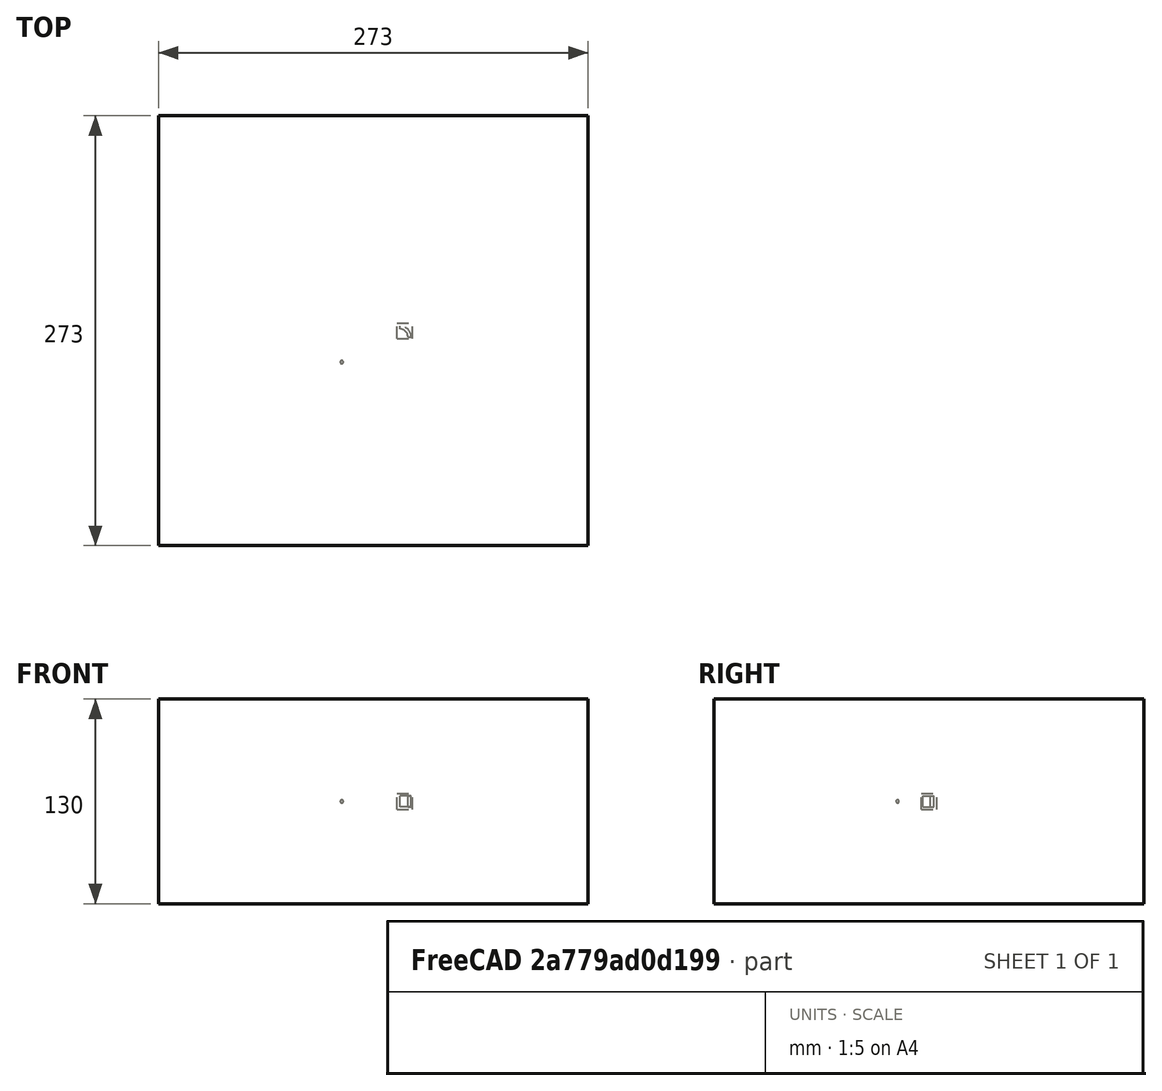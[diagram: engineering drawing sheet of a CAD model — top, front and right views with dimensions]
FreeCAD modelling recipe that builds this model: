
FCSTD DOCUMENT  (FreeCAD 1.0R39109 (Git))
Label: polarArray-of-Part-base-xformed-offcenter
License: All rights reserved
LicenseURL: http://en.wikipedia.org/wiki/All_rights_reserved
objects: App::DocumentObjectGroupPython×1251, App::Part×5, Part::FeaturePython×4, Part::Sphere×1
note: 4 computed .brp shape members not serialized (recipe doc carries the construction recipe); baked Part::Feature solids carry a one-line shape summary decoded from their .brp

FEATURE [App::DocumentObjectGroupPython] HALFPI  # scripted group (container) (typed FeaturePython)
  name = HALFPI
  value = pi/2.
FEATURE [App::DocumentObjectGroupPython] PI  # scripted group (container) (typed FeaturePython)
  name = PI
  value = 1.*pi
FEATURE [App::DocumentObjectGroupPython] TWOPI  # scripted group (container) (typed FeaturePython)
  name = TWOPI
  value = 2.*pi
FEATURE [App::DocumentObjectGroupPython] Constants  # scripted group (container) (typed FeaturePython)
  Group = -> [HALFPI,PI,TWOPI]
FEATURE [App::DocumentObjectGroupPython] Variables  # scripted group (container) (typed FeaturePython)
FEATURE [App::DocumentObjectGroupPython] Quantities  # scripted group (container) (typed FeaturePython)
FEATURE [App::DocumentObjectGroupPython] Isotopes  # scripted group (container) (typed FeaturePython)
FEATURE [App::DocumentObjectGroupPython] Elements  # scripted group (container) (typed FeaturePython)
FEATURE [App::DocumentObjectGroupPython] Matrix  # scripted group (container) (typed FeaturePython)
FEATURE [App::DocumentObjectGroupPython] Surfaces  # scripted group (container) (typed FeaturePython)
FEATURE [App::DocumentObjectGroupPython] Opticals  # scripted group (container) (typed FeaturePython)
  Group = -> [Matrix,Surfaces]
FEATURE [App::DocumentObjectGroupPython] G4Isotopes  # scripted group (container) (typed FeaturePython)
FEATURE [App::DocumentObjectGroupPython] H_element  # scripted group (container) (typed FeaturePython)
  Z = 1
  atom_value = 1.008
  formula = H
  name = H_element
FEATURE [App::DocumentObjectGroupPython] He_element  # scripted group (container) (typed FeaturePython)
  Z = 2
  atom_value = 4.0026
  formula = He
  name = He_element
FEATURE [App::DocumentObjectGroupPython] Li_element  # scripted group (container) (typed FeaturePython)
  Z = 3
  atom_value = 6.94
  formula = Li
  name = Li_element
FEATURE [App::DocumentObjectGroupPython] Be_element  # scripted group (container) (typed FeaturePython)
  Z = 4
  atom_value = 9.01218
  formula = Be
  name = Be_element
FEATURE [App::DocumentObjectGroupPython] B_element  # scripted group (container) (typed FeaturePython)
  Z = 5
  atom_value = 10.81
  formula = B
  name = B_element
FEATURE [App::DocumentObjectGroupPython] C_element  # scripted group (container) (typed FeaturePython)
  Z = 6
  atom_value = 12.011
  formula = C
  name = C_element
FEATURE [App::DocumentObjectGroupPython] N_element  # scripted group (container) (typed FeaturePython)
  Z = 7
  atom_value = 14.007
  formula = N
  name = N_element
FEATURE [App::DocumentObjectGroupPython] O_element  # scripted group (container) (typed FeaturePython)
  Z = 8
  atom_value = 15.999
  formula = O
  name = O_element
FEATURE [App::DocumentObjectGroupPython] F_element  # scripted group (container) (typed FeaturePython)
  Z = 9
  atom_value = 18.9984
  formula = F
  name = F_element
FEATURE [App::DocumentObjectGroupPython] Ne_element  # scripted group (container) (typed FeaturePython)
  Z = 10
  atom_value = 20.1797
  formula = Ne
  name = Ne_element
FEATURE [App::DocumentObjectGroupPython] Na_element  # scripted group (container) (typed FeaturePython)
  Z = 11
  atom_value = 22.9898
  formula = Na
  name = Na_element
FEATURE [App::DocumentObjectGroupPython] Mg_element  # scripted group (container) (typed FeaturePython)
  Z = 12
  atom_value = 24.305
  formula = Mg
  name = Mg_element
FEATURE [App::DocumentObjectGroupPython] Al_element  # scripted group (container) (typed FeaturePython)
  Z = 13
  atom_value = 26.9815
  formula = Al
  name = Al_element
FEATURE [App::DocumentObjectGroupPython] Si_element  # scripted group (container) (typed FeaturePython)
  Z = 14
  atom_value = 28.085
  formula = Si
  name = Si_element
FEATURE [App::DocumentObjectGroupPython] P_element  # scripted group (container) (typed FeaturePython)
  Z = 15
  atom_value = 30.9738
  formula = P
  name = P_element
FEATURE [App::DocumentObjectGroupPython] S_element  # scripted group (container) (typed FeaturePython)
  Z = 16
  atom_value = 32.06
  formula = S
  name = S_element
FEATURE [App::DocumentObjectGroupPython] Cl_element  # scripted group (container) (typed FeaturePython)
  Z = 17
  atom_value = 35.45
  formula = Cl
  name = Cl_element
FEATURE [App::DocumentObjectGroupPython] Ar_element  # scripted group (container) (typed FeaturePython)
  Z = 18
  atom_value = 39.95
  formula = Ar
  name = Ar_element
FEATURE [App::DocumentObjectGroupPython] K_element  # scripted group (container) (typed FeaturePython)
  Z = 19
  atom_value = 39.0983
  formula = K
  name = K_element
FEATURE [App::DocumentObjectGroupPython] Ca_element  # scripted group (container) (typed FeaturePython)
  Z = 20
  atom_value = 40.078
  formula = Ca
  name = Ca_element
FEATURE [App::DocumentObjectGroupPython] Sc_element  # scripted group (container) (typed FeaturePython)
  Z = 21
  atom_value = 44.9559
  formula = Sc
  name = Sc_element
FEATURE [App::DocumentObjectGroupPython] Ti_element  # scripted group (container) (typed FeaturePython)
  Z = 22
  atom_value = 47.867
  formula = Ti
  name = Ti_element
FEATURE [App::DocumentObjectGroupPython] V_element  # scripted group (container) (typed FeaturePython)
  Z = 23
  atom_value = 50.9415
  formula = V
  name = V_element
FEATURE [App::DocumentObjectGroupPython] Cr_element  # scripted group (container) (typed FeaturePython)
  Z = 24
  atom_value = 51.9961
  formula = Cr
  name = Cr_element
FEATURE [App::DocumentObjectGroupPython] Mn_element  # scripted group (container) (typed FeaturePython)
  Z = 25
  atom_value = 54.938
  formula = Mn
  name = Mn_element
FEATURE [App::DocumentObjectGroupPython] Fe_element  # scripted group (container) (typed FeaturePython)
  Z = 26
  atom_value = 55.845
  formula = Fe
  name = Fe_element
FEATURE [App::DocumentObjectGroupPython] Co_element  # scripted group (container) (typed FeaturePython)
  Z = 27
  atom_value = 58.9332
  formula = Co
  name = Co_element
FEATURE [App::DocumentObjectGroupPython] Ni_element  # scripted group (container) (typed FeaturePython)
  Z = 28
  atom_value = 58.6934
  formula = Ni
  name = Ni_element
FEATURE [App::DocumentObjectGroupPython] Cu_element  # scripted group (container) (typed FeaturePython)
  Z = 29
  atom_value = 63.546
  formula = Cu
  name = Cu_element
FEATURE [App::DocumentObjectGroupPython] Zn_element  # scripted group (container) (typed FeaturePython)
  Z = 30
  atom_value = 65.38
  formula = Zn
  name = Zn_element
FEATURE [App::DocumentObjectGroupPython] Ga_element  # scripted group (container) (typed FeaturePython)
  Z = 31
  atom_value = 69.723
  formula = Ga
  name = Ga_element
FEATURE [App::DocumentObjectGroupPython] Ge_element  # scripted group (container) (typed FeaturePython)
  Z = 32
  atom_value = 72.63
  formula = Ge
  name = Ge_element
FEATURE [App::DocumentObjectGroupPython] As_element  # scripted group (container) (typed FeaturePython)
  Z = 33
  atom_value = 74.9216
  formula = As
  name = As_element
FEATURE [App::DocumentObjectGroupPython] Se_element  # scripted group (container) (typed FeaturePython)
  Z = 34
  atom_value = 78.971
  formula = Se
  name = Se_element
FEATURE [App::DocumentObjectGroupPython] Br_element  # scripted group (container) (typed FeaturePython)
  Z = 35
  atom_value = 79.904
  formula = Br
  name = Br_element
FEATURE [App::DocumentObjectGroupPython] Kr_element  # scripted group (container) (typed FeaturePython)
  Z = 36
  atom_value = 83.798
  formula = Kr
  name = Kr_element
FEATURE [App::DocumentObjectGroupPython] Rb_element  # scripted group (container) (typed FeaturePython)
  Z = 37
  atom_value = 85.4678
  formula = Rb
  name = Rb_element
FEATURE [App::DocumentObjectGroupPython] Sr_element  # scripted group (container) (typed FeaturePython)
  Z = 38
  atom_value = 87.62
  formula = Sr
  name = Sr_element
FEATURE [App::DocumentObjectGroupPython] Y_element  # scripted group (container) (typed FeaturePython)
  Z = 39
  atom_value = 88.9058
  formula = Y
  name = Y_element
FEATURE [App::DocumentObjectGroupPython] Zr_element  # scripted group (container) (typed FeaturePython)
  Z = 40
  atom_value = 91.224
  formula = Zr
  name = Zr_element
FEATURE [App::DocumentObjectGroupPython] Nb_element  # scripted group (container) (typed FeaturePython)
  Z = 41
  atom_value = 92.9064
  formula = Nb
  name = Nb_element
FEATURE [App::DocumentObjectGroupPython] Mo_element  # scripted group (container) (typed FeaturePython)
  Z = 42
  atom_value = 95.95
  formula = Mo
  name = Mo_element
FEATURE [App::DocumentObjectGroupPython] Tc_element  # scripted group (container) (typed FeaturePython)
  Z = 43
  atom_value = 97
  formula = Tc
  name = Tc_element
FEATURE [App::DocumentObjectGroupPython] Ru_element  # scripted group (container) (typed FeaturePython)
  Z = 44
  atom_value = 101.07
  formula = Ru
  name = Ru_element
FEATURE [App::DocumentObjectGroupPython] Rh_element  # scripted group (container) (typed FeaturePython)
  Z = 45
  atom_value = 102.905
  formula = Rh
  name = Rh_element
FEATURE [App::DocumentObjectGroupPython] Pd_element  # scripted group (container) (typed FeaturePython)
  Z = 46
  atom_value = 106.42
  formula = Pd
  name = Pd_element
FEATURE [App::DocumentObjectGroupPython] Ag_element  # scripted group (container) (typed FeaturePython)
  Z = 47
  atom_value = 107.868
  formula = Ag
  name = Ag_element
FEATURE [App::DocumentObjectGroupPython] Cd_element  # scripted group (container) (typed FeaturePython)
  Z = 48
  atom_value = 112.414
  formula = Cd
  name = Cd_element
FEATURE [App::DocumentObjectGroupPython] In_element  # scripted group (container) (typed FeaturePython)
  Z = 49
  atom_value = 114.818
  formula = In
  name = In_element
FEATURE [App::DocumentObjectGroupPython] Sn_element  # scripted group (container) (typed FeaturePython)
  Z = 50
  atom_value = 118.71
  formula = Sn
  name = Sn_element
FEATURE [App::DocumentObjectGroupPython] Sb_element  # scripted group (container) (typed FeaturePython)
  Z = 51
  atom_value = 121.76
  formula = Sb
  name = Sb_element
FEATURE [App::DocumentObjectGroupPython] Te_element  # scripted group (container) (typed FeaturePython)
  Z = 52
  atom_value = 127.6
  formula = Te
  name = Te_element
FEATURE [App::DocumentObjectGroupPython] I_element  # scripted group (container) (typed FeaturePython)
  Z = 53
  atom_value = 126.904
  formula = I
  name = I_element
FEATURE [App::DocumentObjectGroupPython] Xe_element  # scripted group (container) (typed FeaturePython)
  Z = 54
  atom_value = 131.293
  formula = Xe
  name = Xe_element
FEATURE [App::DocumentObjectGroupPython] Cs_element  # scripted group (container) (typed FeaturePython)
  Z = 55
  atom_value = 132.905
  formula = Cs
  name = Cs_element
FEATURE [App::DocumentObjectGroupPython] Ba_element  # scripted group (container) (typed FeaturePython)
  Z = 56
  atom_value = 137.327
  formula = Ba
  name = Ba_element
FEATURE [App::DocumentObjectGroupPython] La_element  # scripted group (container) (typed FeaturePython)
  Z = 57
  atom_value = 138.905
  formula = La
  name = La_element
FEATURE [App::DocumentObjectGroupPython] Ce_element  # scripted group (container) (typed FeaturePython)
  Z = 58
  atom_value = 140.116
  formula = Ce
  name = Ce_element
FEATURE [App::DocumentObjectGroupPython] Pr_element  # scripted group (container) (typed FeaturePython)
  Z = 59
  atom_value = 140.908
  formula = Pr
  name = Pr_element
FEATURE [App::DocumentObjectGroupPython] Nd_element  # scripted group (container) (typed FeaturePython)
  Z = 60
  atom_value = 144.242
  formula = Nd
  name = Nd_element
FEATURE [App::DocumentObjectGroupPython] Pm_element  # scripted group (container) (typed FeaturePython)
  Z = 61
  atom_value = 145
  formula = Pm
  name = Pm_element
FEATURE [App::DocumentObjectGroupPython] Sm_element  # scripted group (container) (typed FeaturePython)
  Z = 62
  atom_value = 150.36
  formula = Sm
  name = Sm_element
FEATURE [App::DocumentObjectGroupPython] Eu_element  # scripted group (container) (typed FeaturePython)
  Z = 63
  atom_value = 151.964
  formula = Eu
  name = Eu_element
FEATURE [App::DocumentObjectGroupPython] Gd_element  # scripted group (container) (typed FeaturePython)
  Z = 64
  atom_value = 157.25
  formula = Gd
  name = Gd_element
FEATURE [App::DocumentObjectGroupPython] Tb_element  # scripted group (container) (typed FeaturePython)
  Z = 65
  atom_value = 158.925
  formula = Tb
  name = Tb_element
FEATURE [App::DocumentObjectGroupPython] Dy_element  # scripted group (container) (typed FeaturePython)
  Z = 66
  atom_value = 162.5
  formula = Dy
  name = Dy_element
FEATURE [App::DocumentObjectGroupPython] Ho_element  # scripted group (container) (typed FeaturePython)
  Z = 67
  atom_value = 164.93
  formula = Ho
  name = Ho_element
FEATURE [App::DocumentObjectGroupPython] Er_element  # scripted group (container) (typed FeaturePython)
  Z = 68
  atom_value = 167.259
  formula = Er
  name = Er_element
FEATURE [App::DocumentObjectGroupPython] Tm_element  # scripted group (container) (typed FeaturePython)
  Z = 69
  atom_value = 168.934
  formula = Tm
  name = Tm_element
FEATURE [App::DocumentObjectGroupPython] Yb_element  # scripted group (container) (typed FeaturePython)
  Z = 70
  atom_value = 173.045
  formula = Yb
  name = Yb_element
FEATURE [App::DocumentObjectGroupPython] Lu_element  # scripted group (container) (typed FeaturePython)
  Z = 71
  atom_value = 174.967
  formula = Lu
  name = Lu_element
FEATURE [App::DocumentObjectGroupPython] Hf_element  # scripted group (container) (typed FeaturePython)
  Z = 72
  atom_value = 178.49
  formula = Hf
  name = Hf_element
FEATURE [App::DocumentObjectGroupPython] Ta_element  # scripted group (container) (typed FeaturePython)
  Z = 73
  atom_value = 180.948
  formula = Ta
  name = Ta_element
FEATURE [App::DocumentObjectGroupPython] W_element  # scripted group (container) (typed FeaturePython)
  Z = 74
  atom_value = 183.84
  formula = W
  name = W_element
FEATURE [App::DocumentObjectGroupPython] Re_element  # scripted group (container) (typed FeaturePython)
  Z = 75
  atom_value = 186.207
  formula = Re
  name = Re_element
FEATURE [App::DocumentObjectGroupPython] Os_element  # scripted group (container) (typed FeaturePython)
  Z = 76
  atom_value = 190.23
  formula = Os
  name = Os_element
FEATURE [App::DocumentObjectGroupPython] Ir_element  # scripted group (container) (typed FeaturePython)
  Z = 77
  atom_value = 192.217
  formula = Ir
  name = Ir_element
FEATURE [App::DocumentObjectGroupPython] Pt_element  # scripted group (container) (typed FeaturePython)
  Z = 78
  atom_value = 195.084
  formula = Pt
  name = Pt_element
FEATURE [App::DocumentObjectGroupPython] Au_element  # scripted group (container) (typed FeaturePython)
  Z = 79
  atom_value = 196.967
  formula = Au
  name = Au_element
FEATURE [App::DocumentObjectGroupPython] Hg_element  # scripted group (container) (typed FeaturePython)
  Z = 80
  atom_value = 200.592
  formula = Hg
  name = Hg_element
FEATURE [App::DocumentObjectGroupPython] Tl_element  # scripted group (container) (typed FeaturePython)
  Z = 81
  atom_value = 204.38
  formula = Tl
  name = Tl_element
FEATURE [App::DocumentObjectGroupPython] Pb_element  # scripted group (container) (typed FeaturePython)
  Z = 82
  atom_value = 207.2
  formula = Pb
  name = Pb_element
FEATURE [App::DocumentObjectGroupPython] Bi_element  # scripted group (container) (typed FeaturePython)
  Z = 83
  atom_value = 208.98
  formula = Bi
  name = Bi_element
FEATURE [App::DocumentObjectGroupPython] Po_element  # scripted group (container) (typed FeaturePython)
  Z = 84
  atom_value = 209
  formula = Po
  name = Po_element
FEATURE [App::DocumentObjectGroupPython] At_element  # scripted group (container) (typed FeaturePython)
  Z = 85
  atom_value = 210
  formula = At
  name = At_element
FEATURE [App::DocumentObjectGroupPython] Rn_element  # scripted group (container) (typed FeaturePython)
  Z = 86
  atom_value = 222
  formula = Rn
  name = Rn_element
FEATURE [App::DocumentObjectGroupPython] Fr_element  # scripted group (container) (typed FeaturePython)
  Z = 87
  atom_value = 223
  formula = Fr
  name = Fr_element
FEATURE [App::DocumentObjectGroupPython] Ra_element  # scripted group (container) (typed FeaturePython)
  Z = 88
  atom_value = 226
  formula = Ra
  name = Ra_element
FEATURE [App::DocumentObjectGroupPython] Ac_element  # scripted group (container) (typed FeaturePython)
  Z = 89
  atom_value = 227
  formula = Ac
  name = Ac_element
FEATURE [App::DocumentObjectGroupPython] Th_element  # scripted group (container) (typed FeaturePython)
  Z = 90
  atom_value = 232.038
  formula = Th
  name = Th_element
FEATURE [App::DocumentObjectGroupPython] Pa_element  # scripted group (container) (typed FeaturePython)
  Z = 91
  atom_value = 231.036
  formula = Pa
  name = Pa_element
FEATURE [App::DocumentObjectGroupPython] U_element  # scripted group (container) (typed FeaturePython)
  Z = 92
  atom_value = 238.029
  formula = U
  name = U_element
FEATURE [App::DocumentObjectGroupPython] Np_element  # scripted group (container) (typed FeaturePython)
  Z = 93
  atom_value = 237
  formula = Np
  name = Np_element
FEATURE [App::DocumentObjectGroupPython] Pu_element  # scripted group (container) (typed FeaturePython)
  Z = 94
  atom_value = 244
  formula = Pu
  name = Pu_element
FEATURE [App::DocumentObjectGroupPython] Am_element  # scripted group (container) (typed FeaturePython)
  Z = 95
  atom_value = 243
  formula = Am
  name = Am_element
FEATURE [App::DocumentObjectGroupPython] Cm_element  # scripted group (container) (typed FeaturePython)
  Z = 96
  atom_value = 247
  formula = Cm
  name = Cm_element
FEATURE [App::DocumentObjectGroupPython] Bk_element  # scripted group (container) (typed FeaturePython)
  Z = 97
  atom_value = 247
  formula = Bk
  name = Bk_element
FEATURE [App::DocumentObjectGroupPython] Cf_element  # scripted group (container) (typed FeaturePython)
  Z = 98
  atom_value = 251
  formula = Cf
  name = Cf_element
FEATURE [App::DocumentObjectGroupPython] G4Elements  # scripted group (container) (typed FeaturePython)
  Group = -> [H_element,He_element,Li_element,Be_element,B_element,C_element,N_element,O_element,F_element,Ne_element,Na_element,Mg_element,Al_element,Si_element,P_element,S_element,Cl_element,Ar_element,K_element,Ca_element,Sc_element,Ti_element,V_element,Cr_element,Mn_element,Fe_element,Co_element,Ni_element,Cu_element,Zn_element,Ga_element,Ge_element,As_element,Se_element,Br_element,Kr_element,Rb_element,+61 more]
FEATURE [App::DocumentObjectGroupPython] H_element001  label="H_element : 0.101"  # scripted group (container) (typed FeaturePython)
  n = 0.101327
FEATURE [App::DocumentObjectGroupPython] C_element001  label="C_element : 0.775"  # scripted group (container) (typed FeaturePython)
  n = 0.7755
FEATURE [App::DocumentObjectGroupPython] N_element001  label="N_element : 0.035"  # scripted group (container) (typed FeaturePython)
  n = 0.035057
FEATURE [App::DocumentObjectGroupPython] O_element001  label="O_element : 0.052"  # scripted group (container) (typed FeaturePython)
  n = 0.0523159
FEATURE [App::DocumentObjectGroupPython] F_element001  label="F_element : 0.017"  # scripted group (container) (typed FeaturePython)
  n = 0.017422
FEATURE [App::DocumentObjectGroupPython] Ca_element001  label="Ca_element : 0.018"  # scripted group (container) (typed FeaturePython)
  n = 0.018378
FEATURE [App::DocumentObjectGroupPython] G4_A_150_TISSUE  label="G4_A-150_TISSUE"  # scripted group (container) (typed FeaturePython)
  Dunit = g/cm3
  Dvalue = 1.127
  Group = -> [H_element001,C_element001,N_element001,O_element001,F_element001,Ca_element001]
  conduct = 2
  density = 1
  expand = 3
  formula = G4_A-150_TISSUE
  name = G4_A-150_TISSUE
  specific = 4
FEATURE [App::DocumentObjectGroupPython] C_element002  label="C_element : 3"  # scripted group (container) (typed FeaturePython)
  n = 3
  ref = C_element
FEATURE [App::DocumentObjectGroupPython] H_element002  label="H_element : 6"  # scripted group (container) (typed FeaturePython)
  n = 6
  ref = H_element
FEATURE [App::DocumentObjectGroupPython] O_element002  label="O_element : 1"  # scripted group (container) (typed FeaturePython)
  n = 1
  ref = O_element
FEATURE [App::DocumentObjectGroupPython] G4_ACETONE  # scripted group (container) (typed FeaturePython)
  Dunit = g/cm3
  Dvalue = 0.7899
  Group = -> [C_element002,H_element002,O_element002]
  conduct = 2
  density = 1
  expand = 3
  formula = G4_ACETONE
  name = G4_ACETONE
  specific = 4
FEATURE [App::DocumentObjectGroupPython] C_element003  label="C_element : 2"  # scripted group (container) (typed FeaturePython)
  n = 2
  ref = C_element
FEATURE [App::DocumentObjectGroupPython] H_element003  label="H_element : 2"  # scripted group (container) (typed FeaturePython)
  n = 2
  ref = H_element
FEATURE [App::DocumentObjectGroupPython] G4_ACETYLENE  # scripted group (container) (typed FeaturePython)
  Dunit = g/cm3
  Dvalue = 0.0010967
  Group = -> [C_element003,H_element003]
  conduct = 2
  density = 1
  expand = 3
  formula = G4_ACETYLENE
  name = G4_ACETYLENE
  specific = 4
FEATURE [App::DocumentObjectGroupPython] C_element004  label="C_element : 5"  # scripted group (container) (typed FeaturePython)
  n = 5
  ref = C_element
FEATURE [App::DocumentObjectGroupPython] H_element004  label="H_element : 5"  # scripted group (container) (typed FeaturePython)
  n = 5
  ref = H_element
FEATURE [App::DocumentObjectGroupPython] N_element002  label="N_element : 5"  # scripted group (container) (typed FeaturePython)
  n = 5
  ref = N_element
FEATURE [App::DocumentObjectGroupPython] G4_ADENINE  # scripted group (container) (typed FeaturePython)
  Dunit = g/cm3
  Dvalue = 1.6
  Group = -> [C_element004,H_element004,N_element002]
  conduct = 2
  density = 1
  expand = 3
  formula = G4_ADENINE
  name = G4_ADENINE
  specific = 4
FEATURE [App::DocumentObjectGroupPython] H_element005  label="H_element : 0.114"  # scripted group (container) (typed FeaturePython)
  n = 0.114
FEATURE [App::DocumentObjectGroupPython] C_element005  label="C_element : 0.598"  # scripted group (container) (typed FeaturePython)
  n = 0.598
FEATURE [App::DocumentObjectGroupPython] N_element003  label="N_element : 0.007"  # scripted group (container) (typed FeaturePython)
  n = 0.007
FEATURE [App::DocumentObjectGroupPython] O_element003  label="O_element : 0.278"  # scripted group (container) (typed FeaturePython)
  n = 0.278
FEATURE [App::DocumentObjectGroupPython] Na_element001  label="Na_element : 0.001"  # scripted group (container) (typed FeaturePython)
  n = 0.001
FEATURE [App::DocumentObjectGroupPython] S_element001  label="S_element : 0.001"  # scripted group (container) (typed FeaturePython)
  n = 0.001
FEATURE [App::DocumentObjectGroupPython] Cl_element001  label="Cl_element : 0.001"  # scripted group (container) (typed FeaturePython)
  n = 0.001
FEATURE [App::DocumentObjectGroupPython] G4_ADIPOSE_TISSUE_ICRP  # scripted group (container) (typed FeaturePython)
  Dunit = g/cm3
  Dvalue = 0.95
  Group = -> [H_element005,C_element005,N_element003,O_element003,Na_element001,S_element001,Cl_element001]
  conduct = 2
  density = 1
  expand = 3
  formula = G4_ADIPOSE_TISSUE_ICRP
  name = G4_ADIPOSE_TISSUE_ICRP
  specific = 4
FEATURE [App::DocumentObjectGroupPython] C_element006  label="C_element : 0.000"  # scripted group (container) (typed FeaturePython)
  n = 0.000124
FEATURE [App::DocumentObjectGroupPython] N_element004  label="N_element : 0.755"  # scripted group (container) (typed FeaturePython)
  n = 0.755268
FEATURE [App::DocumentObjectGroupPython] O_element004  label="O_element : 0.232"  # scripted group (container) (typed FeaturePython)
  n = 0.231781
FEATURE [App::DocumentObjectGroupPython] Ar_element001  label="Ar_element : 0.013"  # scripted group (container) (typed FeaturePython)
  n = 0.012827
FEATURE [App::DocumentObjectGroupPython] G4_AIR  # scripted group (container) (typed FeaturePython)
  Dunit = g/cm3
  Dvalue = 0.00120479
  Group = -> [C_element006,N_element004,O_element004,Ar_element001]
  conduct = 2
  density = 1
  expand = 3
  formula = G4_AIR
  name = G4_AIR
  specific = 4
FEATURE [App::DocumentObjectGroupPython] C_element007  label="C_element : 006"  # scripted group (container) (typed FeaturePython)
  n = 3
  ref = C_element
FEATURE [App::DocumentObjectGroupPython] H_element006  label="H_element : 7"  # scripted group (container) (typed FeaturePython)
  n = 7
  ref = H_element
FEATURE [App::DocumentObjectGroupPython] N_element005  label="N_element : 1"  # scripted group (container) (typed FeaturePython)
  n = 1
  ref = N_element
FEATURE [App::DocumentObjectGroupPython] O_element005  label="O_element : 2"  # scripted group (container) (typed FeaturePython)
  n = 2
  ref = O_element
FEATURE [App::DocumentObjectGroupPython] G4_ALANINE  # scripted group (container) (typed FeaturePython)
  Dunit = g/cm3
  Dvalue = 1.42
  Group = -> [C_element007,H_element006,N_element005,O_element005]
  conduct = 2
  density = 1
  expand = 3
  formula = G4_ALANINE
  name = G4_ALANINE
  specific = 4
FEATURE [App::DocumentObjectGroupPython] Al_element001  label="Al_element : 2"  # scripted group (container) (typed FeaturePython)
  n = 2
  ref = Al_element
FEATURE [App::DocumentObjectGroupPython] O_element006  label="O_element : 3"  # scripted group (container) (typed FeaturePython)
  n = 3
  ref = O_element
FEATURE [App::DocumentObjectGroupPython] G4_ALUMINUM_OXIDE  # scripted group (container) (typed FeaturePython)
  Dunit = g/cm3
  Dvalue = 3.97
  Group = -> [Al_element001,O_element006]
  conduct = 2
  density = 1
  expand = 3
  formula = G4_ALUMINUM_OXIDE
  name = G4_ALUMINUM_OXIDE
  specific = 4
FEATURE [App::DocumentObjectGroupPython] H_element007  label="H_element : 0.106"  # scripted group (container) (typed FeaturePython)
  n = 0.10593
FEATURE [App::DocumentObjectGroupPython] C_element008  label="C_element : 0.789"  # scripted group (container) (typed FeaturePython)
  n = 0.788974
FEATURE [App::DocumentObjectGroupPython] O_element007  label="O_element : 0.105"  # scripted group (container) (typed FeaturePython)
  n = 0.105096
FEATURE [App::DocumentObjectGroupPython] G4_AMBER  # scripted group (container) (typed FeaturePython)
  Dunit = g/cm3
  Dvalue = 1.1
  Group = -> [H_element007,C_element008,O_element007]
  conduct = 2
  density = 1
  expand = 3
  formula = G4_AMBER
  name = G4_AMBER
  specific = 4
FEATURE [App::DocumentObjectGroupPython] N_element006  label="N_element : 006"  # scripted group (container) (typed FeaturePython)
  n = 1
  ref = N_element
FEATURE [App::DocumentObjectGroupPython] H_element008  label="H_element : 3"  # scripted group (container) (typed FeaturePython)
  n = 3
  ref = H_element
FEATURE [App::DocumentObjectGroupPython] G4_AMMONIA  # scripted group (container) (typed FeaturePython)
  Dunit = g/cm3
  Dvalue = 0.000826019
  Group = -> [N_element006,H_element008]
  conduct = 2
  density = 1
  expand = 3
  formula = G4_AMMONIA
  name = G4_AMMONIA
  specific = 4
FEATURE [App::DocumentObjectGroupPython] C_element009  label="C_element : 6"  # scripted group (container) (typed FeaturePython)
  n = 6
  ref = C_element
FEATURE [App::DocumentObjectGroupPython] H_element009  label="H_element : 008"  # scripted group (container) (typed FeaturePython)
  n = 7
  ref = H_element
FEATURE [App::DocumentObjectGroupPython] N_element007  label="N_element : 007"  # scripted group (container) (typed FeaturePython)
  n = 1
  ref = N_element
FEATURE [App::DocumentObjectGroupPython] G4_ANILINE  # scripted group (container) (typed FeaturePython)
  Dunit = g/cm3
  Dvalue = 1.0235
  Group = -> [C_element009,H_element009,N_element007]
  conduct = 2
  density = 1
  expand = 3
  formula = G4_ANILINE
  name = G4_ANILINE
  specific = 4
FEATURE [App::DocumentObjectGroupPython] C_element010  label="C_element : 14"  # scripted group (container) (typed FeaturePython)
  n = 14
  ref = C_element
FEATURE [App::DocumentObjectGroupPython] H_element010  label="H_element : 10"  # scripted group (container) (typed FeaturePython)
  n = 10
  ref = H_element
FEATURE [App::DocumentObjectGroupPython] G4_ANTHRACENE  # scripted group (container) (typed FeaturePython)
  Dunit = g/cm3
  Dvalue = 1.283
  Group = -> [C_element010,H_element010]
  conduct = 2
  density = 1
  expand = 3
  formula = G4_ANTHRACENE
  name = G4_ANTHRACENE
  specific = 4
FEATURE [App::DocumentObjectGroupPython] H_element011  label="H_element : 0.065"  # scripted group (container) (typed FeaturePython)
  n = 0.0654709
FEATURE [App::DocumentObjectGroupPython] C_element011  label="C_element : 0.537"  # scripted group (container) (typed FeaturePython)
  n = 0.536944
FEATURE [App::DocumentObjectGroupPython] N_element008  label="N_element : 0.021"  # scripted group (container) (typed FeaturePython)
  n = 0.0215
FEATURE [App::DocumentObjectGroupPython] O_element008  label="O_element : 0.032"  # scripted group (container) (typed FeaturePython)
  n = 0.032085
FEATURE [App::DocumentObjectGroupPython] F_element002  label="F_element : 0.167"  # scripted group (container) (typed FeaturePython)
  n = 0.167411
FEATURE [App::DocumentObjectGroupPython] Ca_element002  label="Ca_element : 0.177"  # scripted group (container) (typed FeaturePython)
  n = 0.176589
FEATURE [App::DocumentObjectGroupPython] G4_B_100_BONE  label="G4_B-100_BONE"  # scripted group (container) (typed FeaturePython)
  Dunit = g/cm3
  Dvalue = 1.45
  Group = -> [H_element011,C_element011,N_element008,O_element008,F_element002,Ca_element002]
  conduct = 2
  density = 1
  expand = 3
  formula = G4_B-100_BONE
  name = G4_B-100_BONE
  specific = 4
FEATURE [App::DocumentObjectGroupPython] H_element012  label="H_element : 0.057"  # scripted group (container) (typed FeaturePython)
  n = 0.057441
FEATURE [App::DocumentObjectGroupPython] C_element012  label="C_element : 0.790"  # scripted group (container) (typed FeaturePython)
  n = 0.774591
FEATURE [App::DocumentObjectGroupPython] O_element009  label="O_element : 0.168"  # scripted group (container) (typed FeaturePython)
  n = 0.167968
FEATURE [App::DocumentObjectGroupPython] G4_BAKELITE  # scripted group (container) (typed FeaturePython)
  Dunit = g/cm3
  Dvalue = 1.25
  Group = -> [H_element012,C_element012,O_element009]
  conduct = 2
  density = 1
  expand = 3
  formula = G4_BAKELITE
  name = G4_BAKELITE
  specific = 4
FEATURE [App::DocumentObjectGroupPython] Ba_element001  label="Ba_element : 1"  # scripted group (container) (typed FeaturePython)
  n = 1
  ref = Ba_element
FEATURE [App::DocumentObjectGroupPython] F_element003  label="F_element : 2"  # scripted group (container) (typed FeaturePython)
  n = 2
  ref = F_element
FEATURE [App::DocumentObjectGroupPython] G4_BARIUM_FLUORIDE  # scripted group (container) (typed FeaturePython)
  Dunit = g/cm3
  Dvalue = 4.89
  Group = -> [Ba_element001,F_element003]
  conduct = 2
  density = 1
  expand = 3
  formula = G4_BARIUM_FLUORIDE
  name = G4_BARIUM_FLUORIDE
  specific = 4
FEATURE [App::DocumentObjectGroupPython] Ba_element002  label="Ba_element : 002"  # scripted group (container) (typed FeaturePython)
  n = 1
  ref = Ba_element
FEATURE [App::DocumentObjectGroupPython] S_element002  label="S_element : 1"  # scripted group (container) (typed FeaturePython)
  n = 1
  ref = S_element
FEATURE [App::DocumentObjectGroupPython] O_element010  label="O_element : 4"  # scripted group (container) (typed FeaturePython)
  n = 4
  ref = O_element
FEATURE [App::DocumentObjectGroupPython] G4_BARIUM_SULFATE  # scripted group (container) (typed FeaturePython)
  Dunit = g/cm3
  Dvalue = 4.5
  Group = -> [Ba_element002,S_element002,O_element010]
  conduct = 2
  density = 1
  expand = 3
  formula = G4_BARIUM_SULFATE
  name = G4_BARIUM_SULFATE
  specific = 4
FEATURE [App::DocumentObjectGroupPython] C_element013  label="C_element : 007"  # scripted group (container) (typed FeaturePython)
  n = 6
  ref = C_element
FEATURE [App::DocumentObjectGroupPython] H_element013  label="H_element : 009"  # scripted group (container) (typed FeaturePython)
  n = 6
  ref = H_element
FEATURE [App::DocumentObjectGroupPython] G4_BENZENE  # scripted group (container) (typed FeaturePython)
  Dunit = g/cm3
  Dvalue = 0.87865
  Group = -> [C_element013,H_element013]
  conduct = 2
  density = 1
  expand = 3
  formula = G4_BENZENE
  name = G4_BENZENE
  specific = 4
FEATURE [App::DocumentObjectGroupPython] Be_element001  label="Be_element : 1"  # scripted group (container) (typed FeaturePython)
  n = 1
  ref = Be_element
FEATURE [App::DocumentObjectGroupPython] O_element011  label="O_element : 005"  # scripted group (container) (typed FeaturePython)
  n = 1
  ref = O_element
FEATURE [App::DocumentObjectGroupPython] G4_BERYLLIUM_OXIDE  # scripted group (container) (typed FeaturePython)
  Dunit = g/cm3
  Dvalue = 3.01
  Group = -> [Be_element001,O_element011]
  conduct = 2
  density = 1
  expand = 3
  formula = G4_BERYLLIUM_OXIDE
  name = G4_BERYLLIUM_OXIDE
  specific = 4
FEATURE [App::DocumentObjectGroupPython] Bi_element001  label="Bi_element : 4"  # scripted group (container) (typed FeaturePython)
  n = 4
  ref = Bi_element
FEATURE [App::DocumentObjectGroupPython] Ge_element001  label="Ge_element : 3"  # scripted group (container) (typed FeaturePython)
  n = 3
  ref = Ge_element
FEATURE [App::DocumentObjectGroupPython] O_element012  label="O_element : 12"  # scripted group (container) (typed FeaturePython)
  n = 12
  ref = O_element
FEATURE [App::DocumentObjectGroupPython] G4_BGO  # scripted group (container) (typed FeaturePython)
  Dunit = g/cm3
  Dvalue = 7.13
  Group = -> [Bi_element001,Ge_element001,O_element012]
  conduct = 2
  density = 1
  expand = 3
  formula = G4_BGO
  name = G4_BGO
  specific = 4
FEATURE [App::DocumentObjectGroupPython] H_element014  label="H_element : 0.102"  # scripted group (container) (typed FeaturePython)
  n = 0.102
FEATURE [App::DocumentObjectGroupPython] C_element014  label="C_element : 0.110"  # scripted group (container) (typed FeaturePython)
  n = 0.11
FEATURE [App::DocumentObjectGroupPython] N_element009  label="N_element : 0.033"  # scripted group (container) (typed FeaturePython)
  n = 0.033
FEATURE [App::DocumentObjectGroupPython] O_element013  label="O_element : 0.745"  # scripted group (container) (typed FeaturePython)
  n = 0.745
FEATURE [App::DocumentObjectGroupPython] Na_element002  label="Na_element : 0.002"  # scripted group (container) (typed FeaturePython)
  n = 0.001
FEATURE [App::DocumentObjectGroupPython] P_element001  label="P_element : 0.001"  # scripted group (container) (typed FeaturePython)
  n = 0.001
FEATURE [App::DocumentObjectGroupPython] S_element003  label="S_element : 0.002"  # scripted group (container) (typed FeaturePython)
  n = 0.002
FEATURE [App::DocumentObjectGroupPython] Cl_element002  label="Cl_element : 0.003"  # scripted group (container) (typed FeaturePython)
  n = 0.003
FEATURE [App::DocumentObjectGroupPython] K_element001  label="K_element : 0.002"  # scripted group (container) (typed FeaturePython)
  n = 0.002
FEATURE [App::DocumentObjectGroupPython] Fe_element001  label="Fe_element : 0.001"  # scripted group (container) (typed FeaturePython)
  n = 0.001
FEATURE [App::DocumentObjectGroupPython] G4_BLOOD_ICRP  # scripted group (container) (typed FeaturePython)
  Dunit = g/cm3
  Dvalue = 1.06
  Group = -> [H_element014,C_element014,N_element009,O_element013,Na_element002,P_element001,S_element003,Cl_element002,K_element001,Fe_element001]
  conduct = 2
  density = 1
  expand = 3
  formula = G4_BLOOD_ICRP
  name = G4_BLOOD_ICRP
  specific = 4
FEATURE [App::DocumentObjectGroupPython] H_element015  label="H_element : 0.064"  # scripted group (container) (typed FeaturePython)
  n = 0.064
FEATURE [App::DocumentObjectGroupPython] C_element015  label="C_element : 0.278"  # scripted group (container) (typed FeaturePython)
  n = 0.278
FEATURE [App::DocumentObjectGroupPython] N_element010  label="N_element : 0.027"  # scripted group (container) (typed FeaturePython)
  n = 0.027
FEATURE [App::DocumentObjectGroupPython] O_element014  label="O_element : 0.410"  # scripted group (container) (typed FeaturePython)
  n = 0.41
FEATURE [App::DocumentObjectGroupPython] Mg_element001  label="Mg_element : 0.002"  # scripted group (container) (typed FeaturePython)
  n = 0.002
FEATURE [App::DocumentObjectGroupPython] P_element002  label="P_element : 0.070"  # scripted group (container) (typed FeaturePython)
  n = 0.07
FEATURE [App::DocumentObjectGroupPython] S_element004  label="S_element : 0.003"  # scripted group (container) (typed FeaturePython)
  n = 0.002
FEATURE [App::DocumentObjectGroupPython] Ca_element003  label="Ca_element : 0.147"  # scripted group (container) (typed FeaturePython)
  n = 0.147
FEATURE [App::DocumentObjectGroupPython] G4_BONE_COMPACT_ICRU  # scripted group (container) (typed FeaturePython)
  Dunit = g/cm3
  Dvalue = 1.85
  Group = -> [H_element015,C_element015,N_element010,O_element014,Mg_element001,P_element002,S_element004,Ca_element003]
  conduct = 2
  density = 1
  expand = 3
  formula = G4_BONE_COMPACT_ICRU
  name = G4_BONE_COMPACT_ICRU
  specific = 4
FEATURE [App::DocumentObjectGroupPython] H_element016  label="H_element : 0.034"  # scripted group (container) (typed FeaturePython)
  n = 0.034
FEATURE [App::DocumentObjectGroupPython] C_element016  label="C_element : 0.155"  # scripted group (container) (typed FeaturePython)
  n = 0.155
FEATURE [App::DocumentObjectGroupPython] N_element011  label="N_element : 0.042"  # scripted group (container) (typed FeaturePython)
  n = 0.042
FEATURE [App::DocumentObjectGroupPython] O_element015  label="O_element : 0.435"  # scripted group (container) (typed FeaturePython)
  n = 0.435
FEATURE [App::DocumentObjectGroupPython] Na_element003  label="Na_element : 0.003"  # scripted group (container) (typed FeaturePython)
  n = 0.001
FEATURE [App::DocumentObjectGroupPython] Mg_element002  label="Mg_element : 0.003"  # scripted group (container) (typed FeaturePython)
  n = 0.002
FEATURE [App::DocumentObjectGroupPython] P_element003  label="P_element : 0.103"  # scripted group (container) (typed FeaturePython)
  n = 0.103
FEATURE [App::DocumentObjectGroupPython] S_element005  label="S_element : 0.004"  # scripted group (container) (typed FeaturePython)
  n = 0.003
FEATURE [App::DocumentObjectGroupPython] Ca_element004  label="Ca_element : 0.225"  # scripted group (container) (typed FeaturePython)
  n = 0.225
FEATURE [App::DocumentObjectGroupPython] G4_BONE_CORTICAL_ICRP  # scripted group (container) (typed FeaturePython)
  Dunit = g/cm3
  Dvalue = 1.92
  Group = -> [H_element016,C_element016,N_element011,O_element015,Na_element003,Mg_element002,P_element003,S_element005,Ca_element004]
  conduct = 2
  density = 1
  expand = 3
  formula = G4_BONE_CORTICAL_ICRP
  name = G4_BONE_CORTICAL_ICRP
  specific = 4
FEATURE [App::DocumentObjectGroupPython] B_element001  label="B_element : 4"  # scripted group (container) (typed FeaturePython)
  n = 4
  ref = B_element
FEATURE [App::DocumentObjectGroupPython] C_element017  label="C_element : 1"  # scripted group (container) (typed FeaturePython)
  n = 1
  ref = C_element
FEATURE [App::DocumentObjectGroupPython] G4_BORON_CARBIDE  # scripted group (container) (typed FeaturePython)
  Dunit = g/cm3
  Dvalue = 2.52
  Group = -> [B_element001,C_element017]
  conduct = 2
  density = 1
  expand = 3
  formula = G4_BORON_CARBIDE
  name = G4_BORON_CARBIDE
  specific = 4
FEATURE [App::DocumentObjectGroupPython] B_element002  label="B_element : 2"  # scripted group (container) (typed FeaturePython)
  n = 2
  ref = B_element
FEATURE [App::DocumentObjectGroupPython] O_element016  label="O_element : 006"  # scripted group (container) (typed FeaturePython)
  n = 3
  ref = O_element
FEATURE [App::DocumentObjectGroupPython] G4_BORON_OXIDE  # scripted group (container) (typed FeaturePython)
  Dunit = g/cm3
  Dvalue = 1.812
  Group = -> [B_element002,O_element016]
  conduct = 2
  density = 1
  expand = 3
  formula = G4_BORON_OXIDE
  name = G4_BORON_OXIDE
  specific = 4
FEATURE [App::DocumentObjectGroupPython] H_element017  label="H_element : 0.107"  # scripted group (container) (typed FeaturePython)
  n = 0.107
FEATURE [App::DocumentObjectGroupPython] C_element018  label="C_element : 0.145"  # scripted group (container) (typed FeaturePython)
  n = 0.145
FEATURE [App::DocumentObjectGroupPython] N_element012  label="N_element : 0.022"  # scripted group (container) (typed FeaturePython)
  n = 0.022
FEATURE [App::DocumentObjectGroupPython] O_element017  label="O_element : 0.712"  # scripted group (container) (typed FeaturePython)
  n = 0.712
FEATURE [App::DocumentObjectGroupPython] Na_element004  label="Na_element : 0.004"  # scripted group (container) (typed FeaturePython)
  n = 0.002
FEATURE [App::DocumentObjectGroupPython] P_element004  label="P_element : 0.004"  # scripted group (container) (typed FeaturePython)
  n = 0.004
FEATURE [App::DocumentObjectGroupPython] S_element006  label="S_element : 0.005"  # scripted group (container) (typed FeaturePython)
  n = 0.002
FEATURE [App::DocumentObjectGroupPython] Cl_element003  label="Cl_element : 0.004"  # scripted group (container) (typed FeaturePython)
  n = 0.003
FEATURE [App::DocumentObjectGroupPython] K_element002  label="K_element : 0.003"  # scripted group (container) (typed FeaturePython)
  n = 0.003
FEATURE [App::DocumentObjectGroupPython] G4_BRAIN_ICRP  # scripted group (container) (typed FeaturePython)
  Dunit = g/cm3
  Dvalue = 1.04
  Group = -> [H_element017,C_element018,N_element012,O_element017,Na_element004,P_element004,S_element006,Cl_element003,K_element002]
  conduct = 2
  density = 1
  expand = 3
  formula = G4_BRAIN_ICRP
  name = G4_BRAIN_ICRP
  specific = 4
FEATURE [App::DocumentObjectGroupPython] C_element019  label="C_element : 4"  # scripted group (container) (typed FeaturePython)
  n = 4
  ref = C_element
FEATURE [App::DocumentObjectGroupPython] H_element018  label="H_element : 010"  # scripted group (container) (typed FeaturePython)
  n = 10
  ref = H_element
FEATURE [App::DocumentObjectGroupPython] G4_BUTANE  # scripted group (container) (typed FeaturePython)
  Dunit = g/cm3
  Dvalue = 0.00249343
  Group = -> [C_element019,H_element018]
  conduct = 2
  density = 1
  expand = 3
  formula = G4_BUTANE
  name = G4_BUTANE
  specific = 4
FEATURE [App::DocumentObjectGroupPython] C_element020  label="C_element : 008"  # scripted group (container) (typed FeaturePython)
  n = 4
  ref = C_element
FEATURE [App::DocumentObjectGroupPython] H_element019  label="H_element : 011"  # scripted group (container) (typed FeaturePython)
  n = 10
  ref = H_element
FEATURE [App::DocumentObjectGroupPython] O_element018  label="O_element : 007"  # scripted group (container) (typed FeaturePython)
  n = 1
  ref = O_element
FEATURE [App::DocumentObjectGroupPython] G4_N_BUTYL_ALCOHOL  label="G4_N-BUTYL_ALCOHOL"  # scripted group (container) (typed FeaturePython)
  Dunit = g/cm3
  Dvalue = 0.8098
  Group = -> [C_element020,H_element019,O_element018]
  conduct = 2
  density = 1
  expand = 3
  formula = G4_N-BUTYL_ALCOHOL
  name = G4_N-BUTYL_ALCOHOL
  specific = 4
FEATURE [App::DocumentObjectGroupPython] H_element020  label="H_element : 0.025"  # scripted group (container) (typed FeaturePython)
  n = 0.02468
FEATURE [App::DocumentObjectGroupPython] C_element021  label="C_element : 0.502"  # scripted group (container) (typed FeaturePython)
  n = 0.501611
FEATURE [App::DocumentObjectGroupPython] O_element019  label="O_element : 0.005"  # scripted group (container) (typed FeaturePython)
  n = 0.004527
FEATURE [App::DocumentObjectGroupPython] F_element004  label="F_element : 0.465"  # scripted group (container) (typed FeaturePython)
  n = 0.465209
FEATURE [App::DocumentObjectGroupPython] Si_element001  label="Si_element : 0.004"  # scripted group (container) (typed FeaturePython)
  n = 0.003973
FEATURE [App::DocumentObjectGroupPython] G4_C_552  label="G4_C-552"  # scripted group (container) (typed FeaturePython)
  Dunit = g/cm3
  Dvalue = 1.76
  Group = -> [H_element020,C_element021,O_element019,F_element004,Si_element001]
  conduct = 2
  density = 1
  expand = 3
  formula = G4_C-552
  name = G4_C-552
  specific = 4
FEATURE [App::DocumentObjectGroupPython] Cd_element001  label="Cd_element : 1"  # scripted group (container) (typed FeaturePython)
  n = 1
  ref = Cd_element
FEATURE [App::DocumentObjectGroupPython] Te_element001  label="Te_element : 1"  # scripted group (container) (typed FeaturePython)
  n = 1
  ref = Te_element
FEATURE [App::DocumentObjectGroupPython] G4_CADMIUM_TELLURIDE  # scripted group (container) (typed FeaturePython)
  Dunit = g/cm3
  Dvalue = 6.2
  Group = -> [Cd_element001,Te_element001]
  conduct = 2
  density = 1
  expand = 3
  formula = G4_CADMIUM_TELLURIDE
  name = G4_CADMIUM_TELLURIDE
  specific = 4
FEATURE [App::DocumentObjectGroupPython] Cd_element002  label="Cd_element : 002"  # scripted group (container) (typed FeaturePython)
  n = 1
  ref = Cd_element
FEATURE [App::DocumentObjectGroupPython] W_element001  label="W_element : 1"  # scripted group (container) (typed FeaturePython)
  n = 1
  ref = W_element
FEATURE [App::DocumentObjectGroupPython] O_element020  label="O_element : 008"  # scripted group (container) (typed FeaturePython)
  n = 4
  ref = O_element
FEATURE [App::DocumentObjectGroupPython] G4_CADMIUM_TUNGSTATE  # scripted group (container) (typed FeaturePython)
  Dunit = g/cm3
  Dvalue = 7.9
  Group = -> [Cd_element002,W_element001,O_element020]
  conduct = 2
  density = 1
  expand = 3
  formula = G4_CADMIUM_TUNGSTATE
  name = G4_CADMIUM_TUNGSTATE
  specific = 4
FEATURE [App::DocumentObjectGroupPython] Ca_element005  label="Ca_element : 1"  # scripted group (container) (typed FeaturePython)
  n = 1
  ref = Ca_element
FEATURE [App::DocumentObjectGroupPython] C_element022  label="C_element : 009"  # scripted group (container) (typed FeaturePython)
  n = 1
  ref = C_element
FEATURE [App::DocumentObjectGroupPython] O_element021  label="O_element : 009"  # scripted group (container) (typed FeaturePython)
  n = 3
  ref = O_element
FEATURE [App::DocumentObjectGroupPython] G4_CALCIUM_CARBONATE  # scripted group (container) (typed FeaturePython)
  Dunit = g/cm3
  Dvalue = 2.8
  Group = -> [Ca_element005,C_element022,O_element021]
  conduct = 2
  density = 1
  expand = 3
  formula = G4_CALCIUM_CARBONATE
  name = G4_CALCIUM_CARBONATE
  specific = 4
FEATURE [App::DocumentObjectGroupPython] Ca_element006  label="Ca_element : 002"  # scripted group (container) (typed FeaturePython)
  n = 1
  ref = Ca_element
FEATURE [App::DocumentObjectGroupPython] F_element005  label="F_element : 003"  # scripted group (container) (typed FeaturePython)
  n = 2
  ref = F_element
FEATURE [App::DocumentObjectGroupPython] G4_CALCIUM_FLUORIDE  # scripted group (container) (typed FeaturePython)
  Dunit = g/cm3
  Dvalue = 3.18
  Group = -> [Ca_element006,F_element005]
  conduct = 2
  density = 1
  expand = 3
  formula = G4_CALCIUM_FLUORIDE
  name = G4_CALCIUM_FLUORIDE
  specific = 4
FEATURE [App::DocumentObjectGroupPython] Ca_element007  label="Ca_element : 003"  # scripted group (container) (typed FeaturePython)
  n = 1
  ref = Ca_element
FEATURE [App::DocumentObjectGroupPython] O_element022  label="O_element : 010"  # scripted group (container) (typed FeaturePython)
  n = 1
  ref = O_element
FEATURE [App::DocumentObjectGroupPython] G4_CALCIUM_OXIDE  # scripted group (container) (typed FeaturePython)
  Dunit = g/cm3
  Dvalue = 3.3
  Group = -> [Ca_element007,O_element022]
  conduct = 2
  density = 1
  expand = 3
  formula = G4_CALCIUM_OXIDE
  name = G4_CALCIUM_OXIDE
  specific = 4
FEATURE [App::DocumentObjectGroupPython] Ca_element008  label="Ca_element : 004"  # scripted group (container) (typed FeaturePython)
  n = 1
  ref = Ca_element
FEATURE [App::DocumentObjectGroupPython] S_element007  label="S_element : 002"  # scripted group (container) (typed FeaturePython)
  n = 1
  ref = S_element
FEATURE [App::DocumentObjectGroupPython] O_element023  label="O_element : 011"  # scripted group (container) (typed FeaturePython)
  n = 4
  ref = O_element
FEATURE [App::DocumentObjectGroupPython] G4_CALCIUM_SULFATE  # scripted group (container) (typed FeaturePython)
  Dunit = g/cm3
  Dvalue = 2.96
  Group = -> [Ca_element008,S_element007,O_element023]
  conduct = 2
  density = 1
  expand = 3
  formula = G4_CALCIUM_SULFATE
  name = G4_CALCIUM_SULFATE
  specific = 4
FEATURE [App::DocumentObjectGroupPython] Ca_element009  label="Ca_element : 005"  # scripted group (container) (typed FeaturePython)
  n = 1
  ref = Ca_element
FEATURE [App::DocumentObjectGroupPython] W_element002  label="W_element : 002"  # scripted group (container) (typed FeaturePython)
  n = 1
  ref = W_element
FEATURE [App::DocumentObjectGroupPython] O_element024  label="O_element : 012"  # scripted group (container) (typed FeaturePython)
  n = 4
  ref = O_element
FEATURE [App::DocumentObjectGroupPython] G4_CALCIUM_TUNGSTATE  # scripted group (container) (typed FeaturePython)
  Dunit = g/cm3
  Dvalue = 6.062
  Group = -> [Ca_element009,W_element002,O_element024]
  conduct = 2
  density = 1
  expand = 3
  formula = G4_CALCIUM_TUNGSTATE
  name = G4_CALCIUM_TUNGSTATE
  specific = 4
FEATURE [App::DocumentObjectGroupPython] C_element023  label="C_element : 010"  # scripted group (container) (typed FeaturePython)
  n = 1
  ref = C_element
FEATURE [App::DocumentObjectGroupPython] O_element025  label="O_element : 013"  # scripted group (container) (typed FeaturePython)
  n = 2
  ref = O_element
FEATURE [App::DocumentObjectGroupPython] G4_CARBON_DIOXIDE  # scripted group (container) (typed FeaturePython)
  Dunit = g/cm3
  Dvalue = 0.00184212
  Group = -> [C_element023,O_element025]
  conduct = 2
  density = 1
  expand = 3
  formula = G4_CARBON_DIOXIDE
  name = G4_CARBON_DIOXIDE
  specific = 4
FEATURE [App::DocumentObjectGroupPython] C_element024  label="C_element : 011"  # scripted group (container) (typed FeaturePython)
  n = 1
  ref = C_element
FEATURE [App::DocumentObjectGroupPython] Cl_element004  label="Cl_element : 4"  # scripted group (container) (typed FeaturePython)
  n = 4
  ref = Cl_element
FEATURE [App::DocumentObjectGroupPython] G4_CARBON_TETRACHLORIDE  # scripted group (container) (typed FeaturePython)
  Dunit = g/cm3
  Dvalue = 1.594
  Group = -> [C_element024,Cl_element004]
  conduct = 2
  density = 1
  expand = 3
  formula = G4_CARBON_TETRACHLORIDE
  name = G4_CARBON_TETRACHLORIDE
  specific = 4
FEATURE [App::DocumentObjectGroupPython] C_element025  label="C_element : 012"  # scripted group (container) (typed FeaturePython)
  n = 6
  ref = C_element
FEATURE [App::DocumentObjectGroupPython] H_element021  label="H_element : 012"  # scripted group (container) (typed FeaturePython)
  n = 10
  ref = H_element
FEATURE [App::DocumentObjectGroupPython] O_element026  label="O_element : 5"  # scripted group (container) (typed FeaturePython)
  n = 5
  ref = O_element
FEATURE [App::DocumentObjectGroupPython] G4_CELLULOSE_CELLOPHANE  # scripted group (container) (typed FeaturePython)
  Dunit = g/cm3
  Dvalue = 1.42
  Group = -> [C_element025,H_element021,O_element026]
  conduct = 2
  density = 1
  expand = 3
  formula = G4_CELLULOSE_CELLOPHANE
  name = G4_CELLULOSE_CELLOPHANE
  specific = 4
FEATURE [App::DocumentObjectGroupPython] H_element022  label="H_element : 0.067"  # scripted group (container) (typed FeaturePython)
  n = 0.067125
FEATURE [App::DocumentObjectGroupPython] C_element026  label="C_element : 0.545"  # scripted group (container) (typed FeaturePython)
  n = 0.545403
FEATURE [App::DocumentObjectGroupPython] O_element027  label="O_element : 0.387"  # scripted group (container) (typed FeaturePython)
  n = 0.387472
FEATURE [App::DocumentObjectGroupPython] G4_CELLULOSE_BUTYRATE  # scripted group (container) (typed FeaturePython)
  Dunit = g/cm3
  Dvalue = 1.2
  Group = -> [H_element022,C_element026,O_element027]
  conduct = 2
  density = 1
  expand = 3
  formula = G4_CELLULOSE_BUTYRATE
  name = G4_CELLULOSE_BUTYRATE
  specific = 4
FEATURE [App::DocumentObjectGroupPython] H_element023  label="H_element : 0.029"  # scripted group (container) (typed FeaturePython)
  n = 0.029216
FEATURE [App::DocumentObjectGroupPython] C_element027  label="C_element : 0.271"  # scripted group (container) (typed FeaturePython)
  n = 0.271296
FEATURE [App::DocumentObjectGroupPython] N_element013  label="N_element : 0.121"  # scripted group (container) (typed FeaturePython)
  n = 0.121276
FEATURE [App::DocumentObjectGroupPython] O_element028  label="O_element : 0.578"  # scripted group (container) (typed FeaturePython)
  n = 0.578212
FEATURE [App::DocumentObjectGroupPython] G4_CELLULOSE_NITRATE  # scripted group (container) (typed FeaturePython)
  Dunit = g/cm3
  Dvalue = 1.49
  Group = -> [H_element023,C_element027,N_element013,O_element028]
  conduct = 2
  density = 1
  expand = 3
  formula = G4_CELLULOSE_NITRATE
  name = G4_CELLULOSE_NITRATE
  specific = 4
FEATURE [App::DocumentObjectGroupPython] H_element024  label="H_element : 0.108"  # scripted group (container) (typed FeaturePython)
  n = 0.107596
FEATURE [App::DocumentObjectGroupPython] N_element014  label="N_element : 0.001"  # scripted group (container) (typed FeaturePython)
  n = 0.0008
FEATURE [App::DocumentObjectGroupPython] O_element029  label="O_element : 0.875"  # scripted group (container) (typed FeaturePython)
  n = 0.874976
FEATURE [App::DocumentObjectGroupPython] S_element008  label="S_element : 0.015"  # scripted group (container) (typed FeaturePython)
  n = 0.014627
FEATURE [App::DocumentObjectGroupPython] Ce_element001  label="Ce_element : 0.002"  # scripted group (container) (typed FeaturePython)
  n = 0.002001
FEATURE [App::DocumentObjectGroupPython] G4_CERIC_SULFATE  # scripted group (container) (typed FeaturePython)
  Dunit = g/cm3
  Dvalue = 1.03
  Group = -> [H_element024,N_element014,O_element029,S_element008,Ce_element001]
  conduct = 2
  density = 1
  expand = 3
  formula = G4_CERIC_SULFATE
  name = G4_CERIC_SULFATE
  specific = 4
FEATURE [App::DocumentObjectGroupPython] Cs_element001  label="Cs_element : 1"  # scripted group (container) (typed FeaturePython)
  n = 1
  ref = Cs_element
FEATURE [App::DocumentObjectGroupPython] F_element006  label="F_element : 1"  # scripted group (container) (typed FeaturePython)
  n = 1
  ref = F_element
FEATURE [App::DocumentObjectGroupPython] G4_CESIUM_FLUORIDE  # scripted group (container) (typed FeaturePython)
  Dunit = g/cm3
  Dvalue = 4.115
  Group = -> [Cs_element001,F_element006]
  conduct = 2
  density = 1
  expand = 3
  formula = G4_CESIUM_FLUORIDE
  name = G4_CESIUM_FLUORIDE
  specific = 4
FEATURE [App::DocumentObjectGroupPython] Cs_element002  label="Cs_element : 002"  # scripted group (container) (typed FeaturePython)
  n = 1
  ref = Cs_element
FEATURE [App::DocumentObjectGroupPython] I_element001  label="I_element : 1"  # scripted group (container) (typed FeaturePython)
  n = 1
  ref = I_element
FEATURE [App::DocumentObjectGroupPython] G4_CESIUM_IODIDE  # scripted group (container) (typed FeaturePython)
  Dunit = g/cm3
  Dvalue = 4.51
  Group = -> [Cs_element002,I_element001]
  conduct = 2
  density = 1
  expand = 3
  formula = G4_CESIUM_IODIDE
  name = G4_CESIUM_IODIDE
  specific = 4
FEATURE [App::DocumentObjectGroupPython] C_element028  label="C_element : 013"  # scripted group (container) (typed FeaturePython)
  n = 6
  ref = C_element
FEATURE [App::DocumentObjectGroupPython] H_element025  label="H_element : 013"  # scripted group (container) (typed FeaturePython)
  n = 5
  ref = H_element
FEATURE [App::DocumentObjectGroupPython] Cl_element005  label="Cl_element : 1"  # scripted group (container) (typed FeaturePython)
  n = 1
  ref = Cl_element
FEATURE [App::DocumentObjectGroupPython] G4_CHLOROBENZENE  # scripted group (container) (typed FeaturePython)
  Dunit = g/cm3
  Dvalue = 1.1058
  Group = -> [C_element028,H_element025,Cl_element005]
  conduct = 2
  density = 1
  expand = 3
  formula = G4_CHLOROBENZENE
  name = G4_CHLOROBENZENE
  specific = 4
FEATURE [App::DocumentObjectGroupPython] C_element029  label="C_element : 014"  # scripted group (container) (typed FeaturePython)
  n = 1
  ref = C_element
FEATURE [App::DocumentObjectGroupPython] H_element026  label="H_element : 1"  # scripted group (container) (typed FeaturePython)
  n = 1
  ref = H_element
FEATURE [App::DocumentObjectGroupPython] Cl_element006  label="Cl_element : 3"  # scripted group (container) (typed FeaturePython)
  n = 3
  ref = Cl_element
FEATURE [App::DocumentObjectGroupPython] G4_CHLOROFORM  # scripted group (container) (typed FeaturePython)
  Dunit = g/cm3
  Dvalue = 1.4832
  Group = -> [C_element029,H_element026,Cl_element006]
  conduct = 2
  density = 1
  expand = 3
  formula = G4_CHLOROFORM
  name = G4_CHLOROFORM
  specific = 4
FEATURE [App::DocumentObjectGroupPython] H_element027  label="H_element : 0.010"  # scripted group (container) (typed FeaturePython)
  n = 0.01
FEATURE [App::DocumentObjectGroupPython] C_element030  label="C_element : 0.001"  # scripted group (container) (typed FeaturePython)
  n = 0.001
FEATURE [App::DocumentObjectGroupPython] O_element030  label="O_element : 0.529"  # scripted group (container) (typed FeaturePython)
  n = 0.529107
FEATURE [App::DocumentObjectGroupPython] Na_element005  label="Na_element : 0.016"  # scripted group (container) (typed FeaturePython)
  n = 0.016
FEATURE [App::DocumentObjectGroupPython] Mg_element003  label="Mg_element : 0.004"  # scripted group (container) (typed FeaturePython)
  n = 0.002
FEATURE [App::DocumentObjectGroupPython] Al_element002  label="Al_element : 0.034"  # scripted group (container) (typed FeaturePython)
  n = 0.033872
FEATURE [App::DocumentObjectGroupPython] Si_element002  label="Si_element : 0.337"  # scripted group (container) (typed FeaturePython)
  n = 0.337021
FEATURE [App::DocumentObjectGroupPython] K_element003  label="K_element : 0.013"  # scripted group (container) (typed FeaturePython)
  n = 0.013
FEATURE [App::DocumentObjectGroupPython] Ca_element010  label="Ca_element : 0.044"  # scripted group (container) (typed FeaturePython)
  n = 0.044
FEATURE [App::DocumentObjectGroupPython] Fe_element002  label="Fe_element : 0.014"  # scripted group (container) (typed FeaturePython)
  n = 0.014
FEATURE [App::DocumentObjectGroupPython] G4_CONCRETE  # scripted group (container) (typed FeaturePython)
  Dunit = g/cm3
  Dvalue = 2.3
  Group = -> [H_element027,C_element030,O_element030,Na_element005,Mg_element003,Al_element002,Si_element002,K_element003,Ca_element010,Fe_element002]
  conduct = 2
  density = 1
  expand = 3
  formula = G4_CONCRETE
  name = G4_CONCRETE
  specific = 4
FEATURE [App::DocumentObjectGroupPython] C_element031  label="C_element : 015"  # scripted group (container) (typed FeaturePython)
  n = 6
  ref = C_element
FEATURE [App::DocumentObjectGroupPython] H_element028  label="H_element : 12"  # scripted group (container) (typed FeaturePython)
  n = 12
  ref = H_element
FEATURE [App::DocumentObjectGroupPython] G4_CYCLOHEXANE  # scripted group (container) (typed FeaturePython)
  Dunit = g/cm3
  Dvalue = 0.779
  Group = -> [C_element031,H_element028]
  conduct = 2
  density = 1
  expand = 3
  formula = G4_CYCLOHEXANE
  name = G4_CYCLOHEXANE
  specific = 4
FEATURE [App::DocumentObjectGroupPython] C_element032  label="C_element : 016"  # scripted group (container) (typed FeaturePython)
  n = 6
  ref = C_element
FEATURE [App::DocumentObjectGroupPython] H_element029  label="H_element : 4"  # scripted group (container) (typed FeaturePython)
  n = 4
  ref = H_element
FEATURE [App::DocumentObjectGroupPython] Cl_element007  label="Cl_element : 2"  # scripted group (container) (typed FeaturePython)
  n = 2
  ref = Cl_element
FEATURE [App::DocumentObjectGroupPython] G4_1_2_DICHLOROBENZENE  label="G4_1.2-DICHLOROBENZENE"  # scripted group (container) (typed FeaturePython)
  Dunit = g/cm3
  Dvalue = 1.3048
  Group = -> [C_element032,H_element029,Cl_element007]
  conduct = 2
  density = 1
  expand = 3
  formula = G4_1.2-DICHLOROBENZENE
  name = G4_1.2-DICHLOROBENZENE
  specific = 4
FEATURE [App::DocumentObjectGroupPython] C_element033  label="C_element : 017"  # scripted group (container) (typed FeaturePython)
  n = 4
  ref = C_element
FEATURE [App::DocumentObjectGroupPython] H_element030  label="H_element : 8"  # scripted group (container) (typed FeaturePython)
  n = 8
  ref = H_element
FEATURE [App::DocumentObjectGroupPython] O_element031  label="O_element : 014"  # scripted group (container) (typed FeaturePython)
  n = 1
  ref = O_element
FEATURE [App::DocumentObjectGroupPython] Cl_element008  label="Cl_element : 005"  # scripted group (container) (typed FeaturePython)
  n = 2
  ref = Cl_element
FEATURE [App::DocumentObjectGroupPython] G4_DICHLORODIETHYL_ETHER  # scripted group (container) (typed FeaturePython)
  Dunit = g/cm3
  Dvalue = 1.2199
  Group = -> [C_element033,H_element030,O_element031,Cl_element008]
  conduct = 2
  density = 1
  expand = 3
  formula = G4_DICHLORODIETHYL_ETHER
  name = G4_DICHLORODIETHYL_ETHER
  specific = 4
FEATURE [App::DocumentObjectGroupPython] C_element034  label="C_element : 018"  # scripted group (container) (typed FeaturePython)
  n = 2
  ref = C_element
FEATURE [App::DocumentObjectGroupPython] H_element031  label="H_element : 014"  # scripted group (container) (typed FeaturePython)
  n = 4
  ref = H_element
FEATURE [App::DocumentObjectGroupPython] Cl_element009  label="Cl_element : 006"  # scripted group (container) (typed FeaturePython)
  n = 2
  ref = Cl_element
FEATURE [App::DocumentObjectGroupPython] G4_1_2_DICHLOROETHANE  label="G4_1.2-DICHLOROETHANE"  # scripted group (container) (typed FeaturePython)
  Dunit = g/cm3
  Dvalue = 1.2351
  Group = -> [C_element034,H_element031,Cl_element009]
  conduct = 2
  density = 1
  expand = 3
  formula = G4_1.2-DICHLOROETHANE
  name = G4_1.2-DICHLOROETHANE
  specific = 4
FEATURE [App::DocumentObjectGroupPython] C_element035  label="C_element : 019"  # scripted group (container) (typed FeaturePython)
  n = 4
  ref = C_element
FEATURE [App::DocumentObjectGroupPython] H_element032  label="H_element : 015"  # scripted group (container) (typed FeaturePython)
  n = 10
  ref = H_element
FEATURE [App::DocumentObjectGroupPython] O_element032  label="O_element : 015"  # scripted group (container) (typed FeaturePython)
  n = 1
  ref = O_element
FEATURE [App::DocumentObjectGroupPython] G4_DIETHYL_ETHER  # scripted group (container) (typed FeaturePython)
  Dunit = g/cm3
  Dvalue = 0.71378
  Group = -> [C_element035,H_element032,O_element032]
  conduct = 2
  density = 1
  expand = 3
  formula = G4_DIETHYL_ETHER
  name = G4_DIETHYL_ETHER
  specific = 4
FEATURE [App::DocumentObjectGroupPython] C_element036  label="C_element : 020"  # scripted group (container) (typed FeaturePython)
  n = 3
  ref = C_element
FEATURE [App::DocumentObjectGroupPython] H_element033  label="H_element : 016"  # scripted group (container) (typed FeaturePython)
  n = 7
  ref = H_element
FEATURE [App::DocumentObjectGroupPython] N_element015  label="N_element : 008"  # scripted group (container) (typed FeaturePython)
  n = 1
  ref = N_element
FEATURE [App::DocumentObjectGroupPython] O_element033  label="O_element : 016"  # scripted group (container) (typed FeaturePython)
  n = 1
  ref = O_element
FEATURE [App::DocumentObjectGroupPython] G4_N_N_DIMETHYL_FORMAMIDE  label="G4_N.N-DIMETHYL_FORMAMIDE"  # scripted group (container) (typed FeaturePython)
  Dunit = g/cm3
  Dvalue = 0.9487
  Group = -> [C_element036,H_element033,N_element015,O_element033]
  conduct = 2
  density = 1
  expand = 3
  formula = G4_N.N-DIMETHYL_FORMAMIDE
  name = G4_N.N-DIMETHYL_FORMAMIDE
  specific = 4
FEATURE [App::DocumentObjectGroupPython] C_element037  label="C_element : 021"  # scripted group (container) (typed FeaturePython)
  n = 2
  ref = C_element
FEATURE [App::DocumentObjectGroupPython] H_element034  label="H_element : 017"  # scripted group (container) (typed FeaturePython)
  n = 6
  ref = H_element
FEATURE [App::DocumentObjectGroupPython] O_element034  label="O_element : 017"  # scripted group (container) (typed FeaturePython)
  n = 1
  ref = O_element
FEATURE [App::DocumentObjectGroupPython] S_element009  label="S_element : 003"  # scripted group (container) (typed FeaturePython)
  n = 1
  ref = S_element
FEATURE [App::DocumentObjectGroupPython] G4_DIMETHYL_SULFOXIDE  # scripted group (container) (typed FeaturePython)
  Dunit = g/cm3
  Dvalue = 1.1014
  Group = -> [C_element037,H_element034,O_element034,S_element009]
  conduct = 2
  density = 1
  expand = 3
  formula = G4_DIMETHYL_SULFOXIDE
  name = G4_DIMETHYL_SULFOXIDE
  specific = 4
FEATURE [App::DocumentObjectGroupPython] C_element038  label="C_element : 022"  # scripted group (container) (typed FeaturePython)
  n = 2
  ref = C_element
FEATURE [App::DocumentObjectGroupPython] H_element035  label="H_element : 018"  # scripted group (container) (typed FeaturePython)
  n = 6
  ref = H_element
FEATURE [App::DocumentObjectGroupPython] G4_ETHANE  # scripted group (container) (typed FeaturePython)
  Dunit = g/cm3
  Dvalue = 0.00125324
  Group = -> [C_element038,H_element035]
  conduct = 2
  density = 1
  expand = 3
  formula = G4_ETHANE
  name = G4_ETHANE
  specific = 4
FEATURE [App::DocumentObjectGroupPython] C_element039  label="C_element : 023"  # scripted group (container) (typed FeaturePython)
  n = 2
  ref = C_element
FEATURE [App::DocumentObjectGroupPython] H_element036  label="H_element : 019"  # scripted group (container) (typed FeaturePython)
  n = 6
  ref = H_element
FEATURE [App::DocumentObjectGroupPython] O_element035  label="O_element : 018"  # scripted group (container) (typed FeaturePython)
  n = 1
  ref = O_element
FEATURE [App::DocumentObjectGroupPython] G4_ETHYL_ALCOHOL  # scripted group (container) (typed FeaturePython)
  Dunit = g/cm3
  Dvalue = 0.7893
  Group = -> [C_element039,H_element036,O_element035]
  conduct = 2
  density = 1
  expand = 3
  formula = G4_ETHYL_ALCOHOL
  name = G4_ETHYL_ALCOHOL
  specific = 4
FEATURE [App::DocumentObjectGroupPython] H_element037  label="H_element : 0.090"  # scripted group (container) (typed FeaturePython)
  n = 0.090027
FEATURE [App::DocumentObjectGroupPython] C_element040  label="C_element : 0.585"  # scripted group (container) (typed FeaturePython)
  n = 0.585182
FEATURE [App::DocumentObjectGroupPython] O_element036  label="O_element : 0.325"  # scripted group (container) (typed FeaturePython)
  n = 0.324791
FEATURE [App::DocumentObjectGroupPython] G4_ETHYL_CELLULOSE  # scripted group (container) (typed FeaturePython)
  Dunit = g/cm3
  Dvalue = 1.13
  Group = -> [H_element037,C_element040,O_element036]
  conduct = 2
  density = 1
  expand = 3
  formula = G4_ETHYL_CELLULOSE
  name = G4_ETHYL_CELLULOSE
  specific = 4
FEATURE [App::DocumentObjectGroupPython] C_element041  label="C_element : 024"  # scripted group (container) (typed FeaturePython)
  n = 2
  ref = C_element
FEATURE [App::DocumentObjectGroupPython] H_element038  label="H_element : 020"  # scripted group (container) (typed FeaturePython)
  n = 4
  ref = H_element
FEATURE [App::DocumentObjectGroupPython] G4_ETHYLENE  # scripted group (container) (typed FeaturePython)
  Dunit = g/cm3
  Dvalue = 0.00117497
  Group = -> [C_element041,H_element038]
  conduct = 2
  density = 1
  expand = 3
  formula = G4_ETHYLENE
  name = G4_ETHYLENE
  specific = 4
FEATURE [App::DocumentObjectGroupPython] H_element039  label="H_element : 0.096"  # scripted group (container) (typed FeaturePython)
  n = 0.096
FEATURE [App::DocumentObjectGroupPython] C_element042  label="C_element : 0.195"  # scripted group (container) (typed FeaturePython)
  n = 0.195
FEATURE [App::DocumentObjectGroupPython] N_element016  label="N_element : 0.057"  # scripted group (container) (typed FeaturePython)
  n = 0.057
FEATURE [App::DocumentObjectGroupPython] O_element037  label="O_element : 0.646"  # scripted group (container) (typed FeaturePython)
  n = 0.646
FEATURE [App::DocumentObjectGroupPython] Na_element006  label="Na_element : 0.017"  # scripted group (container) (typed FeaturePython)
  n = 0.001
FEATURE [App::DocumentObjectGroupPython] P_element005  label="P_element : 0.104"  # scripted group (container) (typed FeaturePython)
  n = 0.001
FEATURE [App::DocumentObjectGroupPython] S_element010  label="S_element : 0.016"  # scripted group (container) (typed FeaturePython)
  n = 0.003
FEATURE [App::DocumentObjectGroupPython] Cl_element010  label="Cl_element : 0.005"  # scripted group (container) (typed FeaturePython)
  n = 0.001
FEATURE [App::DocumentObjectGroupPython] G4_EYE_LENS_ICRP  # scripted group (container) (typed FeaturePython)
  Dunit = g/cm3
  Dvalue = 1.07
  Group = -> [H_element039,C_element042,N_element016,O_element037,Na_element006,P_element005,S_element010,Cl_element010]
  conduct = 2
  density = 1
  expand = 3
  formula = G4_EYE_LENS_ICRP
  name = G4_EYE_LENS_ICRP
  specific = 4
FEATURE [App::DocumentObjectGroupPython] Fe_element003  label="Fe_element : 2"  # scripted group (container) (typed FeaturePython)
  n = 2
  ref = Fe_element
FEATURE [App::DocumentObjectGroupPython] O_element038  label="O_element : 019"  # scripted group (container) (typed FeaturePython)
  n = 3
  ref = O_element
FEATURE [App::DocumentObjectGroupPython] G4_FERRIC_OXIDE  # scripted group (container) (typed FeaturePython)
  Dunit = g/cm3
  Dvalue = 5.2
  Group = -> [Fe_element003,O_element038]
  conduct = 2
  density = 1
  expand = 3
  formula = G4_FERRIC_OXIDE
  name = G4_FERRIC_OXIDE
  specific = 4
FEATURE [App::DocumentObjectGroupPython] Fe_element004  label="Fe_element : 1"  # scripted group (container) (typed FeaturePython)
  n = 1
  ref = Fe_element
FEATURE [App::DocumentObjectGroupPython] B_element003  label="B_element : 1"  # scripted group (container) (typed FeaturePython)
  n = 1
  ref = B_element
FEATURE [App::DocumentObjectGroupPython] G4_FERROBORIDE  # scripted group (container) (typed FeaturePython)
  Dunit = g/cm3
  Dvalue = 7.15
  Group = -> [Fe_element004,B_element003]
  conduct = 2
  density = 1
  expand = 3
  formula = G4_FERROBORIDE
  name = G4_FERROBORIDE
  specific = 4
FEATURE [App::DocumentObjectGroupPython] Fe_element005  label="Fe_element : 003"  # scripted group (container) (typed FeaturePython)
  n = 1
  ref = Fe_element
FEATURE [App::DocumentObjectGroupPython] O_element039  label="O_element : 020"  # scripted group (container) (typed FeaturePython)
  n = 1
  ref = O_element
FEATURE [App::DocumentObjectGroupPython] G4_FERROUS_OXIDE  # scripted group (container) (typed FeaturePython)
  Dunit = g/cm3
  Dvalue = 5.7
  Group = -> [Fe_element005,O_element039]
  conduct = 2
  density = 1
  expand = 3
  formula = G4_FERROUS_OXIDE
  name = G4_FERROUS_OXIDE
  specific = 4
FEATURE [App::DocumentObjectGroupPython] H_element040  label="H_element : 0.115"  # scripted group (container) (typed FeaturePython)
  n = 0.108259
FEATURE [App::DocumentObjectGroupPython] N_element017  label="N_element : 0.000"  # scripted group (container) (typed FeaturePython)
  n = 2.7e-05
FEATURE [App::DocumentObjectGroupPython] O_element040  label="O_element : 0.879"  # scripted group (container) (typed FeaturePython)
  n = 0.878636
FEATURE [App::DocumentObjectGroupPython] Na_element007  label="Na_element : 0.000"  # scripted group (container) (typed FeaturePython)
  n = 2.2e-05
FEATURE [App::DocumentObjectGroupPython] S_element011  label="S_element : 0.013"  # scripted group (container) (typed FeaturePython)
  n = 0.012968
FEATURE [App::DocumentObjectGroupPython] Cl_element011  label="Cl_element : 0.000"  # scripted group (container) (typed FeaturePython)
  n = 3.4e-05
FEATURE [App::DocumentObjectGroupPython] Fe_element006  label="Fe_element : 0.000"  # scripted group (container) (typed FeaturePython)
  n = 5.4e-05
FEATURE [App::DocumentObjectGroupPython] G4_FERROUS_SULFATE  # scripted group (container) (typed FeaturePython)
  Dunit = g/cm3
  Dvalue = 1.024
  Group = -> [H_element040,N_element017,O_element040,Na_element007,S_element011,Cl_element011,Fe_element006]
  conduct = 2
  density = 1
  expand = 3
  formula = G4_FERROUS_SULFATE
  name = G4_FERROUS_SULFATE
  specific = 4
FEATURE [App::DocumentObjectGroupPython] C_element043  label="C_element : 0.099"  # scripted group (container) (typed FeaturePython)
  n = 0.099335
FEATURE [App::DocumentObjectGroupPython] F_element007  label="F_element : 0.314"  # scripted group (container) (typed FeaturePython)
  n = 0.314247
FEATURE [App::DocumentObjectGroupPython] Cl_element012  label="Cl_element : 0.586"  # scripted group (container) (typed FeaturePython)
  n = 0.586418
FEATURE [App::DocumentObjectGroupPython] G4_FREON_12  label="G4_FREON-12"  # scripted group (container) (typed FeaturePython)
  Dunit = g/cm3
  Dvalue = 1.12
  Group = -> [C_element043,F_element007,Cl_element012]
  conduct = 2
  density = 1
  expand = 3
  formula = G4_FREON-12
  name = G4_FREON-12
  specific = 4
FEATURE [App::DocumentObjectGroupPython] C_element044  label="C_element : 0.057"  # scripted group (container) (typed FeaturePython)
  n = 0.057245
FEATURE [App::DocumentObjectGroupPython] F_element008  label="F_element : 0.181"  # scripted group (container) (typed FeaturePython)
  n = 0.181096
FEATURE [App::DocumentObjectGroupPython] Br_element001  label="Br_element : 0.762"  # scripted group (container) (typed FeaturePython)
  n = 0.761659
FEATURE [App::DocumentObjectGroupPython] G4_FREON_12B2  label="G4_FREON-12B2"  # scripted group (container) (typed FeaturePython)
  Dunit = g/cm3
  Dvalue = 1.8
  Group = -> [C_element044,F_element008,Br_element001]
  conduct = 2
  density = 1
  expand = 3
  formula = G4_FREON-12B2
  name = G4_FREON-12B2
  specific = 4
FEATURE [App::DocumentObjectGroupPython] C_element045  label="C_element : 0.115"  # scripted group (container) (typed FeaturePython)
  n = 0.114983
FEATURE [App::DocumentObjectGroupPython] F_element009  label="F_element : 0.546"  # scripted group (container) (typed FeaturePython)
  n = 0.545621
FEATURE [App::DocumentObjectGroupPython] Cl_element013  label="Cl_element : 0.339"  # scripted group (container) (typed FeaturePython)
  n = 0.339396
FEATURE [App::DocumentObjectGroupPython] G4_FREON_13  label="G4_FREON-13"  # scripted group (container) (typed FeaturePython)
  Dunit = g/cm3
  Dvalue = 0.95
  Group = -> [C_element045,F_element009,Cl_element013]
  conduct = 2
  density = 1
  expand = 3
  formula = G4_FREON-13
  name = G4_FREON-13
  specific = 4
FEATURE [App::DocumentObjectGroupPython] C_element046  label="C_element : 025"  # scripted group (container) (typed FeaturePython)
  n = 1
  ref = C_element
FEATURE [App::DocumentObjectGroupPython] F_element010  label="F_element : 3"  # scripted group (container) (typed FeaturePython)
  n = 3
  ref = F_element
FEATURE [App::DocumentObjectGroupPython] Br_element002  label="Br_element : 1"  # scripted group (container) (typed FeaturePython)
  n = 1
  ref = Br_element
FEATURE [App::DocumentObjectGroupPython] G4_FREON_13B1  label="G4_FREON-13B1"  # scripted group (container) (typed FeaturePython)
  Dunit = g/cm3
  Dvalue = 1.5
  Group = -> [C_element046,F_element010,Br_element002]
  conduct = 2
  density = 1
  expand = 3
  formula = G4_FREON-13B1
  name = G4_FREON-13B1
  specific = 4
FEATURE [App::DocumentObjectGroupPython] C_element047  label="C_element : 0.061"  # scripted group (container) (typed FeaturePython)
  n = 0.061309
FEATURE [App::DocumentObjectGroupPython] F_element011  label="F_element : 0.291"  # scripted group (container) (typed FeaturePython)
  n = 0.290924
FEATURE [App::DocumentObjectGroupPython] I_element002  label="I_element : 0.648"  # scripted group (container) (typed FeaturePython)
  n = 0.647767
FEATURE [App::DocumentObjectGroupPython] G4_FREON_13I1  label="G4_FREON-13I1"  # scripted group (container) (typed FeaturePython)
  Dunit = g/cm3
  Dvalue = 1.8
  Group = -> [C_element047,F_element011,I_element002]
  conduct = 2
  density = 1
  expand = 3
  formula = G4_FREON-13I1
  name = G4_FREON-13I1
  specific = 4
FEATURE [App::DocumentObjectGroupPython] Gd_element001  label="Gd_element : 2"  # scripted group (container) (typed FeaturePython)
  n = 2
  ref = Gd_element
FEATURE [App::DocumentObjectGroupPython] O_element041  label="O_element : 021"  # scripted group (container) (typed FeaturePython)
  n = 2
  ref = O_element
FEATURE [App::DocumentObjectGroupPython] S_element012  label="S_element : 004"  # scripted group (container) (typed FeaturePython)
  n = 1
  ref = S_element
FEATURE [App::DocumentObjectGroupPython] G4_GADOLINIUM_OXYSULFIDE  # scripted group (container) (typed FeaturePython)
  Dunit = g/cm3
  Dvalue = 7.44
  Group = -> [Gd_element001,O_element041,S_element012]
  conduct = 2
  density = 1
  expand = 3
  formula = G4_GADOLINIUM_OXYSULFIDE
  name = G4_GADOLINIUM_OXYSULFIDE
  specific = 4
FEATURE [App::DocumentObjectGroupPython] Ga_element001  label="Ga_element : 1"  # scripted group (container) (typed FeaturePython)
  n = 1
  ref = Ga_element
FEATURE [App::DocumentObjectGroupPython] As_element001  label="As_element : 1"  # scripted group (container) (typed FeaturePython)
  n = 1
  ref = As_element
FEATURE [App::DocumentObjectGroupPython] G4_GALLIUM_ARSENIDE  # scripted group (container) (typed FeaturePython)
  Dunit = g/cm3
  Dvalue = 5.31
  Group = -> [Ga_element001,As_element001]
  conduct = 2
  density = 1
  expand = 3
  formula = G4_GALLIUM_ARSENIDE
  name = G4_GALLIUM_ARSENIDE
  specific = 4
FEATURE [App::DocumentObjectGroupPython] H_element041  label="H_element : 0.081"  # scripted group (container) (typed FeaturePython)
  n = 0.08118
FEATURE [App::DocumentObjectGroupPython] C_element048  label="C_element : 0.416"  # scripted group (container) (typed FeaturePython)
  n = 0.41606
FEATURE [App::DocumentObjectGroupPython] N_element018  label="N_element : 0.111"  # scripted group (container) (typed FeaturePython)
  n = 0.11124
FEATURE [App::DocumentObjectGroupPython] O_element042  label="O_element : 0.381"  # scripted group (container) (typed FeaturePython)
  n = 0.38064
FEATURE [App::DocumentObjectGroupPython] S_element013  label="S_element : 0.011"  # scripted group (container) (typed FeaturePython)
  n = 0.01088
FEATURE [App::DocumentObjectGroupPython] G4_GEL_PHOTO_EMULSION  # scripted group (container) (typed FeaturePython)
  Dunit = g/cm3
  Dvalue = 1.2914
  Group = -> [H_element041,C_element048,N_element018,O_element042,S_element013]
  conduct = 2
  density = 1
  expand = 3
  formula = G4_GEL_PHOTO_EMULSION
  name = G4_GEL_PHOTO_EMULSION
  specific = 4
FEATURE [App::DocumentObjectGroupPython] B_element004  label="B_element : 0.040"  # scripted group (container) (typed FeaturePython)
  n = 0.0400639
FEATURE [App::DocumentObjectGroupPython] O_element043  label="O_element : 0.540"  # scripted group (container) (typed FeaturePython)
  n = 0.539561
FEATURE [App::DocumentObjectGroupPython] Na_element008  label="Na_element : 0.028"  # scripted group (container) (typed FeaturePython)
  n = 0.0281909
FEATURE [App::DocumentObjectGroupPython] Al_element003  label="Al_element : 0.012"  # scripted group (container) (typed FeaturePython)
  n = 0.011644
FEATURE [App::DocumentObjectGroupPython] Si_element003  label="Si_element : 0.377"  # scripted group (container) (typed FeaturePython)
  n = 0.377219
FEATURE [App::DocumentObjectGroupPython] K_element004  label="K_element : 0.014"  # scripted group (container) (typed FeaturePython)
  n = 0.00332099
FEATURE [App::DocumentObjectGroupPython] G4_Pyrex_Glass  # scripted group (container) (typed FeaturePython)
  Dunit = g/cm3
  Dvalue = 2.23
  Group = -> [B_element004,O_element043,Na_element008,Al_element003,Si_element003,K_element004]
  conduct = 2
  density = 1
  expand = 3
  formula = G4_Pyrex_Glass
  name = G4_Pyrex_Glass
  specific = 4
FEATURE [App::DocumentObjectGroupPython] O_element044  label="O_element : 0.156"  # scripted group (container) (typed FeaturePython)
  n = 0.156453
FEATURE [App::DocumentObjectGroupPython] Si_element004  label="Si_element : 0.081"  # scripted group (container) (typed FeaturePython)
  n = 0.080866
FEATURE [App::DocumentObjectGroupPython] Ti_element001  label="Ti_element : 0.008"  # scripted group (container) (typed FeaturePython)
  n = 0.008092
FEATURE [App::DocumentObjectGroupPython] As_element002  label="As_element : 0.003"  # scripted group (container) (typed FeaturePython)
  n = 0.002651
FEATURE [App::DocumentObjectGroupPython] Pb_element001  label="Pb_element : 0.752"  # scripted group (container) (typed FeaturePython)
  n = 0.751938
FEATURE [App::DocumentObjectGroupPython] G4_GLASS_LEAD  # scripted group (container) (typed FeaturePython)
  Dunit = g/cm3
  Dvalue = 6.22
  Group = -> [O_element044,Si_element004,Ti_element001,As_element002,Pb_element001]
  conduct = 2
  density = 1
  expand = 3
  formula = G4_GLASS_LEAD
  name = G4_GLASS_LEAD
  specific = 4
FEATURE [App::DocumentObjectGroupPython] O_element045  label="O_element : 0.460"  # scripted group (container) (typed FeaturePython)
  n = 0.4598
FEATURE [App::DocumentObjectGroupPython] Na_element009  label="Na_element : 0.096"  # scripted group (container) (typed FeaturePython)
  n = 0.0964411
FEATURE [App::DocumentObjectGroupPython] Si_element005  label="Si_element : 0.378"  # scripted group (container) (typed FeaturePython)
  n = 0.336553
FEATURE [App::DocumentObjectGroupPython] Ca_element011  label="Ca_element : 0.107"  # scripted group (container) (typed FeaturePython)
  n = 0.107205
FEATURE [App::DocumentObjectGroupPython] G4_GLASS_PLATE  # scripted group (container) (typed FeaturePython)
  Dunit = g/cm3
  Dvalue = 2.4
  Group = -> [O_element045,Na_element009,Si_element005,Ca_element011]
  conduct = 2
  density = 1
  expand = 3
  formula = G4_GLASS_PLATE
  name = G4_GLASS_PLATE
  specific = 4
FEATURE [App::DocumentObjectGroupPython] C_element049  label="C_element : 026"  # scripted group (container) (typed FeaturePython)
  n = 5
  ref = C_element
FEATURE [App::DocumentObjectGroupPython] H_element042  label="H_element : 021"  # scripted group (container) (typed FeaturePython)
  n = 10
  ref = H_element
FEATURE [App::DocumentObjectGroupPython] N_element019  label="N_element : 2"  # scripted group (container) (typed FeaturePython)
  n = 2
  ref = N_element
FEATURE [App::DocumentObjectGroupPython] O_element046  label="O_element : 022"  # scripted group (container) (typed FeaturePython)
  n = 3
  ref = O_element
FEATURE [App::DocumentObjectGroupPython] G4_GLUTAMINE  # scripted group (container) (typed FeaturePython)
  Dunit = g/cm3
  Dvalue = 1.46
  Group = -> [C_element049,H_element042,N_element019,O_element046]
  conduct = 2
  density = 1
  expand = 3
  formula = G4_GLUTAMINE
  name = G4_GLUTAMINE
  specific = 4
FEATURE [App::DocumentObjectGroupPython] C_element050  label="C_element : 027"  # scripted group (container) (typed FeaturePython)
  n = 3
  ref = C_element
FEATURE [App::DocumentObjectGroupPython] H_element043  label="H_element : 022"  # scripted group (container) (typed FeaturePython)
  n = 8
  ref = H_element
FEATURE [App::DocumentObjectGroupPython] O_element047  label="O_element : 023"  # scripted group (container) (typed FeaturePython)
  n = 3
  ref = O_element
FEATURE [App::DocumentObjectGroupPython] G4_GLYCEROL  # scripted group (container) (typed FeaturePython)
  Dunit = g/cm3
  Dvalue = 1.2613
  Group = -> [C_element050,H_element043,O_element047]
  conduct = 2
  density = 1
  expand = 3
  formula = G4_GLYCEROL
  name = G4_GLYCEROL
  specific = 4
FEATURE [App::DocumentObjectGroupPython] C_element051  label="C_element : 028"  # scripted group (container) (typed FeaturePython)
  n = 5
  ref = C_element
FEATURE [App::DocumentObjectGroupPython] H_element044  label="H_element : 023"  # scripted group (container) (typed FeaturePython)
  n = 5
  ref = H_element
FEATURE [App::DocumentObjectGroupPython] N_element020  label="N_element : 009"  # scripted group (container) (typed FeaturePython)
  n = 5
  ref = N_element
FEATURE [App::DocumentObjectGroupPython] O_element048  label="O_element : 024"  # scripted group (container) (typed FeaturePython)
  n = 1
  ref = O_element
FEATURE [App::DocumentObjectGroupPython] G4_GUANINE  # scripted group (container) (typed FeaturePython)
  Dunit = g/cm3
  Dvalue = 2.2
  Group = -> [C_element051,H_element044,N_element020,O_element048]
  conduct = 2
  density = 1
  expand = 3
  formula = G4_GUANINE
  name = G4_GUANINE
  specific = 4
FEATURE [App::DocumentObjectGroupPython] Ca_element012  label="Ca_element : 006"  # scripted group (container) (typed FeaturePython)
  n = 1
  ref = Ca_element
FEATURE [App::DocumentObjectGroupPython] S_element014  label="S_element : 005"  # scripted group (container) (typed FeaturePython)
  n = 1
  ref = S_element
FEATURE [App::DocumentObjectGroupPython] O_element049  label="O_element : 6"  # scripted group (container) (typed FeaturePython)
  n = 6
  ref = O_element
FEATURE [App::DocumentObjectGroupPython] H_element045  label="H_element : 024"  # scripted group (container) (typed FeaturePython)
  n = 4
  ref = H_element
FEATURE [App::DocumentObjectGroupPython] G4_GYPSUM  # scripted group (container) (typed FeaturePython)
  Dunit = g/cm3
  Dvalue = 2.32
  Group = -> [Ca_element012,S_element014,O_element049,H_element045]
  conduct = 2
  density = 1
  expand = 3
  formula = G4_GYPSUM
  name = G4_GYPSUM
  specific = 4
FEATURE [App::DocumentObjectGroupPython] C_element052  label="C_element : 7"  # scripted group (container) (typed FeaturePython)
  n = 7
  ref = C_element
FEATURE [App::DocumentObjectGroupPython] H_element046  label="H_element : 16"  # scripted group (container) (typed FeaturePython)
  n = 16
  ref = H_element
FEATURE [App::DocumentObjectGroupPython] G4_N_HEPTANE  label="G4_N-HEPTANE"  # scripted group (container) (typed FeaturePython)
  Dunit = g/cm3
  Dvalue = 0.68376
  Group = -> [C_element052,H_element046]
  conduct = 2
  density = 1
  expand = 3
  formula = G4_N-HEPTANE
  name = G4_N-HEPTANE
  specific = 4
FEATURE [App::DocumentObjectGroupPython] C_element053  label="C_element : 029"  # scripted group (container) (typed FeaturePython)
  n = 6
  ref = C_element
FEATURE [App::DocumentObjectGroupPython] H_element047  label="H_element : 14"  # scripted group (container) (typed FeaturePython)
  n = 14
  ref = H_element
FEATURE [App::DocumentObjectGroupPython] G4_N_HEXANE  label="G4_N-HEXANE"  # scripted group (container) (typed FeaturePython)
  Dunit = g/cm3
  Dvalue = 0.6603
  Group = -> [C_element053,H_element047]
  conduct = 2
  density = 1
  expand = 3
  formula = G4_N-HEXANE
  name = G4_N-HEXANE
  specific = 4
FEATURE [App::DocumentObjectGroupPython] C_element054  label="C_element : 22"  # scripted group (container) (typed FeaturePython)
  n = 22
  ref = C_element
FEATURE [App::DocumentObjectGroupPython] H_element048  label="H_element : 025"  # scripted group (container) (typed FeaturePython)
  n = 10
  ref = H_element
FEATURE [App::DocumentObjectGroupPython] N_element021  label="N_element : 010"  # scripted group (container) (typed FeaturePython)
  n = 2
  ref = N_element
FEATURE [App::DocumentObjectGroupPython] O_element050  label="O_element : 025"  # scripted group (container) (typed FeaturePython)
  n = 5
  ref = O_element
FEATURE [App::DocumentObjectGroupPython] G4_KAPTON  # scripted group (container) (typed FeaturePython)
  Dunit = g/cm3
  Dvalue = 1.42
  Group = -> [C_element054,H_element048,N_element021,O_element050]
  conduct = 2
  density = 1
  expand = 3
  formula = G4_KAPTON
  name = G4_KAPTON
  specific = 4
FEATURE [App::DocumentObjectGroupPython] La_element001  label="La_element : 1"  # scripted group (container) (typed FeaturePython)
  n = 1
  ref = La_element
FEATURE [App::DocumentObjectGroupPython] Br_element003  label="Br_element : 002"  # scripted group (container) (typed FeaturePython)
  n = 1
  ref = Br_element
FEATURE [App::DocumentObjectGroupPython] O_element051  label="O_element : 026"  # scripted group (container) (typed FeaturePython)
  n = 1
  ref = O_element
FEATURE [App::DocumentObjectGroupPython] G4_LANTHANUM_OXYBROMIDE  # scripted group (container) (typed FeaturePython)
  Dunit = g/cm3
  Dvalue = 6.28
  Group = -> [La_element001,Br_element003,O_element051]
  conduct = 2
  density = 1
  expand = 3
  formula = G4_LANTHANUM_OXYBROMIDE
  name = G4_LANTHANUM_OXYBROMIDE
  specific = 4
FEATURE [App::DocumentObjectGroupPython] La_element002  label="La_element : 2"  # scripted group (container) (typed FeaturePython)
  n = 2
  ref = La_element
FEATURE [App::DocumentObjectGroupPython] O_element052  label="O_element : 027"  # scripted group (container) (typed FeaturePython)
  n = 2
  ref = O_element
FEATURE [App::DocumentObjectGroupPython] S_element015  label="S_element : 006"  # scripted group (container) (typed FeaturePython)
  n = 1
  ref = S_element
FEATURE [App::DocumentObjectGroupPython] G4_LANTHANUM_OXYSULFIDE  # scripted group (container) (typed FeaturePython)
  Dunit = g/cm3
  Dvalue = 5.86
  Group = -> [La_element002,O_element052,S_element015]
  conduct = 2
  density = 1
  expand = 3
  formula = G4_LANTHANUM_OXYSULFIDE
  name = G4_LANTHANUM_OXYSULFIDE
  specific = 4
FEATURE [App::DocumentObjectGroupPython] O_element053  label="O_element : 0.072"  # scripted group (container) (typed FeaturePython)
  n = 0.071682
FEATURE [App::DocumentObjectGroupPython] Pb_element002  label="Pb_element : 0.928"  # scripted group (container) (typed FeaturePython)
  n = 0.928318
FEATURE [App::DocumentObjectGroupPython] G4_LEAD_OXIDE  # scripted group (container) (typed FeaturePython)
  Dunit = g/cm3
  Dvalue = 9.53
  Group = -> [O_element053,Pb_element002]
  conduct = 2
  density = 1
  expand = 3
  formula = G4_LEAD_OXIDE
  name = G4_LEAD_OXIDE
  specific = 4
FEATURE [App::DocumentObjectGroupPython] Li_element001  label="Li_element : 1"  # scripted group (container) (typed FeaturePython)
  n = 1
  ref = Li_element
FEATURE [App::DocumentObjectGroupPython] N_element022  label="N_element : 011"  # scripted group (container) (typed FeaturePython)
  n = 1
  ref = N_element
FEATURE [App::DocumentObjectGroupPython] H_element049  label="H_element : 026"  # scripted group (container) (typed FeaturePython)
  n = 2
  ref = H_element
FEATURE [App::DocumentObjectGroupPython] G4_LITHIUM_AMIDE  # scripted group (container) (typed FeaturePython)
  Dunit = g/cm3
  Dvalue = 1.178
  Group = -> [Li_element001,N_element022,H_element049]
  conduct = 2
  density = 1
  expand = 3
  formula = G4_LITHIUM_AMIDE
  name = G4_LITHIUM_AMIDE
  specific = 4
FEATURE [App::DocumentObjectGroupPython] Li_element002  label="Li_element : 2"  # scripted group (container) (typed FeaturePython)
  n = 2
  ref = Li_element
FEATURE [App::DocumentObjectGroupPython] C_element055  label="C_element : 030"  # scripted group (container) (typed FeaturePython)
  n = 1
  ref = C_element
FEATURE [App::DocumentObjectGroupPython] O_element054  label="O_element : 028"  # scripted group (container) (typed FeaturePython)
  n = 3
  ref = O_element
FEATURE [App::DocumentObjectGroupPython] G4_LITHIUM_CARBONATE  # scripted group (container) (typed FeaturePython)
  Dunit = g/cm3
  Dvalue = 2.11
  Group = -> [Li_element002,C_element055,O_element054]
  conduct = 2
  density = 1
  expand = 3
  formula = G4_LITHIUM_CARBONATE
  name = G4_LITHIUM_CARBONATE
  specific = 4
FEATURE [App::DocumentObjectGroupPython] Li_element003  label="Li_element : 003"  # scripted group (container) (typed FeaturePython)
  n = 1
  ref = Li_element
FEATURE [App::DocumentObjectGroupPython] F_element012  label="F_element : 004"  # scripted group (container) (typed FeaturePython)
  n = 1
  ref = F_element
FEATURE [App::DocumentObjectGroupPython] G4_LITHIUM_FLUORIDE  # scripted group (container) (typed FeaturePython)
  Dunit = g/cm3
  Dvalue = 2.635
  Group = -> [Li_element003,F_element012]
  conduct = 2
  density = 1
  expand = 3
  formula = G4_LITHIUM_FLUORIDE
  name = G4_LITHIUM_FLUORIDE
  specific = 4
FEATURE [App::DocumentObjectGroupPython] Li_element004  label="Li_element : 004"  # scripted group (container) (typed FeaturePython)
  n = 1
  ref = Li_element
FEATURE [App::DocumentObjectGroupPython] H_element050  label="H_element : 027"  # scripted group (container) (typed FeaturePython)
  n = 1
  ref = H_element
FEATURE [App::DocumentObjectGroupPython] G4_LITHIUM_HYDRIDE  # scripted group (container) (typed FeaturePython)
  Dunit = g/cm3
  Dvalue = 0.82
  Group = -> [Li_element004,H_element050]
  conduct = 2
  density = 1
  expand = 3
  formula = G4_LITHIUM_HYDRIDE
  name = G4_LITHIUM_HYDRIDE
  specific = 4
FEATURE [App::DocumentObjectGroupPython] Li_element005  label="Li_element : 005"  # scripted group (container) (typed FeaturePython)
  n = 1
  ref = Li_element
FEATURE [App::DocumentObjectGroupPython] I_element003  label="I_element : 002"  # scripted group (container) (typed FeaturePython)
  n = 1
  ref = I_element
FEATURE [App::DocumentObjectGroupPython] G4_LITHIUM_IODIDE  # scripted group (container) (typed FeaturePython)
  Dunit = g/cm3
  Dvalue = 3.494
  Group = -> [Li_element005,I_element003]
  conduct = 2
  density = 1
  expand = 3
  formula = G4_LITHIUM_IODIDE
  name = G4_LITHIUM_IODIDE
  specific = 4
FEATURE [App::DocumentObjectGroupPython] Li_element006  label="Li_element : 006"  # scripted group (container) (typed FeaturePython)
  n = 2
  ref = Li_element
FEATURE [App::DocumentObjectGroupPython] O_element055  label="O_element : 029"  # scripted group (container) (typed FeaturePython)
  n = 1
  ref = O_element
FEATURE [App::DocumentObjectGroupPython] G4_LITHIUM_OXIDE  # scripted group (container) (typed FeaturePython)
  Dunit = g/cm3
  Dvalue = 2.013
  Group = -> [Li_element006,O_element055]
  conduct = 2
  density = 1
  expand = 3
  formula = G4_LITHIUM_OXIDE
  name = G4_LITHIUM_OXIDE
  specific = 4
FEATURE [App::DocumentObjectGroupPython] Li_element007  label="Li_element : 007"  # scripted group (container) (typed FeaturePython)
  n = 2
  ref = Li_element
FEATURE [App::DocumentObjectGroupPython] B_element005  label="B_element : 005"  # scripted group (container) (typed FeaturePython)
  n = 4
  ref = B_element
FEATURE [App::DocumentObjectGroupPython] O_element056  label="O_element : 7"  # scripted group (container) (typed FeaturePython)
  n = 7
  ref = O_element
FEATURE [App::DocumentObjectGroupPython] G4_LITHIUM_TETRABORATE  # scripted group (container) (typed FeaturePython)
  Dunit = g/cm3
  Dvalue = 2.44
  Group = -> [Li_element007,B_element005,O_element056]
  conduct = 2
  density = 1
  expand = 3
  formula = G4_LITHIUM_TETRABORATE
  name = G4_LITHIUM_TETRABORATE
  specific = 4
FEATURE [App::DocumentObjectGroupPython] H_element051  label="H_element : 0.105"  # scripted group (container) (typed FeaturePython)
  n = 0.105
FEATURE [App::DocumentObjectGroupPython] C_element056  label="C_element : 0.083"  # scripted group (container) (typed FeaturePython)
  n = 0.083
FEATURE [App::DocumentObjectGroupPython] N_element023  label="N_element : 0.023"  # scripted group (container) (typed FeaturePython)
  n = 0.023
FEATURE [App::DocumentObjectGroupPython] O_element057  label="O_element : 0.779"  # scripted group (container) (typed FeaturePython)
  n = 0.779
FEATURE [App::DocumentObjectGroupPython] Na_element010  label="Na_element : 0.097"  # scripted group (container) (typed FeaturePython)
  n = 0.002
FEATURE [App::DocumentObjectGroupPython] P_element006  label="P_element : 0.105"  # scripted group (container) (typed FeaturePython)
  n = 0.001
FEATURE [App::DocumentObjectGroupPython] S_element016  label="S_element : 0.017"  # scripted group (container) (typed FeaturePython)
  n = 0.002
FEATURE [App::DocumentObjectGroupPython] Cl_element014  label="Cl_element : 0.587"  # scripted group (container) (typed FeaturePython)
  n = 0.003
FEATURE [App::DocumentObjectGroupPython] K_element005  label="K_element : 0.015"  # scripted group (container) (typed FeaturePython)
  n = 0.002
FEATURE [App::DocumentObjectGroupPython] G4_LUNG_ICRP  # scripted group (container) (typed FeaturePython)
  Dunit = g/cm3
  Dvalue = 1.04
  Group = -> [H_element051,C_element056,N_element023,O_element057,Na_element010,P_element006,S_element016,Cl_element014,K_element005]
  conduct = 2
  density = 1
  expand = 3
  formula = G4_LUNG_ICRP
  name = G4_LUNG_ICRP
  specific = 4
FEATURE [App::DocumentObjectGroupPython] H_element052  label="H_element : 0.116"  # scripted group (container) (typed FeaturePython)
  n = 0.114318
FEATURE [App::DocumentObjectGroupPython] C_element057  label="C_element : 0.656"  # scripted group (container) (typed FeaturePython)
  n = 0.655824
FEATURE [App::DocumentObjectGroupPython] O_element058  label="O_element : 0.092"  # scripted group (container) (typed FeaturePython)
  n = 0.0921831
FEATURE [App::DocumentObjectGroupPython] Mg_element004  label="Mg_element : 0.135"  # scripted group (container) (typed FeaturePython)
  n = 0.134792
FEATURE [App::DocumentObjectGroupPython] Ca_element013  label="Ca_element : 0.003"  # scripted group (container) (typed FeaturePython)
  n = 0.002883
FEATURE [App::DocumentObjectGroupPython] G4_M3_WAX  # scripted group (container) (typed FeaturePython)
  Dunit = g/cm3
  Dvalue = 1.05
  Group = -> [H_element052,C_element057,O_element058,Mg_element004,Ca_element013]
  conduct = 2
  density = 1
  expand = 3
  formula = G4_M3_WAX
  name = G4_M3_WAX
  specific = 4
FEATURE [App::DocumentObjectGroupPython] Mg_element005  label="Mg_element : 1"  # scripted group (container) (typed FeaturePython)
  n = 1
  ref = Mg_element
FEATURE [App::DocumentObjectGroupPython] C_element058  label="C_element : 031"  # scripted group (container) (typed FeaturePython)
  n = 1
  ref = C_element
FEATURE [App::DocumentObjectGroupPython] O_element059  label="O_element : 030"  # scripted group (container) (typed FeaturePython)
  n = 3
  ref = O_element
FEATURE [App::DocumentObjectGroupPython] G4_MAGNESIUM_CARBONATE  # scripted group (container) (typed FeaturePython)
  Dunit = g/cm3
  Dvalue = 2.958
  Group = -> [Mg_element005,C_element058,O_element059]
  conduct = 2
  density = 1
  expand = 3
  formula = G4_MAGNESIUM_CARBONATE
  name = G4_MAGNESIUM_CARBONATE
  specific = 4
FEATURE [App::DocumentObjectGroupPython] Mg_element006  label="Mg_element : 002"  # scripted group (container) (typed FeaturePython)
  n = 1
  ref = Mg_element
FEATURE [App::DocumentObjectGroupPython] F_element013  label="F_element : 005"  # scripted group (container) (typed FeaturePython)
  n = 2
  ref = F_element
FEATURE [App::DocumentObjectGroupPython] G4_MAGNESIUM_FLUORIDE  # scripted group (container) (typed FeaturePython)
  Dunit = g/cm3
  Dvalue = 3
  Group = -> [Mg_element006,F_element013]
  conduct = 2
  density = 1
  expand = 3
  formula = G4_MAGNESIUM_FLUORIDE
  name = G4_MAGNESIUM_FLUORIDE
  specific = 4
FEATURE [App::DocumentObjectGroupPython] Mg_element007  label="Mg_element : 003"  # scripted group (container) (typed FeaturePython)
  n = 1
  ref = Mg_element
FEATURE [App::DocumentObjectGroupPython] O_element060  label="O_element : 031"  # scripted group (container) (typed FeaturePython)
  n = 1
  ref = O_element
FEATURE [App::DocumentObjectGroupPython] G4_MAGNESIUM_OXIDE  # scripted group (container) (typed FeaturePython)
  Dunit = g/cm3
  Dvalue = 3.58
  Group = -> [Mg_element007,O_element060]
  conduct = 2
  density = 1
  expand = 3
  formula = G4_MAGNESIUM_OXIDE
  name = G4_MAGNESIUM_OXIDE
  specific = 4
FEATURE [App::DocumentObjectGroupPython] Mg_element008  label="Mg_element : 004"  # scripted group (container) (typed FeaturePython)
  n = 1
  ref = Mg_element
FEATURE [App::DocumentObjectGroupPython] B_element006  label="B_element : 006"  # scripted group (container) (typed FeaturePython)
  n = 4
  ref = B_element
FEATURE [App::DocumentObjectGroupPython] O_element061  label="O_element : 032"  # scripted group (container) (typed FeaturePython)
  n = 7
  ref = O_element
FEATURE [App::DocumentObjectGroupPython] G4_MAGNESIUM_TETRABORATE  # scripted group (container) (typed FeaturePython)
  Dunit = g/cm3
  Dvalue = 2.53
  Group = -> [Mg_element008,B_element006,O_element061]
  conduct = 2
  density = 1
  expand = 3
  formula = G4_MAGNESIUM_TETRABORATE
  name = G4_MAGNESIUM_TETRABORATE
  specific = 4
FEATURE [App::DocumentObjectGroupPython] Hg_element001  label="Hg_element : 1"  # scripted group (container) (typed FeaturePython)
  n = 1
  ref = Hg_element
FEATURE [App::DocumentObjectGroupPython] I_element004  label="I_element : 2"  # scripted group (container) (typed FeaturePython)
  n = 2
  ref = I_element
FEATURE [App::DocumentObjectGroupPython] G4_MERCURIC_IODIDE  # scripted group (container) (typed FeaturePython)
  Dunit = g/cm3
  Dvalue = 6.36
  Group = -> [Hg_element001,I_element004]
  conduct = 2
  density = 1
  expand = 3
  formula = G4_MERCURIC_IODIDE
  name = G4_MERCURIC_IODIDE
  specific = 4
FEATURE [App::DocumentObjectGroupPython] C_element059  label="C_element : 032"  # scripted group (container) (typed FeaturePython)
  n = 1
  ref = C_element
FEATURE [App::DocumentObjectGroupPython] H_element053  label="H_element : 028"  # scripted group (container) (typed FeaturePython)
  n = 4
  ref = H_element
FEATURE [App::DocumentObjectGroupPython] G4_METHANE  # scripted group (container) (typed FeaturePython)
  Dunit = g/cm3
  Dvalue = 0.000667151
  Group = -> [C_element059,H_element053]
  conduct = 2
  density = 1
  expand = 3
  formula = G4_METHANE
  name = G4_METHANE
  specific = 4
FEATURE [App::DocumentObjectGroupPython] C_element060  label="C_element : 033"  # scripted group (container) (typed FeaturePython)
  n = 1
  ref = C_element
FEATURE [App::DocumentObjectGroupPython] H_element054  label="H_element : 029"  # scripted group (container) (typed FeaturePython)
  n = 4
  ref = H_element
FEATURE [App::DocumentObjectGroupPython] O_element062  label="O_element : 033"  # scripted group (container) (typed FeaturePython)
  n = 1
  ref = O_element
FEATURE [App::DocumentObjectGroupPython] G4_METHANOL  # scripted group (container) (typed FeaturePython)
  Dunit = g/cm3
  Dvalue = 0.7914
  Group = -> [C_element060,H_element054,O_element062]
  conduct = 2
  density = 1
  expand = 3
  formula = G4_METHANOL
  name = G4_METHANOL
  specific = 4
FEATURE [App::DocumentObjectGroupPython] H_element055  label="H_element : 0.134"  # scripted group (container) (typed FeaturePython)
  n = 0.13404
FEATURE [App::DocumentObjectGroupPython] C_element061  label="C_element : 0.778"  # scripted group (container) (typed FeaturePython)
  n = 0.77796
FEATURE [App::DocumentObjectGroupPython] O_element063  label="O_element : 0.035"  # scripted group (container) (typed FeaturePython)
  n = 0.03502
FEATURE [App::DocumentObjectGroupPython] Mg_element009  label="Mg_element : 0.039"  # scripted group (container) (typed FeaturePython)
  n = 0.038594
FEATURE [App::DocumentObjectGroupPython] Ti_element002  label="Ti_element : 0.014"  # scripted group (container) (typed FeaturePython)
  n = 0.014386
FEATURE [App::DocumentObjectGroupPython] G4_MIX_D_WAX  # scripted group (container) (typed FeaturePython)
  Dunit = g/cm3
  Dvalue = 0.99
  Group = -> [H_element055,C_element061,O_element063,Mg_element009,Ti_element002]
  conduct = 2
  density = 1
  expand = 3
  formula = G4_MIX_D_WAX
  name = G4_MIX_D_WAX
  specific = 4
FEATURE [App::DocumentObjectGroupPython] H_element056  label="H_element : 0.135"  # scripted group (container) (typed FeaturePython)
  n = 0.081192
FEATURE [App::DocumentObjectGroupPython] C_element062  label="C_element : 0.583"  # scripted group (container) (typed FeaturePython)
  n = 0.583442
FEATURE [App::DocumentObjectGroupPython] N_element024  label="N_element : 0.018"  # scripted group (container) (typed FeaturePython)
  n = 0.017798
FEATURE [App::DocumentObjectGroupPython] O_element064  label="O_element : 0.186"  # scripted group (container) (typed FeaturePython)
  n = 0.186381
FEATURE [App::DocumentObjectGroupPython] Mg_element010  label="Mg_element : 0.130"  # scripted group (container) (typed FeaturePython)
  n = 0.130287
FEATURE [App::DocumentObjectGroupPython] Cl_element015  label="Cl_element : 0.588"  # scripted group (container) (typed FeaturePython)
  n = 0.0009
FEATURE [App::DocumentObjectGroupPython] G4_MS20_TISSUE  # scripted group (container) (typed FeaturePython)
  Dunit = g/cm3
  Dvalue = 1
  Group = -> [H_element056,C_element062,N_element024,O_element064,Mg_element010,Cl_element015]
  conduct = 2
  density = 1
  expand = 3
  formula = G4_MS20_TISSUE
  name = G4_MS20_TISSUE
  specific = 4
FEATURE [App::DocumentObjectGroupPython] H_element057  label="H_element : 0.136"  # scripted group (container) (typed FeaturePython)
  n = 0.102
FEATURE [App::DocumentObjectGroupPython] C_element063  label="C_element : 0.143"  # scripted group (container) (typed FeaturePython)
  n = 0.143
FEATURE [App::DocumentObjectGroupPython] N_element025  label="N_element : 0.034"  # scripted group (container) (typed FeaturePython)
  n = 0.034
FEATURE [App::DocumentObjectGroupPython] O_element065  label="O_element : 0.710"  # scripted group (container) (typed FeaturePython)
  n = 0.71
FEATURE [App::DocumentObjectGroupPython] Na_element011  label="Na_element : 0.098"  # scripted group (container) (typed FeaturePython)
  n = 0.001
FEATURE [App::DocumentObjectGroupPython] P_element007  label="P_element : 0.002"  # scripted group (container) (typed FeaturePython)
  n = 0.002
FEATURE [App::DocumentObjectGroupPython] S_element017  label="S_element : 0.018"  # scripted group (container) (typed FeaturePython)
  n = 0.003
FEATURE [App::DocumentObjectGroupPython] Cl_element016  label="Cl_element : 0.589"  # scripted group (container) (typed FeaturePython)
  n = 0.001
FEATURE [App::DocumentObjectGroupPython] K_element006  label="K_element : 0.004"  # scripted group (container) (typed FeaturePython)
  n = 0.004
FEATURE [App::DocumentObjectGroupPython] G4_MUSCLE_SKELETAL_ICRP  # scripted group (container) (typed FeaturePython)
  Dunit = g/cm3
  Dvalue = 1.05
  Group = -> [H_element057,C_element063,N_element025,O_element065,Na_element011,P_element007,S_element017,Cl_element016,K_element006]
  conduct = 2
  density = 1
  expand = 3
  formula = G4_MUSCLE_SKELETAL_ICRP
  name = G4_MUSCLE_SKELETAL_ICRP
  specific = 4
FEATURE [App::DocumentObjectGroupPython] H_element058  label="H_element : 0.137"  # scripted group (container) (typed FeaturePython)
  n = 0.102102
FEATURE [App::DocumentObjectGroupPython] C_element064  label="C_element : 0.123"  # scripted group (container) (typed FeaturePython)
  n = 0.123123
FEATURE [App::DocumentObjectGroupPython] N_element026  label="N_element : 0.756"  # scripted group (container) (typed FeaturePython)
  n = 0.035035
FEATURE [App::DocumentObjectGroupPython] O_element066  label="O_element : 0.730"  # scripted group (container) (typed FeaturePython)
  n = 0.72973
FEATURE [App::DocumentObjectGroupPython] Na_element012  label="Na_element : 0.099"  # scripted group (container) (typed FeaturePython)
  n = 0.001001
FEATURE [App::DocumentObjectGroupPython] P_element008  label="P_element : 0.106"  # scripted group (container) (typed FeaturePython)
  n = 0.002002
FEATURE [App::DocumentObjectGroupPython] S_element018  label="S_element : 0.019"  # scripted group (container) (typed FeaturePython)
  n = 0.004004
FEATURE [App::DocumentObjectGroupPython] K_element007  label="K_element : 0.016"  # scripted group (container) (typed FeaturePython)
  n = 0.003003
FEATURE [App::DocumentObjectGroupPython] G4_MUSCLE_STRIATED_ICRU  # scripted group (container) (typed FeaturePython)
  Dunit = g/cm3
  Dvalue = 1.04
  Group = -> [H_element058,C_element064,N_element026,O_element066,Na_element012,P_element008,S_element018,K_element007]
  conduct = 2
  density = 1
  expand = 3
  formula = G4_MUSCLE_STRIATED_ICRU
  name = G4_MUSCLE_STRIATED_ICRU
  specific = 4
FEATURE [App::DocumentObjectGroupPython] H_element059  label="H_element : 0.098"  # scripted group (container) (typed FeaturePython)
  n = 0.0982341
FEATURE [App::DocumentObjectGroupPython] C_element065  label="C_element : 0.156"  # scripted group (container) (typed FeaturePython)
  n = 0.156214
FEATURE [App::DocumentObjectGroupPython] N_element027  label="N_element : 0.757"  # scripted group (container) (typed FeaturePython)
  n = 0.035451
FEATURE [App::DocumentObjectGroupPython] O_element067  label="O_element : 0.880"  # scripted group (container) (typed FeaturePython)
  n = 0.710101
FEATURE [App::DocumentObjectGroupPython] G4_MUSCLE_WITH_SUCROSE  # scripted group (container) (typed FeaturePython)
  Dunit = g/cm3
  Dvalue = 1.11
  Group = -> [H_element059,C_element065,N_element027,O_element067]
  conduct = 2
  density = 1
  expand = 3
  formula = G4_MUSCLE_WITH_SUCROSE
  name = G4_MUSCLE_WITH_SUCROSE
  specific = 4
FEATURE [App::DocumentObjectGroupPython] H_element060  label="H_element : 0.138"  # scripted group (container) (typed FeaturePython)
  n = 0.101969
FEATURE [App::DocumentObjectGroupPython] C_element066  label="C_element : 0.120"  # scripted group (container) (typed FeaturePython)
  n = 0.120058
FEATURE [App::DocumentObjectGroupPython] N_element028  label="N_element : 0.758"  # scripted group (container) (typed FeaturePython)
  n = 0.035451
FEATURE [App::DocumentObjectGroupPython] O_element068  label="O_element : 0.743"  # scripted group (container) (typed FeaturePython)
  n = 0.742522
FEATURE [App::DocumentObjectGroupPython] G4_MUSCLE_WITHOUT_SUCROSE  # scripted group (container) (typed FeaturePython)
  Dunit = g/cm3
  Dvalue = 1.07
  Group = -> [H_element060,C_element066,N_element028,O_element068]
  conduct = 2
  density = 1
  expand = 3
  formula = G4_MUSCLE_WITHOUT_SUCROSE
  name = G4_MUSCLE_WITHOUT_SUCROSE
  specific = 4
FEATURE [App::DocumentObjectGroupPython] C_element067  label="C_element : 10"  # scripted group (container) (typed FeaturePython)
  n = 10
  ref = C_element
FEATURE [App::DocumentObjectGroupPython] H_element061  label="H_element : 030"  # scripted group (container) (typed FeaturePython)
  n = 8
  ref = H_element
FEATURE [App::DocumentObjectGroupPython] G4_NAPHTHALENE  # scripted group (container) (typed FeaturePython)
  Dunit = g/cm3
  Dvalue = 1.145
  Group = -> [C_element067,H_element061]
  conduct = 2
  density = 1
  expand = 3
  formula = G4_NAPHTHALENE
  name = G4_NAPHTHALENE
  specific = 4
FEATURE [App::DocumentObjectGroupPython] C_element068  label="C_element : 034"  # scripted group (container) (typed FeaturePython)
  n = 6
  ref = C_element
FEATURE [App::DocumentObjectGroupPython] H_element062  label="H_element : 031"  # scripted group (container) (typed FeaturePython)
  n = 5
  ref = H_element
FEATURE [App::DocumentObjectGroupPython] N_element029  label="N_element : 012"  # scripted group (container) (typed FeaturePython)
  n = 1
  ref = N_element
FEATURE [App::DocumentObjectGroupPython] O_element069  label="O_element : 034"  # scripted group (container) (typed FeaturePython)
  n = 2
  ref = O_element
FEATURE [App::DocumentObjectGroupPython] G4_NITROBENZENE  # scripted group (container) (typed FeaturePython)
  Dunit = g/cm3
  Dvalue = 1.19867
  Group = -> [C_element068,H_element062,N_element029,O_element069]
  conduct = 2
  density = 1
  expand = 3
  formula = G4_NITROBENZENE
  name = G4_NITROBENZENE
  specific = 4
FEATURE [App::DocumentObjectGroupPython] N_element030  label="N_element : 013"  # scripted group (container) (typed FeaturePython)
  n = 2
  ref = N_element
FEATURE [App::DocumentObjectGroupPython] O_element070  label="O_element : 035"  # scripted group (container) (typed FeaturePython)
  n = 1
  ref = O_element
FEATURE [App::DocumentObjectGroupPython] G4_NITROUS_OXIDE  # scripted group (container) (typed FeaturePython)
  Dunit = g/cm3
  Dvalue = 0.00183094
  Group = -> [N_element030,O_element070]
  conduct = 2
  density = 1
  expand = 3
  formula = G4_NITROUS_OXIDE
  name = G4_NITROUS_OXIDE
  specific = 4
FEATURE [App::DocumentObjectGroupPython] H_element063  label="H_element : 0.104"  # scripted group (container) (typed FeaturePython)
  n = 0.103509
FEATURE [App::DocumentObjectGroupPython] C_element069  label="C_element : 0.648"  # scripted group (container) (typed FeaturePython)
  n = 0.648416
FEATURE [App::DocumentObjectGroupPython] N_element031  label="N_element : 0.100"  # scripted group (container) (typed FeaturePython)
  n = 0.0995361
FEATURE [App::DocumentObjectGroupPython] O_element071  label="O_element : 0.149"  # scripted group (container) (typed FeaturePython)
  n = 0.148539
FEATURE [App::DocumentObjectGroupPython] G4_NYLON_8062  label="G4_NYLON-8062"  # scripted group (container) (typed FeaturePython)
  Dunit = g/cm3
  Dvalue = 1.08
  Group = -> [H_element063,C_element069,N_element031,O_element071]
  conduct = 2
  density = 1
  expand = 3
  formula = G4_NYLON-8062
  name = G4_NYLON-8062
  specific = 4
FEATURE [App::DocumentObjectGroupPython] C_element070  label="C_element : 035"  # scripted group (container) (typed FeaturePython)
  n = 6
  ref = C_element
FEATURE [App::DocumentObjectGroupPython] H_element064  label="H_element : 11"  # scripted group (container) (typed FeaturePython)
  n = 11
  ref = H_element
FEATURE [App::DocumentObjectGroupPython] N_element032  label="N_element : 014"  # scripted group (container) (typed FeaturePython)
  n = 1
  ref = N_element
FEATURE [App::DocumentObjectGroupPython] O_element072  label="O_element : 036"  # scripted group (container) (typed FeaturePython)
  n = 1
  ref = O_element
FEATURE [App::DocumentObjectGroupPython] G4_NYLON_6_6  label="G4_NYLON-6-6"  # scripted group (container) (typed FeaturePython)
  Dunit = g/cm3
  Dvalue = 1.14
  Group = -> [C_element070,H_element064,N_element032,O_element072]
  conduct = 2
  density = 1
  expand = 3
  formula = G4_NYLON-6-6
  name = G4_NYLON-6-6
  specific = 4
FEATURE [App::DocumentObjectGroupPython] H_element065  label="H_element : 0.139"  # scripted group (container) (typed FeaturePython)
  n = 0.107062
FEATURE [App::DocumentObjectGroupPython] C_element071  label="C_element : 0.680"  # scripted group (container) (typed FeaturePython)
  n = 0.680449
FEATURE [App::DocumentObjectGroupPython] N_element033  label="N_element : 0.099"  # scripted group (container) (typed FeaturePython)
  n = 0.099189
FEATURE [App::DocumentObjectGroupPython] O_element073  label="O_element : 0.113"  # scripted group (container) (typed FeaturePython)
  n = 0.1133
FEATURE [App::DocumentObjectGroupPython] G4_NYLON_6_10  label="G4_NYLON-6-10"  # scripted group (container) (typed FeaturePython)
  Dunit = g/cm3
  Dvalue = 1.14
  Group = -> [H_element065,C_element071,N_element033,O_element073]
  conduct = 2
  density = 1
  expand = 3
  formula = G4_NYLON-6-10
  name = G4_NYLON-6-10
  specific = 4
FEATURE [App::DocumentObjectGroupPython] H_element066  label="H_element : 0.140"  # scripted group (container) (typed FeaturePython)
  n = 0.115476
FEATURE [App::DocumentObjectGroupPython] C_element072  label="C_element : 0.721"  # scripted group (container) (typed FeaturePython)
  n = 0.720818
FEATURE [App::DocumentObjectGroupPython] N_element034  label="N_element : 0.076"  # scripted group (container) (typed FeaturePython)
  n = 0.0764169
FEATURE [App::DocumentObjectGroupPython] O_element074  label="O_element : 0.087"  # scripted group (container) (typed FeaturePython)
  n = 0.0872889
FEATURE [App::DocumentObjectGroupPython] G4_NYLON_11_RILSAN  label="G4_NYLON-11_RILSAN"  # scripted group (container) (typed FeaturePython)
  Dunit = g/cm3
  Dvalue = 1.425
  Group = -> [H_element066,C_element072,N_element034,O_element074]
  conduct = 2
  density = 1
  expand = 3
  formula = G4_NYLON-11_RILSAN
  name = G4_NYLON-11_RILSAN
  specific = 4
FEATURE [App::DocumentObjectGroupPython] C_element073  label="C_element : 8"  # scripted group (container) (typed FeaturePython)
  n = 8
  ref = C_element
FEATURE [App::DocumentObjectGroupPython] H_element067  label="H_element : 18"  # scripted group (container) (typed FeaturePython)
  n = 18
  ref = H_element
FEATURE [App::DocumentObjectGroupPython] G4_OCTANE  # scripted group (container) (typed FeaturePython)
  Dunit = g/cm3
  Dvalue = 0.7026
  Group = -> [C_element073,H_element067]
  conduct = 2
  density = 1
  expand = 3
  formula = G4_OCTANE
  name = G4_OCTANE
  specific = 4
FEATURE [App::DocumentObjectGroupPython] C_element074  label="C_element : 25"  # scripted group (container) (typed FeaturePython)
  n = 25
  ref = C_element
FEATURE [App::DocumentObjectGroupPython] H_element068  label="H_element : 52"  # scripted group (container) (typed FeaturePython)
  n = 52
  ref = H_element
FEATURE [App::DocumentObjectGroupPython] G4_PARAFFIN  # scripted group (container) (typed FeaturePython)
  Dunit = g/cm3
  Dvalue = 0.93
  Group = -> [C_element074,H_element068]
  conduct = 2
  density = 1
  expand = 3
  formula = G4_PARAFFIN
  name = G4_PARAFFIN
  specific = 4
FEATURE [App::DocumentObjectGroupPython] C_element075  label="C_element : 036"  # scripted group (container) (typed FeaturePython)
  n = 5
  ref = C_element
FEATURE [App::DocumentObjectGroupPython] H_element069  label="H_element : 032"  # scripted group (container) (typed FeaturePython)
  n = 12
  ref = H_element
FEATURE [App::DocumentObjectGroupPython] G4_N_PENTANE  label="G4_N-PENTANE"  # scripted group (container) (typed FeaturePython)
  Dunit = g/cm3
  Dvalue = 0.6262
  Group = -> [C_element075,H_element069]
  conduct = 2
  density = 1
  expand = 3
  formula = G4_N-PENTANE
  name = G4_N-PENTANE
  specific = 4
FEATURE [App::DocumentObjectGroupPython] H_element070  label="H_element : 0.014"  # scripted group (container) (typed FeaturePython)
  n = 0.0141
FEATURE [App::DocumentObjectGroupPython] C_element076  label="C_element : 0.072"  # scripted group (container) (typed FeaturePython)
  n = 0.072261
FEATURE [App::DocumentObjectGroupPython] N_element035  label="N_element : 0.019"  # scripted group (container) (typed FeaturePython)
  n = 0.01932
FEATURE [App::DocumentObjectGroupPython] O_element075  label="O_element : 0.066"  # scripted group (container) (typed FeaturePython)
  n = 0.066101
FEATURE [App::DocumentObjectGroupPython] S_element019  label="S_element : 0.020"  # scripted group (container) (typed FeaturePython)
  n = 0.00189
FEATURE [App::DocumentObjectGroupPython] Br_element004  label="Br_element : 0.349"  # scripted group (container) (typed FeaturePython)
  n = 0.349103
FEATURE [App::DocumentObjectGroupPython] Ag_element001  label="Ag_element : 0.474"  # scripted group (container) (typed FeaturePython)
  n = 0.474105
FEATURE [App::DocumentObjectGroupPython] I_element005  label="I_element : 0.003"  # scripted group (container) (typed FeaturePython)
  n = 0.00312
FEATURE [App::DocumentObjectGroupPython] G4_PHOTO_EMULSION  # scripted group (container) (typed FeaturePython)
  Dunit = g/cm3
  Dvalue = 3.815
  Group = -> [H_element070,C_element076,N_element035,O_element075,S_element019,Br_element004,Ag_element001,I_element005]
  conduct = 2
  density = 1
  expand = 3
  formula = G4_PHOTO_EMULSION
  name = G4_PHOTO_EMULSION
  specific = 4
FEATURE [App::DocumentObjectGroupPython] C_element077  label="C_element : 9"  # scripted group (container) (typed FeaturePython)
  n = 9
  ref = C_element
FEATURE [App::DocumentObjectGroupPython] H_element071  label="H_element : 033"  # scripted group (container) (typed FeaturePython)
  n = 10
  ref = H_element
FEATURE [App::DocumentObjectGroupPython] G4_PLASTIC_SC_VINYLTOLUENE  # scripted group (container) (typed FeaturePython)
  Dunit = g/cm3
  Dvalue = 1.032
  Group = -> [C_element077,H_element071]
  conduct = 2
  density = 1
  expand = 3
  formula = G4_PLASTIC_SC_VINYLTOLUENE
  name = G4_PLASTIC_SC_VINYLTOLUENE
  specific = 4
FEATURE [App::DocumentObjectGroupPython] Pu_element001  label="Pu_element : 1"  # scripted group (container) (typed FeaturePython)
  n = 1
  ref = Pu_element
FEATURE [App::DocumentObjectGroupPython] O_element076  label="O_element : 037"  # scripted group (container) (typed FeaturePython)
  n = 2
  ref = O_element
FEATURE [App::DocumentObjectGroupPython] G4_PLUTONIUM_DIOXIDE  # scripted group (container) (typed FeaturePython)
  Dunit = g/cm3
  Dvalue = 11.46
  Group = -> [Pu_element001,O_element076]
  conduct = 2
  density = 1
  expand = 3
  formula = G4_PLUTONIUM_DIOXIDE
  name = G4_PLUTONIUM_DIOXIDE
  specific = 4
FEATURE [App::DocumentObjectGroupPython] C_element078  label="C_element : 037"  # scripted group (container) (typed FeaturePython)
  n = 3
  ref = C_element
FEATURE [App::DocumentObjectGroupPython] H_element072  label="H_element : 034"  # scripted group (container) (typed FeaturePython)
  n = 3
  ref = H_element
FEATURE [App::DocumentObjectGroupPython] N_element036  label="N_element : 015"  # scripted group (container) (typed FeaturePython)
  n = 1
  ref = N_element
FEATURE [App::DocumentObjectGroupPython] G4_POLYACRYLONITRILE  # scripted group (container) (typed FeaturePython)
  Dunit = g/cm3
  Dvalue = 1.17
  Group = -> [C_element078,H_element072,N_element036]
  conduct = 2
  density = 1
  expand = 3
  formula = G4_POLYACRYLONITRILE
  name = G4_POLYACRYLONITRILE
  specific = 4
FEATURE [App::DocumentObjectGroupPython] C_element079  label="C_element : 16"  # scripted group (container) (typed FeaturePython)
  n = 16
  ref = C_element
FEATURE [App::DocumentObjectGroupPython] H_element073  label="H_element : 035"  # scripted group (container) (typed FeaturePython)
  n = 14
  ref = H_element
FEATURE [App::DocumentObjectGroupPython] O_element077  label="O_element : 038"  # scripted group (container) (typed FeaturePython)
  n = 3
  ref = O_element
FEATURE [App::DocumentObjectGroupPython] G4_POLYCARBONATE  # scripted group (container) (typed FeaturePython)
  Dunit = g/cm3
  Dvalue = 1.2
  Group = -> [C_element079,H_element073,O_element077]
  conduct = 2
  density = 1
  expand = 3
  formula = G4_POLYCARBONATE
  name = G4_POLYCARBONATE
  specific = 4
FEATURE [App::DocumentObjectGroupPython] C_element080  label="C_element : 038"  # scripted group (container) (typed FeaturePython)
  n = 8
  ref = C_element
FEATURE [App::DocumentObjectGroupPython] H_element074  label="H_element : 036"  # scripted group (container) (typed FeaturePython)
  n = 7
  ref = H_element
FEATURE [App::DocumentObjectGroupPython] Cl_element017  label="Cl_element : 007"  # scripted group (container) (typed FeaturePython)
  n = 1
  ref = Cl_element
FEATURE [App::DocumentObjectGroupPython] G4_POLYCHLOROSTYRENE  # scripted group (container) (typed FeaturePython)
  Dunit = g/cm3
  Dvalue = 1.3
  Group = -> [C_element080,H_element074,Cl_element017]
  conduct = 2
  density = 1
  expand = 3
  formula = G4_POLYCHLOROSTYRENE
  name = G4_POLYCHLOROSTYRENE
  specific = 4
FEATURE [App::DocumentObjectGroupPython] C_element081  label="C_element : 039"  # scripted group (container) (typed FeaturePython)
  n = 1
  ref = C_element
FEATURE [App::DocumentObjectGroupPython] H_element075  label="H_element : 037"  # scripted group (container) (typed FeaturePython)
  n = 2
  ref = H_element
FEATURE [App::DocumentObjectGroupPython] G4_POLYETHYLENE  # scripted group (container) (typed FeaturePython)
  Dunit = g/cm3
  Dvalue = 0.94
  Group = -> [C_element081,H_element075]
  conduct = 2
  density = 1
  expand = 3
  formula = G4_POLYETHYLENE
  name = G4_POLYETHYLENE
  specific = 4
FEATURE [App::DocumentObjectGroupPython] C_element082  label="C_element : 040"  # scripted group (container) (typed FeaturePython)
  n = 10
  ref = C_element
FEATURE [App::DocumentObjectGroupPython] H_element076  label="H_element : 038"  # scripted group (container) (typed FeaturePython)
  n = 8
  ref = H_element
FEATURE [App::DocumentObjectGroupPython] O_element078  label="O_element : 039"  # scripted group (container) (typed FeaturePython)
  n = 4
  ref = O_element
FEATURE [App::DocumentObjectGroupPython] G4_MYLAR  # scripted group (container) (typed FeaturePython)
  Dunit = g/cm3
  Dvalue = 1.4
  Group = -> [C_element082,H_element076,O_element078]
  conduct = 2
  density = 1
  expand = 3
  formula = G4_MYLAR
  name = G4_MYLAR
  specific = 4
FEATURE [App::DocumentObjectGroupPython] C_element083  label="C_element : 041"  # scripted group (container) (typed FeaturePython)
  n = 5
  ref = C_element
FEATURE [App::DocumentObjectGroupPython] H_element077  label="H_element : 039"  # scripted group (container) (typed FeaturePython)
  n = 8
  ref = H_element
FEATURE [App::DocumentObjectGroupPython] O_element079  label="O_element : 040"  # scripted group (container) (typed FeaturePython)
  n = 2
  ref = O_element
FEATURE [App::DocumentObjectGroupPython] G4_PLEXIGLASS  # scripted group (container) (typed FeaturePython)
  Dunit = g/cm3
  Dvalue = 1.19
  Group = -> [C_element083,H_element077,O_element079]
  conduct = 2
  density = 1
  expand = 3
  formula = G4_PLEXIGLASS
  name = G4_PLEXIGLASS
  specific = 4
FEATURE [App::DocumentObjectGroupPython] C_element084  label="C_element : 042"  # scripted group (container) (typed FeaturePython)
  n = 1
  ref = C_element
FEATURE [App::DocumentObjectGroupPython] H_element078  label="H_element : 040"  # scripted group (container) (typed FeaturePython)
  n = 2
  ref = H_element
FEATURE [App::DocumentObjectGroupPython] O_element080  label="O_element : 041"  # scripted group (container) (typed FeaturePython)
  n = 1
  ref = O_element
FEATURE [App::DocumentObjectGroupPython] G4_POLYOXYMETHYLENE  # scripted group (container) (typed FeaturePython)
  Dunit = g/cm3
  Dvalue = 1.425
  Group = -> [C_element084,H_element078,O_element080]
  conduct = 2
  density = 1
  expand = 3
  formula = G4_POLYOXYMETHYLENE
  name = G4_POLYOXYMETHYLENE
  specific = 4
FEATURE [App::DocumentObjectGroupPython] C_element085  label="C_element : 043"  # scripted group (container) (typed FeaturePython)
  n = 2
  ref = C_element
FEATURE [App::DocumentObjectGroupPython] H_element079  label="H_element : 041"  # scripted group (container) (typed FeaturePython)
  n = 4
  ref = H_element
FEATURE [App::DocumentObjectGroupPython] G4_POLYPROPYLENE  # scripted group (container) (typed FeaturePython)
  Dunit = g/cm3
  Dvalue = 0.9
  Group = -> [C_element085,H_element079]
  conduct = 2
  density = 1
  expand = 3
  formula = G4_POLYPROPYLENE
  name = G4_POLYPROPYLENE
  specific = 4
FEATURE [App::DocumentObjectGroupPython] C_element086  label="C_element : 044"  # scripted group (container) (typed FeaturePython)
  n = 8
  ref = C_element
FEATURE [App::DocumentObjectGroupPython] H_element080  label="H_element : 042"  # scripted group (container) (typed FeaturePython)
  n = 8
  ref = H_element
FEATURE [App::DocumentObjectGroupPython] G4_POLYSTYRENE  # scripted group (container) (typed FeaturePython)
  Dunit = g/cm3
  Dvalue = 1.06
  Group = -> [C_element086,H_element080]
  conduct = 2
  density = 1
  expand = 3
  formula = G4_POLYSTYRENE
  name = G4_POLYSTYRENE
  specific = 4
FEATURE [App::DocumentObjectGroupPython] C_element087  label="C_element : 045"  # scripted group (container) (typed FeaturePython)
  n = 2
  ref = C_element
FEATURE [App::DocumentObjectGroupPython] F_element014  label="F_element : 4"  # scripted group (container) (typed FeaturePython)
  n = 4
  ref = F_element
FEATURE [App::DocumentObjectGroupPython] G4_TEFLON  # scripted group (container) (typed FeaturePython)
  Dunit = g/cm3
  Dvalue = 2.2
  Group = -> [C_element087,F_element014]
  conduct = 2
  density = 1
  expand = 3
  formula = G4_TEFLON
  name = G4_TEFLON
  specific = 4
FEATURE [App::DocumentObjectGroupPython] C_element088  label="C_element : 046"  # scripted group (container) (typed FeaturePython)
  n = 2
  ref = C_element
FEATURE [App::DocumentObjectGroupPython] F_element015  label="F_element : 006"  # scripted group (container) (typed FeaturePython)
  n = 3
  ref = F_element
FEATURE [App::DocumentObjectGroupPython] Cl_element018  label="Cl_element : 008"  # scripted group (container) (typed FeaturePython)
  n = 1
  ref = Cl_element
FEATURE [App::DocumentObjectGroupPython] G4_POLYTRIFLUOROCHLOROETHYLENE  # scripted group (container) (typed FeaturePython)
  Dunit = g/cm3
  Dvalue = 2.1
  Group = -> [C_element088,F_element015,Cl_element018]
  conduct = 2
  density = 1
  expand = 3
  formula = G4_POLYTRIFLUOROCHLOROETHYLENE
  name = G4_POLYTRIFLUOROCHLOROETHYLENE
  specific = 4
FEATURE [App::DocumentObjectGroupPython] C_element089  label="C_element : 047"  # scripted group (container) (typed FeaturePython)
  n = 4
  ref = C_element
FEATURE [App::DocumentObjectGroupPython] H_element081  label="H_element : 043"  # scripted group (container) (typed FeaturePython)
  n = 6
  ref = H_element
FEATURE [App::DocumentObjectGroupPython] O_element081  label="O_element : 042"  # scripted group (container) (typed FeaturePython)
  n = 2
  ref = O_element
FEATURE [App::DocumentObjectGroupPython] G4_POLYVINYL_ACETATE  # scripted group (container) (typed FeaturePython)
  Dunit = g/cm3
  Dvalue = 1.19
  Group = -> [C_element089,H_element081,O_element081]
  conduct = 2
  density = 1
  expand = 3
  formula = G4_POLYVINYL_ACETATE
  name = G4_POLYVINYL_ACETATE
  specific = 4
FEATURE [App::DocumentObjectGroupPython] C_element090  label="C_element : 048"  # scripted group (container) (typed FeaturePython)
  n = 2
  ref = C_element
FEATURE [App::DocumentObjectGroupPython] H_element082  label="H_element : 044"  # scripted group (container) (typed FeaturePython)
  n = 4
  ref = H_element
FEATURE [App::DocumentObjectGroupPython] O_element082  label="O_element : 043"  # scripted group (container) (typed FeaturePython)
  n = 1
  ref = O_element
FEATURE [App::DocumentObjectGroupPython] G4_POLYVINYL_ALCOHOL  # scripted group (container) (typed FeaturePython)
  Dunit = g/cm3
  Dvalue = 1.3
  Group = -> [C_element090,H_element082,O_element082]
  conduct = 2
  density = 1
  expand = 3
  formula = G4_POLYVINYL_ALCOHOL
  name = G4_POLYVINYL_ALCOHOL
  specific = 4
FEATURE [App::DocumentObjectGroupPython] C_element091  label="C_element : 049"  # scripted group (container) (typed FeaturePython)
  n = 8
  ref = C_element
FEATURE [App::DocumentObjectGroupPython] H_element083  label="H_element : 045"  # scripted group (container) (typed FeaturePython)
  n = 14
  ref = H_element
FEATURE [App::DocumentObjectGroupPython] O_element083  label="O_element : 044"  # scripted group (container) (typed FeaturePython)
  n = 2
  ref = O_element
FEATURE [App::DocumentObjectGroupPython] G4_POLYVINYL_BUTYRAL  # scripted group (container) (typed FeaturePython)
  Dunit = g/cm3
  Dvalue = 1.12
  Group = -> [C_element091,H_element083,O_element083]
  conduct = 2
  density = 1
  expand = 3
  formula = G4_POLYVINYL_BUTYRAL
  name = G4_POLYVINYL_BUTYRAL
  specific = 4
FEATURE [App::DocumentObjectGroupPython] C_element092  label="C_element : 050"  # scripted group (container) (typed FeaturePython)
  n = 2
  ref = C_element
FEATURE [App::DocumentObjectGroupPython] H_element084  label="H_element : 046"  # scripted group (container) (typed FeaturePython)
  n = 3
  ref = H_element
FEATURE [App::DocumentObjectGroupPython] Cl_element019  label="Cl_element : 009"  # scripted group (container) (typed FeaturePython)
  n = 1
  ref = Cl_element
FEATURE [App::DocumentObjectGroupPython] G4_POLYVINYL_CHLORIDE  # scripted group (container) (typed FeaturePython)
  Dunit = g/cm3
  Dvalue = 1.3
  Group = -> [C_element092,H_element084,Cl_element019]
  conduct = 2
  density = 1
  expand = 3
  formula = G4_POLYVINYL_CHLORIDE
  name = G4_POLYVINYL_CHLORIDE
  specific = 4
FEATURE [App::DocumentObjectGroupPython] C_element093  label="C_element : 051"  # scripted group (container) (typed FeaturePython)
  n = 2
  ref = C_element
FEATURE [App::DocumentObjectGroupPython] H_element085  label="H_element : 047"  # scripted group (container) (typed FeaturePython)
  n = 2
  ref = H_element
FEATURE [App::DocumentObjectGroupPython] Cl_element020  label="Cl_element : 010"  # scripted group (container) (typed FeaturePython)
  n = 2
  ref = Cl_element
FEATURE [App::DocumentObjectGroupPython] G4_POLYVINYLIDENE_CHLORIDE  # scripted group (container) (typed FeaturePython)
  Dunit = g/cm3
  Dvalue = 1.7
  Group = -> [C_element093,H_element085,Cl_element020]
  conduct = 2
  density = 1
  expand = 3
  formula = G4_POLYVINYLIDENE_CHLORIDE
  name = G4_POLYVINYLIDENE_CHLORIDE
  specific = 4
FEATURE [App::DocumentObjectGroupPython] C_element094  label="C_element : 052"  # scripted group (container) (typed FeaturePython)
  n = 2
  ref = C_element
FEATURE [App::DocumentObjectGroupPython] H_element086  label="H_element : 048"  # scripted group (container) (typed FeaturePython)
  n = 2
  ref = H_element
FEATURE [App::DocumentObjectGroupPython] F_element016  label="F_element : 007"  # scripted group (container) (typed FeaturePython)
  n = 2
  ref = F_element
FEATURE [App::DocumentObjectGroupPython] G4_POLYVINYLIDENE_FLUORIDE  # scripted group (container) (typed FeaturePython)
  Dunit = g/cm3
  Dvalue = 1.76
  Group = -> [C_element094,H_element086,F_element016]
  conduct = 2
  density = 1
  expand = 3
  formula = G4_POLYVINYLIDENE_FLUORIDE
  name = G4_POLYVINYLIDENE_FLUORIDE
  specific = 4
FEATURE [App::DocumentObjectGroupPython] C_element095  label="C_element : 053"  # scripted group (container) (typed FeaturePython)
  n = 6
  ref = C_element
FEATURE [App::DocumentObjectGroupPython] H_element087  label="H_element : 9"  # scripted group (container) (typed FeaturePython)
  n = 9
  ref = H_element
FEATURE [App::DocumentObjectGroupPython] N_element037  label="N_element : 016"  # scripted group (container) (typed FeaturePython)
  n = 1
  ref = N_element
FEATURE [App::DocumentObjectGroupPython] O_element084  label="O_element : 045"  # scripted group (container) (typed FeaturePython)
  n = 1
  ref = O_element
FEATURE [App::DocumentObjectGroupPython] G4_POLYVINYL_PYRROLIDONE  # scripted group (container) (typed FeaturePython)
  Dunit = g/cm3
  Dvalue = 1.25
  Group = -> [C_element095,H_element087,N_element037,O_element084]
  conduct = 2
  density = 1
  expand = 3
  formula = G4_POLYVINYL_PYRROLIDONE
  name = G4_POLYVINYL_PYRROLIDONE
  specific = 4
FEATURE [App::DocumentObjectGroupPython] K_element008  label="K_element : 1"  # scripted group (container) (typed FeaturePython)
  n = 1
  ref = K_element
FEATURE [App::DocumentObjectGroupPython] I_element006  label="I_element : 003"  # scripted group (container) (typed FeaturePython)
  n = 1
  ref = I_element
FEATURE [App::DocumentObjectGroupPython] G4_POTASSIUM_IODIDE  # scripted group (container) (typed FeaturePython)
  Dunit = g/cm3
  Dvalue = 3.13
  Group = -> [K_element008,I_element006]
  conduct = 2
  density = 1
  expand = 3
  formula = G4_POTASSIUM_IODIDE
  name = G4_POTASSIUM_IODIDE
  specific = 4
FEATURE [App::DocumentObjectGroupPython] K_element009  label="K_element : 2"  # scripted group (container) (typed FeaturePython)
  n = 2
  ref = K_element
FEATURE [App::DocumentObjectGroupPython] O_element085  label="O_element : 046"  # scripted group (container) (typed FeaturePython)
  n = 1
  ref = O_element
FEATURE [App::DocumentObjectGroupPython] G4_POTASSIUM_OXIDE  # scripted group (container) (typed FeaturePython)
  Dunit = g/cm3
  Dvalue = 2.32
  Group = -> [K_element009,O_element085]
  conduct = 2
  density = 1
  expand = 3
  formula = G4_POTASSIUM_OXIDE
  name = G4_POTASSIUM_OXIDE
  specific = 4
FEATURE [App::DocumentObjectGroupPython] C_element096  label="C_element : 054"  # scripted group (container) (typed FeaturePython)
  n = 3
  ref = C_element
FEATURE [App::DocumentObjectGroupPython] H_element088  label="H_element : 049"  # scripted group (container) (typed FeaturePython)
  n = 8
  ref = H_element
FEATURE [App::DocumentObjectGroupPython] G4_PROPANE  # scripted group (container) (typed FeaturePython)
  Dunit = g/cm3
  Dvalue = 0.00187939
  Group = -> [C_element096,H_element088]
  conduct = 2
  density = 1
  expand = 3
  formula = G4_PROPANE
  name = G4_PROPANE
  specific = 4
FEATURE [App::DocumentObjectGroupPython] C_element097  label="C_element : 055"  # scripted group (container) (typed FeaturePython)
  n = 3
  ref = C_element
FEATURE [App::DocumentObjectGroupPython] H_element089  label="H_element : 050"  # scripted group (container) (typed FeaturePython)
  n = 8
  ref = H_element
FEATURE [App::DocumentObjectGroupPython] G4_lPROPANE  # scripted group (container) (typed FeaturePython)
  Dunit = g/cm3
  Dvalue = 0.43
  Group = -> [C_element097,H_element089]
  conduct = 2
  density = 1
  expand = 3
  formula = G4_lPROPANE
  name = G4_lPROPANE
  specific = 4
FEATURE [App::DocumentObjectGroupPython] C_element098  label="C_element : 056"  # scripted group (container) (typed FeaturePython)
  n = 3
  ref = C_element
FEATURE [App::DocumentObjectGroupPython] H_element090  label="H_element : 051"  # scripted group (container) (typed FeaturePython)
  n = 8
  ref = H_element
FEATURE [App::DocumentObjectGroupPython] O_element086  label="O_element : 047"  # scripted group (container) (typed FeaturePython)
  n = 1
  ref = O_element
FEATURE [App::DocumentObjectGroupPython] G4_N_PROPYL_ALCOHOL  label="G4_N-PROPYL_ALCOHOL"  # scripted group (container) (typed FeaturePython)
  Dunit = g/cm3
  Dvalue = 0.8035
  Group = -> [C_element098,H_element090,O_element086]
  conduct = 2
  density = 1
  expand = 3
  formula = G4_N-PROPYL_ALCOHOL
  name = G4_N-PROPYL_ALCOHOL
  specific = 4
FEATURE [App::DocumentObjectGroupPython] C_element099  label="C_element : 057"  # scripted group (container) (typed FeaturePython)
  n = 5
  ref = C_element
FEATURE [App::DocumentObjectGroupPython] H_element091  label="H_element : 052"  # scripted group (container) (typed FeaturePython)
  n = 5
  ref = H_element
FEATURE [App::DocumentObjectGroupPython] N_element038  label="N_element : 017"  # scripted group (container) (typed FeaturePython)
  n = 1
  ref = N_element
FEATURE [App::DocumentObjectGroupPython] G4_PYRIDINE  # scripted group (container) (typed FeaturePython)
  Dunit = g/cm3
  Dvalue = 0.9819
  Group = -> [C_element099,H_element091,N_element038]
  conduct = 2
  density = 1
  expand = 3
  formula = G4_PYRIDINE
  name = G4_PYRIDINE
  specific = 4
FEATURE [App::DocumentObjectGroupPython] H_element092  label="H_element : 0.144"  # scripted group (container) (typed FeaturePython)
  n = 0.143711
FEATURE [App::DocumentObjectGroupPython] C_element100  label="C_element : 0.856"  # scripted group (container) (typed FeaturePython)
  n = 0.856289
FEATURE [App::DocumentObjectGroupPython] G4_RUBBER_BUTYL  # scripted group (container) (typed FeaturePython)
  Dunit = g/cm3
  Dvalue = 0.92
  Group = -> [H_element092,C_element100]
  conduct = 2
  density = 1
  expand = 3
  formula = G4_RUBBER_BUTYL
  name = G4_RUBBER_BUTYL
  specific = 4
FEATURE [App::DocumentObjectGroupPython] H_element093  label="H_element : 0.118"  # scripted group (container) (typed FeaturePython)
  n = 0.118371
FEATURE [App::DocumentObjectGroupPython] C_element101  label="C_element : 0.882"  # scripted group (container) (typed FeaturePython)
  n = 0.881629
FEATURE [App::DocumentObjectGroupPython] G4_RUBBER_NATURAL  # scripted group (container) (typed FeaturePython)
  Dunit = g/cm3
  Dvalue = 0.92
  Group = -> [H_element093,C_element101]
  conduct = 2
  density = 1
  expand = 3
  formula = G4_RUBBER_NATURAL
  name = G4_RUBBER_NATURAL
  specific = 4
FEATURE [App::DocumentObjectGroupPython] H_element094  label="H_element : 0.145"  # scripted group (container) (typed FeaturePython)
  n = 0.05692
FEATURE [App::DocumentObjectGroupPython] C_element102  label="C_element : 0.543"  # scripted group (container) (typed FeaturePython)
  n = 0.542646
FEATURE [App::DocumentObjectGroupPython] Cl_element021  label="Cl_element : 0.400"  # scripted group (container) (typed FeaturePython)
  n = 0.400434
FEATURE [App::DocumentObjectGroupPython] G4_RUBBER_NEOPRENE  # scripted group (container) (typed FeaturePython)
  Dunit = g/cm3
  Dvalue = 1.23
  Group = -> [H_element094,C_element102,Cl_element021]
  conduct = 2
  density = 1
  expand = 3
  formula = G4_RUBBER_NEOPRENE
  name = G4_RUBBER_NEOPRENE
  specific = 4
FEATURE [App::DocumentObjectGroupPython] Si_element006  label="Si_element : 1"  # scripted group (container) (typed FeaturePython)
  n = 1
  ref = Si_element
FEATURE [App::DocumentObjectGroupPython] O_element087  label="O_element : 048"  # scripted group (container) (typed FeaturePython)
  n = 2
  ref = O_element
FEATURE [App::DocumentObjectGroupPython] G4_SILICON_DIOXIDE  # scripted group (container) (typed FeaturePython)
  Dunit = g/cm3
  Dvalue = 2.32
  Group = -> [Si_element006,O_element087]
  conduct = 2
  density = 1
  expand = 3
  formula = G4_SILICON_DIOXIDE
  name = G4_SILICON_DIOXIDE
  specific = 4
FEATURE [App::DocumentObjectGroupPython] Ag_element002  label="Ag_element : 1"  # scripted group (container) (typed FeaturePython)
  n = 1
  ref = Ag_element
FEATURE [App::DocumentObjectGroupPython] Br_element005  label="Br_element : 003"  # scripted group (container) (typed FeaturePython)
  n = 1
  ref = Br_element
FEATURE [App::DocumentObjectGroupPython] G4_SILVER_BROMIDE  # scripted group (container) (typed FeaturePython)
  Dunit = g/cm3
  Dvalue = 6.473
  Group = -> [Ag_element002,Br_element005]
  conduct = 2
  density = 1
  expand = 3
  formula = G4_SILVER_BROMIDE
  name = G4_SILVER_BROMIDE
  specific = 4
FEATURE [App::DocumentObjectGroupPython] Ag_element003  label="Ag_element : 002"  # scripted group (container) (typed FeaturePython)
  n = 1
  ref = Ag_element
FEATURE [App::DocumentObjectGroupPython] Cl_element022  label="Cl_element : 011"  # scripted group (container) (typed FeaturePython)
  n = 1
  ref = Cl_element
FEATURE [App::DocumentObjectGroupPython] G4_SILVER_CHLORIDE  # scripted group (container) (typed FeaturePython)
  Dunit = g/cm3
  Dvalue = 5.56
  Group = -> [Ag_element003,Cl_element022]
  conduct = 2
  density = 1
  expand = 3
  formula = G4_SILVER_CHLORIDE
  name = G4_SILVER_CHLORIDE
  specific = 4
FEATURE [App::DocumentObjectGroupPython] Br_element006  label="Br_element : 0.423"  # scripted group (container) (typed FeaturePython)
  n = 0.422895
FEATURE [App::DocumentObjectGroupPython] Ag_element004  label="Ag_element : 0.574"  # scripted group (container) (typed FeaturePython)
  n = 0.573748
FEATURE [App::DocumentObjectGroupPython] I_element007  label="I_element : 0.649"  # scripted group (container) (typed FeaturePython)
  n = 0.003357
FEATURE [App::DocumentObjectGroupPython] G4_SILVER_HALIDES  # scripted group (container) (typed FeaturePython)
  Dunit = g/cm3
  Dvalue = 6.47
  Group = -> [Br_element006,Ag_element004,I_element007]
  conduct = 2
  density = 1
  expand = 3
  formula = G4_SILVER_HALIDES
  name = G4_SILVER_HALIDES
  specific = 4
FEATURE [App::DocumentObjectGroupPython] Ag_element005  label="Ag_element : 003"  # scripted group (container) (typed FeaturePython)
  n = 1
  ref = Ag_element
FEATURE [App::DocumentObjectGroupPython] I_element008  label="I_element : 004"  # scripted group (container) (typed FeaturePython)
  n = 1
  ref = I_element
FEATURE [App::DocumentObjectGroupPython] G4_SILVER_IODIDE  # scripted group (container) (typed FeaturePython)
  Dunit = g/cm3
  Dvalue = 6.01
  Group = -> [Ag_element005,I_element008]
  conduct = 2
  density = 1
  expand = 3
  formula = G4_SILVER_IODIDE
  name = G4_SILVER_IODIDE
  specific = 4
FEATURE [App::DocumentObjectGroupPython] H_element095  label="H_element : 0.100"  # scripted group (container) (typed FeaturePython)
  n = 0.1
FEATURE [App::DocumentObjectGroupPython] C_element103  label="C_element : 0.204"  # scripted group (container) (typed FeaturePython)
  n = 0.204
FEATURE [App::DocumentObjectGroupPython] N_element039  label="N_element : 0.759"  # scripted group (container) (typed FeaturePython)
  n = 0.042
FEATURE [App::DocumentObjectGroupPython] O_element088  label="O_element : 0.645"  # scripted group (container) (typed FeaturePython)
  n = 0.645
FEATURE [App::DocumentObjectGroupPython] Na_element013  label="Na_element : 0.100"  # scripted group (container) (typed FeaturePython)
  n = 0.002
FEATURE [App::DocumentObjectGroupPython] P_element009  label="P_element : 0.107"  # scripted group (container) (typed FeaturePython)
  n = 0.001
FEATURE [App::DocumentObjectGroupPython] S_element020  label="S_element : 0.021"  # scripted group (container) (typed FeaturePython)
  n = 0.002
FEATURE [App::DocumentObjectGroupPython] Cl_element023  label="Cl_element : 0.590"  # scripted group (container) (typed FeaturePython)
  n = 0.003
FEATURE [App::DocumentObjectGroupPython] K_element010  label="K_element : 0.001"  # scripted group (container) (typed FeaturePython)
  n = 0.001
FEATURE [App::DocumentObjectGroupPython] G4_SKIN_ICRP  # scripted group (container) (typed FeaturePython)
  Dunit = g/cm3
  Dvalue = 1.09
  Group = -> [H_element095,C_element103,N_element039,O_element088,Na_element013,P_element009,S_element020,Cl_element023,K_element010]
  conduct = 2
  density = 1
  expand = 3
  formula = G4_SKIN_ICRP
  name = G4_SKIN_ICRP
  specific = 4
FEATURE [App::DocumentObjectGroupPython] Na_element014  label="Na_element : 2"  # scripted group (container) (typed FeaturePython)
  n = 2
  ref = Na_element
FEATURE [App::DocumentObjectGroupPython] C_element104  label="C_element : 058"  # scripted group (container) (typed FeaturePython)
  n = 1
  ref = C_element
FEATURE [App::DocumentObjectGroupPython] O_element089  label="O_element : 049"  # scripted group (container) (typed FeaturePython)
  n = 3
  ref = O_element
FEATURE [App::DocumentObjectGroupPython] G4_SODIUM_CARBONATE  # scripted group (container) (typed FeaturePython)
  Dunit = g/cm3
  Dvalue = 2.532
  Group = -> [Na_element014,C_element104,O_element089]
  conduct = 2
  density = 1
  expand = 3
  formula = G4_SODIUM_CARBONATE
  name = G4_SODIUM_CARBONATE
  specific = 4
FEATURE [App::DocumentObjectGroupPython] Na_element015  label="Na_element : 1"  # scripted group (container) (typed FeaturePython)
  n = 1
  ref = Na_element
FEATURE [App::DocumentObjectGroupPython] I_element009  label="I_element : 005"  # scripted group (container) (typed FeaturePython)
  n = 1
  ref = I_element
FEATURE [App::DocumentObjectGroupPython] G4_SODIUM_IODIDE  # scripted group (container) (typed FeaturePython)
  Dunit = g/cm3
  Dvalue = 3.667
  Group = -> [Na_element015,I_element009]
  conduct = 2
  density = 1
  expand = 3
  formula = G4_SODIUM_IODIDE
  name = G4_SODIUM_IODIDE
  specific = 4
FEATURE [App::DocumentObjectGroupPython] Na_element016  label="Na_element : 003"  # scripted group (container) (typed FeaturePython)
  n = 2
  ref = Na_element
FEATURE [App::DocumentObjectGroupPython] O_element090  label="O_element : 050"  # scripted group (container) (typed FeaturePython)
  n = 1
  ref = O_element
FEATURE [App::DocumentObjectGroupPython] G4_SODIUM_MONOXIDE  # scripted group (container) (typed FeaturePython)
  Dunit = g/cm3
  Dvalue = 2.27
  Group = -> [Na_element016,O_element090]
  conduct = 2
  density = 1
  expand = 3
  formula = G4_SODIUM_MONOXIDE
  name = G4_SODIUM_MONOXIDE
  specific = 4
FEATURE [App::DocumentObjectGroupPython] Na_element017  label="Na_element : 004"  # scripted group (container) (typed FeaturePython)
  n = 1
  ref = Na_element
FEATURE [App::DocumentObjectGroupPython] N_element040  label="N_element : 018"  # scripted group (container) (typed FeaturePython)
  n = 1
  ref = N_element
FEATURE [App::DocumentObjectGroupPython] O_element091  label="O_element : 051"  # scripted group (container) (typed FeaturePython)
  n = 3
  ref = O_element
FEATURE [App::DocumentObjectGroupPython] G4_SODIUM_NITRATE  # scripted group (container) (typed FeaturePython)
  Dunit = g/cm3
  Dvalue = 2.261
  Group = -> [Na_element017,N_element040,O_element091]
  conduct = 2
  density = 1
  expand = 3
  formula = G4_SODIUM_NITRATE
  name = G4_SODIUM_NITRATE
  specific = 4
FEATURE [App::DocumentObjectGroupPython] C_element105  label="C_element : 059"  # scripted group (container) (typed FeaturePython)
  n = 14
  ref = C_element
FEATURE [App::DocumentObjectGroupPython] H_element096  label="H_element : 053"  # scripted group (container) (typed FeaturePython)
  n = 12
  ref = H_element
FEATURE [App::DocumentObjectGroupPython] G4_STILBENE  # scripted group (container) (typed FeaturePython)
  Dunit = g/cm3
  Dvalue = 0.9707
  Group = -> [C_element105,H_element096]
  conduct = 2
  density = 1
  expand = 3
  formula = G4_STILBENE
  name = G4_STILBENE
  specific = 4
FEATURE [App::DocumentObjectGroupPython] C_element106  label="C_element : 12"  # scripted group (container) (typed FeaturePython)
  n = 12
  ref = C_element
FEATURE [App::DocumentObjectGroupPython] H_element097  label="H_element : 22"  # scripted group (container) (typed FeaturePython)
  n = 22
  ref = H_element
FEATURE [App::DocumentObjectGroupPython] O_element092  label="O_element : 11"  # scripted group (container) (typed FeaturePython)
  n = 11
  ref = O_element
FEATURE [App::DocumentObjectGroupPython] G4_SUCROSE  # scripted group (container) (typed FeaturePython)
  Dunit = g/cm3
  Dvalue = 1.5805
  Group = -> [C_element106,H_element097,O_element092]
  conduct = 2
  density = 1
  expand = 3
  formula = G4_SUCROSE
  name = G4_SUCROSE
  specific = 4
FEATURE [App::DocumentObjectGroupPython] C_element107  label="C_element : 18"  # scripted group (container) (typed FeaturePython)
  n = 18
  ref = C_element
FEATURE [App::DocumentObjectGroupPython] H_element098  label="H_element : 054"  # scripted group (container) (typed FeaturePython)
  n = 14
  ref = H_element
FEATURE [App::DocumentObjectGroupPython] G4_TERPHENYL  # scripted group (container) (typed FeaturePython)
  Dunit = g/cm3
  Dvalue = 1.24
  Group = -> [C_element107,H_element098]
  conduct = 2
  density = 1
  expand = 3
  formula = G4_TERPHENYL
  name = G4_TERPHENYL
  specific = 4
FEATURE [App::DocumentObjectGroupPython] H_element099  label="H_element : 0.146"  # scripted group (container) (typed FeaturePython)
  n = 0.106
FEATURE [App::DocumentObjectGroupPython] C_element108  label="C_element : 0.883"  # scripted group (container) (typed FeaturePython)
  n = 0.099
FEATURE [App::DocumentObjectGroupPython] N_element041  label="N_element : 0.020"  # scripted group (container) (typed FeaturePython)
  n = 0.02
FEATURE [App::DocumentObjectGroupPython] O_element093  label="O_element : 0.766"  # scripted group (container) (typed FeaturePython)
  n = 0.766
FEATURE [App::DocumentObjectGroupPython] Na_element018  label="Na_element : 0.101"  # scripted group (container) (typed FeaturePython)
  n = 0.002
FEATURE [App::DocumentObjectGroupPython] P_element010  label="P_element : 0.108"  # scripted group (container) (typed FeaturePython)
  n = 0.001
FEATURE [App::DocumentObjectGroupPython] S_element021  label="S_element : 0.022"  # scripted group (container) (typed FeaturePython)
  n = 0.002
FEATURE [App::DocumentObjectGroupPython] Cl_element024  label="Cl_element : 0.002"  # scripted group (container) (typed FeaturePython)
  n = 0.002
FEATURE [App::DocumentObjectGroupPython] K_element011  label="K_element : 0.017"  # scripted group (container) (typed FeaturePython)
  n = 0.002
FEATURE [App::DocumentObjectGroupPython] G4_TESTIS_ICRP  # scripted group (container) (typed FeaturePython)
  Dunit = g/cm3
  Dvalue = 1.04
  Group = -> [H_element099,C_element108,N_element041,O_element093,Na_element018,P_element010,S_element021,Cl_element024,K_element011]
  conduct = 2
  density = 1
  expand = 3
  formula = G4_TESTIS_ICRP
  name = G4_TESTIS_ICRP
  specific = 4
FEATURE [App::DocumentObjectGroupPython] C_element109  label="C_element : 060"  # scripted group (container) (typed FeaturePython)
  n = 2
  ref = C_element
FEATURE [App::DocumentObjectGroupPython] Cl_element025  label="Cl_element : 012"  # scripted group (container) (typed FeaturePython)
  n = 4
  ref = Cl_element
FEATURE [App::DocumentObjectGroupPython] G4_TETRACHLOROETHYLENE  # scripted group (container) (typed FeaturePython)
  Dunit = g/cm3
  Dvalue = 1.625
  Group = -> [C_element109,Cl_element025]
  conduct = 2
  density = 1
  expand = 3
  formula = G4_TETRACHLOROETHYLENE
  name = G4_TETRACHLOROETHYLENE
  specific = 4
FEATURE [App::DocumentObjectGroupPython] Tl_element001  label="Tl_element : 1"  # scripted group (container) (typed FeaturePython)
  n = 1
  ref = Tl_element
FEATURE [App::DocumentObjectGroupPython] Cl_element026  label="Cl_element : 013"  # scripted group (container) (typed FeaturePython)
  n = 1
  ref = Cl_element
FEATURE [App::DocumentObjectGroupPython] G4_THALLIUM_CHLORIDE  # scripted group (container) (typed FeaturePython)
  Dunit = g/cm3
  Dvalue = 7.004
  Group = -> [Tl_element001,Cl_element026]
  conduct = 2
  density = 1
  expand = 3
  formula = G4_THALLIUM_CHLORIDE
  name = G4_THALLIUM_CHLORIDE
  specific = 4
FEATURE [App::DocumentObjectGroupPython] H_element100  label="H_element : 0.147"  # scripted group (container) (typed FeaturePython)
  n = 0.105
FEATURE [App::DocumentObjectGroupPython] C_element110  label="C_element : 0.256"  # scripted group (container) (typed FeaturePython)
  n = 0.256
FEATURE [App::DocumentObjectGroupPython] N_element042  label="N_element : 0.760"  # scripted group (container) (typed FeaturePython)
  n = 0.027
FEATURE [App::DocumentObjectGroupPython] O_element094  label="O_element : 0.602"  # scripted group (container) (typed FeaturePython)
  n = 0.602
FEATURE [App::DocumentObjectGroupPython] Na_element019  label="Na_element : 0.102"  # scripted group (container) (typed FeaturePython)
  n = 0.001
FEATURE [App::DocumentObjectGroupPython] P_element011  label="P_element : 0.109"  # scripted group (container) (typed FeaturePython)
  n = 0.002
FEATURE [App::DocumentObjectGroupPython] S_element022  label="S_element : 0.023"  # scripted group (container) (typed FeaturePython)
  n = 0.003
FEATURE [App::DocumentObjectGroupPython] Cl_element027  label="Cl_element : 0.591"  # scripted group (container) (typed FeaturePython)
  n = 0.002
FEATURE [App::DocumentObjectGroupPython] K_element012  label="K_element : 0.018"  # scripted group (container) (typed FeaturePython)
  n = 0.002
FEATURE [App::DocumentObjectGroupPython] G4_TISSUE_SOFT_ICRP  # scripted group (container) (typed FeaturePython)
  Dunit = g/cm3
  Dvalue = 1.03
  Group = -> [H_element100,C_element110,N_element042,O_element094,Na_element019,P_element011,S_element022,Cl_element027,K_element012]
  conduct = 2
  density = 1
  expand = 3
  formula = G4_TISSUE_SOFT_ICRP
  name = G4_TISSUE_SOFT_ICRP
  specific = 4
FEATURE [App::DocumentObjectGroupPython] H_element101  label="H_element : 0.148"  # scripted group (container) (typed FeaturePython)
  n = 0.101
FEATURE [App::DocumentObjectGroupPython] C_element111  label="C_element : 0.111"  # scripted group (container) (typed FeaturePython)
  n = 0.111
FEATURE [App::DocumentObjectGroupPython] N_element043  label="N_element : 0.026"  # scripted group (container) (typed FeaturePython)
  n = 0.026
FEATURE [App::DocumentObjectGroupPython] O_element095  label="O_element : 0.762"  # scripted group (container) (typed FeaturePython)
  n = 0.762
FEATURE [App::DocumentObjectGroupPython] G4_TISSUE_SOFT_ICRU_4  label="G4_TISSUE_SOFT_ICRU-4"  # scripted group (container) (typed FeaturePython)
  Dunit = g/cm3
  Dvalue = 1
  Group = -> [H_element101,C_element111,N_element043,O_element095]
  conduct = 2
  density = 1
  expand = 3
  formula = G4_TISSUE_SOFT_ICRU-4
  name = G4_TISSUE_SOFT_ICRU-4
  specific = 4
FEATURE [App::DocumentObjectGroupPython] H_element102  label="H_element : 0.149"  # scripted group (container) (typed FeaturePython)
  n = 0.101869
FEATURE [App::DocumentObjectGroupPython] C_element112  label="C_element : 0.456"  # scripted group (container) (typed FeaturePython)
  n = 0.456179
FEATURE [App::DocumentObjectGroupPython] N_element044  label="N_element : 0.761"  # scripted group (container) (typed FeaturePython)
  n = 0.035172
FEATURE [App::DocumentObjectGroupPython] O_element096  label="O_element : 0.407"  # scripted group (container) (typed FeaturePython)
  n = 0.40678
FEATURE [App::DocumentObjectGroupPython] G4_TISSUE_METHANE  label="G4_TISSUE-METHANE"  # scripted group (container) (typed FeaturePython)
  Dunit = g/cm3
  Dvalue = 0.00106409
  Group = -> [H_element102,C_element112,N_element044,O_element096]
  conduct = 2
  density = 1
  expand = 3
  formula = G4_TISSUE-METHANE
  name = G4_TISSUE-METHANE
  specific = 4
FEATURE [App::DocumentObjectGroupPython] H_element103  label="H_element : 0.103"  # scripted group (container) (typed FeaturePython)
  n = 0.102672
FEATURE [App::DocumentObjectGroupPython] C_element113  label="C_element : 0.569"  # scripted group (container) (typed FeaturePython)
  n = 0.56894
FEATURE [App::DocumentObjectGroupPython] N_element045  label="N_element : 0.762"  # scripted group (container) (typed FeaturePython)
  n = 0.035022
FEATURE [App::DocumentObjectGroupPython] O_element097  label="O_element : 0.293"  # scripted group (container) (typed FeaturePython)
  n = 0.293366
FEATURE [App::DocumentObjectGroupPython] G4_TISSUE_PROPANE  label="G4_TISSUE-PROPANE"  # scripted group (container) (typed FeaturePython)
  Dunit = g/cm3
  Dvalue = 0.00182628
  Group = -> [H_element103,C_element113,N_element045,O_element097]
  conduct = 2
  density = 1
  expand = 3
  formula = G4_TISSUE-PROPANE
  name = G4_TISSUE-PROPANE
  specific = 4
FEATURE [App::DocumentObjectGroupPython] Ti_element003  label="Ti_element : 1"  # scripted group (container) (typed FeaturePython)
  n = 1
  ref = Ti_element
FEATURE [App::DocumentObjectGroupPython] O_element098  label="O_element : 052"  # scripted group (container) (typed FeaturePython)
  n = 2
  ref = O_element
FEATURE [App::DocumentObjectGroupPython] G4_TITANIUM_DIOXIDE  # scripted group (container) (typed FeaturePython)
  Dunit = g/cm3
  Dvalue = 4.26
  Group = -> [Ti_element003,O_element098]
  conduct = 2
  density = 1
  expand = 3
  formula = G4_TITANIUM_DIOXIDE
  name = G4_TITANIUM_DIOXIDE
  specific = 4
FEATURE [App::DocumentObjectGroupPython] C_element114  label="C_element : 061"  # scripted group (container) (typed FeaturePython)
  n = 7
  ref = C_element
FEATURE [App::DocumentObjectGroupPython] H_element104  label="H_element : 055"  # scripted group (container) (typed FeaturePython)
  n = 8
  ref = H_element
FEATURE [App::DocumentObjectGroupPython] G4_TOLUENE  # scripted group (container) (typed FeaturePython)
  Dunit = g/cm3
  Dvalue = 0.8669
  Group = -> [C_element114,H_element104]
  conduct = 2
  density = 1
  expand = 3
  formula = G4_TOLUENE
  name = G4_TOLUENE
  specific = 4
FEATURE [App::DocumentObjectGroupPython] C_element115  label="C_element : 062"  # scripted group (container) (typed FeaturePython)
  n = 2
  ref = C_element
FEATURE [App::DocumentObjectGroupPython] H_element105  label="H_element : 056"  # scripted group (container) (typed FeaturePython)
  n = 1
  ref = H_element
FEATURE [App::DocumentObjectGroupPython] Cl_element028  label="Cl_element : 014"  # scripted group (container) (typed FeaturePython)
  n = 3
  ref = Cl_element
FEATURE [App::DocumentObjectGroupPython] G4_TRICHLOROETHYLENE  # scripted group (container) (typed FeaturePython)
  Dunit = g/cm3
  Dvalue = 1.46
  Group = -> [C_element115,H_element105,Cl_element028]
  conduct = 2
  density = 1
  expand = 3
  formula = G4_TRICHLOROETHYLENE
  name = G4_TRICHLOROETHYLENE
  specific = 4
FEATURE [App::DocumentObjectGroupPython] C_element116  label="C_element : 063"  # scripted group (container) (typed FeaturePython)
  n = 6
  ref = C_element
FEATURE [App::DocumentObjectGroupPython] H_element106  label="H_element : 15"  # scripted group (container) (typed FeaturePython)
  n = 15
  ref = H_element
FEATURE [App::DocumentObjectGroupPython] O_element099  label="O_element : 053"  # scripted group (container) (typed FeaturePython)
  n = 4
  ref = O_element
FEATURE [App::DocumentObjectGroupPython] P_element012  label="P_element : 1"  # scripted group (container) (typed FeaturePython)
  n = 1
  ref = P_element
FEATURE [App::DocumentObjectGroupPython] G4_TRIETHYL_PHOSPHATE  # scripted group (container) (typed FeaturePython)
  Dunit = g/cm3
  Dvalue = 1.07
  Group = -> [C_element116,H_element106,O_element099,P_element012]
  conduct = 2
  density = 1
  expand = 3
  formula = G4_TRIETHYL_PHOSPHATE
  name = G4_TRIETHYL_PHOSPHATE
  specific = 4
FEATURE [App::DocumentObjectGroupPython] W_element003  label="W_element : 003"  # scripted group (container) (typed FeaturePython)
  n = 1
  ref = W_element
FEATURE [App::DocumentObjectGroupPython] F_element017  label="F_element : 6"  # scripted group (container) (typed FeaturePython)
  n = 6
  ref = F_element
FEATURE [App::DocumentObjectGroupPython] G4_TUNGSTEN_HEXAFLUORIDE  # scripted group (container) (typed FeaturePython)
  Dunit = g/cm3
  Dvalue = 2.4
  Group = -> [W_element003,F_element017]
  conduct = 2
  density = 1
  expand = 3
  formula = G4_TUNGSTEN_HEXAFLUORIDE
  name = G4_TUNGSTEN_HEXAFLUORIDE
  specific = 4
FEATURE [App::DocumentObjectGroupPython] U_element001  label="U_element : 1"  # scripted group (container) (typed FeaturePython)
  n = 1
  ref = U_element
FEATURE [App::DocumentObjectGroupPython] C_element117  label="C_element : 064"  # scripted group (container) (typed FeaturePython)
  n = 2
  ref = C_element
FEATURE [App::DocumentObjectGroupPython] G4_URANIUM_DICARBIDE  # scripted group (container) (typed FeaturePython)
  Dunit = g/cm3
  Dvalue = 11.28
  Group = -> [U_element001,C_element117]
  conduct = 2
  density = 1
  expand = 3
  formula = G4_URANIUM_DICARBIDE
  name = G4_URANIUM_DICARBIDE
  specific = 4
FEATURE [App::DocumentObjectGroupPython] U_element002  label="U_element : 002"  # scripted group (container) (typed FeaturePython)
  n = 1
  ref = U_element
FEATURE [App::DocumentObjectGroupPython] C_element118  label="C_element : 065"  # scripted group (container) (typed FeaturePython)
  n = 1
  ref = C_element
FEATURE [App::DocumentObjectGroupPython] G4_URANIUM_MONOCARBIDE  # scripted group (container) (typed FeaturePython)
  Dunit = g/cm3
  Dvalue = 13.63
  Group = -> [U_element002,C_element118]
  conduct = 2
  density = 1
  expand = 3
  formula = G4_URANIUM_MONOCARBIDE
  name = G4_URANIUM_MONOCARBIDE
  specific = 4
FEATURE [App::DocumentObjectGroupPython] U_element003  label="U_element : 003"  # scripted group (container) (typed FeaturePython)
  n = 1
  ref = U_element
FEATURE [App::DocumentObjectGroupPython] O_element100  label="O_element : 054"  # scripted group (container) (typed FeaturePython)
  n = 2
  ref = O_element
FEATURE [App::DocumentObjectGroupPython] G4_URANIUM_OXIDE  # scripted group (container) (typed FeaturePython)
  Dunit = g/cm3
  Dvalue = 10.96
  Group = -> [U_element003,O_element100]
  conduct = 2
  density = 1
  expand = 3
  formula = G4_URANIUM_OXIDE
  name = G4_URANIUM_OXIDE
  specific = 4
FEATURE [App::DocumentObjectGroupPython] C_element119  label="C_element : 066"  # scripted group (container) (typed FeaturePython)
  n = 1
  ref = C_element
FEATURE [App::DocumentObjectGroupPython] H_element107  label="H_element : 057"  # scripted group (container) (typed FeaturePython)
  n = 4
  ref = H_element
FEATURE [App::DocumentObjectGroupPython] N_element046  label="N_element : 019"  # scripted group (container) (typed FeaturePython)
  n = 2
  ref = N_element
FEATURE [App::DocumentObjectGroupPython] O_element101  label="O_element : 055"  # scripted group (container) (typed FeaturePython)
  n = 1
  ref = O_element
FEATURE [App::DocumentObjectGroupPython] G4_UREA  # scripted group (container) (typed FeaturePython)
  Dunit = g/cm3
  Dvalue = 1.323
  Group = -> [C_element119,H_element107,N_element046,O_element101]
  conduct = 2
  density = 1
  expand = 3
  formula = G4_UREA
  name = G4_UREA
  specific = 4
FEATURE [App::DocumentObjectGroupPython] C_element120  label="C_element : 067"  # scripted group (container) (typed FeaturePython)
  n = 5
  ref = C_element
FEATURE [App::DocumentObjectGroupPython] H_element108  label="H_element : 058"  # scripted group (container) (typed FeaturePython)
  n = 11
  ref = H_element
FEATURE [App::DocumentObjectGroupPython] N_element047  label="N_element : 020"  # scripted group (container) (typed FeaturePython)
  n = 1
  ref = N_element
FEATURE [App::DocumentObjectGroupPython] O_element102  label="O_element : 056"  # scripted group (container) (typed FeaturePython)
  n = 2
  ref = O_element
FEATURE [App::DocumentObjectGroupPython] G4_VALINE  # scripted group (container) (typed FeaturePython)
  Dunit = g/cm3
  Dvalue = 1.23
  Group = -> [C_element120,H_element108,N_element047,O_element102]
  conduct = 2
  density = 1
  expand = 3
  formula = G4_VALINE
  name = G4_VALINE
  specific = 4
FEATURE [App::DocumentObjectGroupPython] H_element109  label="H_element : 0.009"  # scripted group (container) (typed FeaturePython)
  n = 0.009417
FEATURE [App::DocumentObjectGroupPython] C_element121  label="C_element : 0.281"  # scripted group (container) (typed FeaturePython)
  n = 0.280555
FEATURE [App::DocumentObjectGroupPython] F_element018  label="F_element : 0.710"  # scripted group (container) (typed FeaturePython)
  n = 0.710028
FEATURE [App::DocumentObjectGroupPython] G4_VITON  # scripted group (container) (typed FeaturePython)
  Dunit = g/cm3
  Dvalue = 1.8
  Group = -> [H_element109,C_element121,F_element018]
  conduct = 2
  density = 1
  expand = 3
  formula = G4_VITON
  name = G4_VITON
  specific = 4
FEATURE [App::DocumentObjectGroupPython] H_element110  label="H_element : 059"  # scripted group (container) (typed FeaturePython)
  n = 2
  ref = H_element
FEATURE [App::DocumentObjectGroupPython] O_element103  label="O_element : 057"  # scripted group (container) (typed FeaturePython)
  n = 1
  ref = O_element
FEATURE [App::DocumentObjectGroupPython] G4_WATER  # scripted group (container) (typed FeaturePython)
  Dunit = g/cm3
  Dvalue = 1
  Group = -> [H_element110,O_element103]
  conduct = 2
  density = 1
  expand = 3
  formula = G4_WATER
  name = G4_WATER
  specific = 4
FEATURE [App::DocumentObjectGroupPython] H_element111  label="H_element : 060"  # scripted group (container) (typed FeaturePython)
  n = 2
  ref = H_element
FEATURE [App::DocumentObjectGroupPython] O_element104  label="O_element : 058"  # scripted group (container) (typed FeaturePython)
  n = 1
  ref = O_element
FEATURE [App::DocumentObjectGroupPython] G4_WATER_VAPOR  # scripted group (container) (typed FeaturePython)
  Dunit = g/cm3
  Dvalue = 0.000756182
  Group = -> [H_element111,O_element104]
  conduct = 2
  density = 1
  expand = 3
  formula = G4_WATER_VAPOR
  name = G4_WATER_VAPOR
  specific = 4
FEATURE [App::DocumentObjectGroupPython] C_element122  label="C_element : 068"  # scripted group (container) (typed FeaturePython)
  n = 8
  ref = C_element
FEATURE [App::DocumentObjectGroupPython] H_element112  label="H_element : 061"  # scripted group (container) (typed FeaturePython)
  n = 10
  ref = H_element
FEATURE [App::DocumentObjectGroupPython] G4_XYLENE  # scripted group (container) (typed FeaturePython)
  Dunit = g/cm3
  Dvalue = 0.87
  Group = -> [C_element122,H_element112]
  conduct = 2
  density = 1
  expand = 3
  formula = G4_XYLENE
  name = G4_XYLENE
  specific = 4
FEATURE [App::DocumentObjectGroupPython] C_element123  label="C_element : 069"  # scripted group (container) (typed FeaturePython)
  n = 1
  ref = C_element
FEATURE [App::DocumentObjectGroupPython] G4_GRAPHITE  # scripted group (container) (typed FeaturePython)
  Dunit = g/cm3
  Dvalue = 2.21
  Group = -> [C_element123]
  conduct = 2
  density = 1
  expand = 3
  formula = G4_GRAPHITE
  name = G4_GRAPHITE
  specific = 4
FEATURE [App::DocumentObjectGroupPython] NIST  # scripted group (container) (typed FeaturePython)
  Group = -> [G4_A_150_TISSUE,G4_ACETONE,G4_ACETYLENE,G4_ADENINE,G4_ADIPOSE_TISSUE_ICRP,G4_AIR,G4_ALANINE,G4_ALUMINUM_OXIDE,G4_AMBER,G4_AMMONIA,G4_ANILINE,G4_ANTHRACENE,G4_B_100_BONE,G4_BAKELITE,G4_BARIUM_FLUORIDE,G4_BARIUM_SULFATE,G4_BENZENE,G4_BERYLLIUM_OXIDE,G4_BGO,G4_BLOOD_ICRP,G4_BONE_COMPACT_ICRU,G4_BONE_CORTICAL_ICRP,G4_BORON_CARBIDE,G4_BORON_OXIDE,G4_BRAIN_ICRP,G4_BUTANE,G4_N_BUTYL_ALCOHOL,G4_C_552,+152 more]
FEATURE [App::DocumentObjectGroupPython] H_element113  label="H_element : 062"  # scripted group (container) (typed FeaturePython)
  n = 1
  ref = H_element
FEATURE [App::DocumentObjectGroupPython] G4_H  # scripted group (container) (typed FeaturePython)
  Dunit = g/cm3
  Dvalue = 8.3748e-05
  Group = -> [H_element113]
  conduct = 2
  density = 1
  expand = 3
  formula = H
  name = G4_H
  specific = 4
FEATURE [App::DocumentObjectGroupPython] He_element001  label="He_element : 1"  # scripted group (container) (typed FeaturePython)
  n = 1
  ref = He_element
FEATURE [App::DocumentObjectGroupPython] G4_He  # scripted group (container) (typed FeaturePython)
  Dunit = g/cm3
  Dvalue = 0.000166322
  Group = -> [He_element001]
  conduct = 2
  density = 1
  expand = 3
  formula = He
  name = G4_He
  specific = 4
FEATURE [App::DocumentObjectGroupPython] Li_element008  label="Li_element : 008"  # scripted group (container) (typed FeaturePython)
  n = 1
  ref = Li_element
FEATURE [App::DocumentObjectGroupPython] G4_Li  # scripted group (container) (typed FeaturePython)
  Dunit = g/cm3
  Dvalue = 0.534
  Group = -> [Li_element008]
  conduct = 2
  density = 1
  expand = 3
  formula = Li
  name = G4_Li
  specific = 4
FEATURE [App::DocumentObjectGroupPython] Be_element002  label="Be_element : 002"  # scripted group (container) (typed FeaturePython)
  n = 1
  ref = Be_element
FEATURE [App::DocumentObjectGroupPython] G4_Be  # scripted group (container) (typed FeaturePython)
  Dunit = g/cm3
  Dvalue = 1.848
  Group = -> [Be_element002]
  conduct = 2
  density = 1
  expand = 3
  formula = Be
  name = G4_Be
  specific = 4
FEATURE [App::DocumentObjectGroupPython] B_element007  label="B_element : 007"  # scripted group (container) (typed FeaturePython)
  n = 1
  ref = B_element
FEATURE [App::DocumentObjectGroupPython] G4_B  # scripted group (container) (typed FeaturePython)
  Dunit = g/cm3
  Dvalue = 2.37
  Group = -> [B_element007]
  conduct = 2
  density = 1
  expand = 3
  formula = B
  name = G4_B
  specific = 4
FEATURE [App::DocumentObjectGroupPython] C_element124  label="C_element : 070"  # scripted group (container) (typed FeaturePython)
  n = 1
  ref = C_element
FEATURE [App::DocumentObjectGroupPython] G4_C  # scripted group (container) (typed FeaturePython)
  Dunit = g/cm3
  Dvalue = 2
  Group = -> [C_element124]
  conduct = 2
  density = 1
  expand = 3
  formula = C
  name = G4_C
  specific = 4
FEATURE [App::DocumentObjectGroupPython] N_element048  label="N_element : 021"  # scripted group (container) (typed FeaturePython)
  n = 1
  ref = N_element
FEATURE [App::DocumentObjectGroupPython] G4_N  # scripted group (container) (typed FeaturePython)
  Dunit = g/cm3
  Dvalue = 0.0011652
  Group = -> [N_element048]
  conduct = 2
  density = 1
  expand = 3
  formula = N
  name = G4_N
  specific = 4
FEATURE [App::DocumentObjectGroupPython] O_element105  label="O_element : 059"  # scripted group (container) (typed FeaturePython)
  n = 1
  ref = O_element
FEATURE [App::DocumentObjectGroupPython] G4_O  # scripted group (container) (typed FeaturePython)
  Dunit = g/cm3
  Dvalue = 0.00133151
  Group = -> [O_element105]
  conduct = 2
  density = 1
  expand = 3
  formula = O
  name = G4_O
  specific = 4
FEATURE [App::DocumentObjectGroupPython] F_element019  label="F_element : 008"  # scripted group (container) (typed FeaturePython)
  n = 1
  ref = F_element
FEATURE [App::DocumentObjectGroupPython] G4_F  # scripted group (container) (typed FeaturePython)
  Dunit = g/cm3
  Dvalue = 0.00158029
  Group = -> [F_element019]
  conduct = 2
  density = 1
  expand = 3
  formula = F
  name = G4_F
  specific = 4
FEATURE [App::DocumentObjectGroupPython] Ne_element001  label="Ne_element : 1"  # scripted group (container) (typed FeaturePython)
  n = 1
  ref = Ne_element
FEATURE [App::DocumentObjectGroupPython] G4_Ne  # scripted group (container) (typed FeaturePython)
  Dunit = g/cm3
  Dvalue = 0.000838505
  Group = -> [Ne_element001]
  conduct = 2
  density = 1
  expand = 3
  formula = Ne
  name = G4_Ne
  specific = 4
FEATURE [App::DocumentObjectGroupPython] Na_element020  label="Na_element : 005"  # scripted group (container) (typed FeaturePython)
  n = 1
  ref = Na_element
FEATURE [App::DocumentObjectGroupPython] G4_Na  # scripted group (container) (typed FeaturePython)
  Dunit = g/cm3
  Dvalue = 0.971
  Group = -> [Na_element020]
  conduct = 2
  density = 1
  expand = 3
  formula = Na
  name = G4_Na
  specific = 4
FEATURE [App::DocumentObjectGroupPython] Mg_element011  label="Mg_element : 005"  # scripted group (container) (typed FeaturePython)
  n = 1
  ref = Mg_element
FEATURE [App::DocumentObjectGroupPython] G4_Mg  # scripted group (container) (typed FeaturePython)
  Dunit = g/cm3
  Dvalue = 1.74
  Group = -> [Mg_element011]
  conduct = 2
  density = 1
  expand = 3
  formula = Mg
  name = G4_Mg
  specific = 4
FEATURE [App::DocumentObjectGroupPython] Al_element004  label="Al_element : 1"  # scripted group (container) (typed FeaturePython)
  n = 1
  ref = Al_element
FEATURE [App::DocumentObjectGroupPython] G4_Al  # scripted group (container) (typed FeaturePython)
  Dunit = g/cm3
  Dvalue = 2.699
  Group = -> [Al_element004]
  conduct = 2
  density = 1
  expand = 3
  formula = Al
  name = G4_Al
  specific = 4
FEATURE [App::DocumentObjectGroupPython] Si_element007  label="Si_element : 002"  # scripted group (container) (typed FeaturePython)
  n = 1
  ref = Si_element
FEATURE [App::DocumentObjectGroupPython] G4_Si  # scripted group (container) (typed FeaturePython)
  Dunit = g/cm3
  Dvalue = 2.33
  Group = -> [Si_element007]
  conduct = 2
  density = 1
  expand = 3
  formula = Si
  name = G4_Si
  specific = 4
FEATURE [App::DocumentObjectGroupPython] P_element013  label="P_element : 002"  # scripted group (container) (typed FeaturePython)
  n = 1
  ref = P_element
FEATURE [App::DocumentObjectGroupPython] G4_P  # scripted group (container) (typed FeaturePython)
  Dunit = g/cm3
  Dvalue = 2.2
  Group = -> [P_element013]
  conduct = 2
  density = 1
  expand = 3
  formula = P
  name = G4_P
  specific = 4
FEATURE [App::DocumentObjectGroupPython] S_element023  label="S_element : 007"  # scripted group (container) (typed FeaturePython)
  n = 1
  ref = S_element
FEATURE [App::DocumentObjectGroupPython] G4_S  # scripted group (container) (typed FeaturePython)
  Dunit = g/cm3
  Dvalue = 2
  Group = -> [S_element023]
  conduct = 2
  density = 1
  expand = 3
  formula = S
  name = G4_S
  specific = 4
FEATURE [App::DocumentObjectGroupPython] Cl_element029  label="Cl_element : 015"  # scripted group (container) (typed FeaturePython)
  n = 1
  ref = Cl_element
FEATURE [App::DocumentObjectGroupPython] G4_Cl  # scripted group (container) (typed FeaturePython)
  Dunit = g/cm3
  Dvalue = 0.00299473
  Group = -> [Cl_element029]
  conduct = 2
  density = 1
  expand = 3
  formula = Cl
  name = G4_Cl
  specific = 4
FEATURE [App::DocumentObjectGroupPython] Ar_element002  label="Ar_element : 1"  # scripted group (container) (typed FeaturePython)
  n = 1
  ref = Ar_element
FEATURE [App::DocumentObjectGroupPython] G4_Ar  # scripted group (container) (typed FeaturePython)
  Dunit = g/cm3
  Dvalue = 0.00166201
  Group = -> [Ar_element002]
  conduct = 2
  density = 1
  expand = 3
  formula = Ar
  name = G4_Ar
  specific = 4
FEATURE [App::DocumentObjectGroupPython] K_element013  label="K_element : 003"  # scripted group (container) (typed FeaturePython)
  n = 1
  ref = K_element
FEATURE [App::DocumentObjectGroupPython] G4_K  # scripted group (container) (typed FeaturePython)
  Dunit = g/cm3
  Dvalue = 0.862
  Group = -> [K_element013]
  conduct = 2
  density = 1
  expand = 3
  formula = K
  name = G4_K
  specific = 4
FEATURE [App::DocumentObjectGroupPython] Ca_element014  label="Ca_element : 007"  # scripted group (container) (typed FeaturePython)
  n = 1
  ref = Ca_element
FEATURE [App::DocumentObjectGroupPython] G4_Ca  # scripted group (container) (typed FeaturePython)
  Dunit = g/cm3
  Dvalue = 1.55
  Group = -> [Ca_element014]
  conduct = 2
  density = 1
  expand = 3
  formula = Ca
  name = G4_Ca
  specific = 4
FEATURE [App::DocumentObjectGroupPython] Sc_element001  label="Sc_element : 1"  # scripted group (container) (typed FeaturePython)
  n = 1
  ref = Sc_element
FEATURE [App::DocumentObjectGroupPython] G4_Sc  # scripted group (container) (typed FeaturePython)
  Dunit = g/cm3
  Dvalue = 2.989
  Group = -> [Sc_element001]
  conduct = 2
  density = 1
  expand = 3
  formula = Sc
  name = G4_Sc
  specific = 4
FEATURE [App::DocumentObjectGroupPython] Ti_element004  label="Ti_element : 002"  # scripted group (container) (typed FeaturePython)
  n = 1
  ref = Ti_element
FEATURE [App::DocumentObjectGroupPython] G4_Ti  # scripted group (container) (typed FeaturePython)
  Dunit = g/cm3
  Dvalue = 4.54
  Group = -> [Ti_element004]
  conduct = 2
  density = 1
  expand = 3
  formula = Ti
  name = G4_Ti
  specific = 4
FEATURE [App::DocumentObjectGroupPython] V_element001  label="V_element : 1"  # scripted group (container) (typed FeaturePython)
  n = 1
  ref = V_element
FEATURE [App::DocumentObjectGroupPython] G4_V  # scripted group (container) (typed FeaturePython)
  Dunit = g/cm3
  Dvalue = 6.11
  Group = -> [V_element001]
  conduct = 2
  density = 1
  expand = 3
  formula = V
  name = G4_V
  specific = 4
FEATURE [App::DocumentObjectGroupPython] Cr_element001  label="Cr_element : 1"  # scripted group (container) (typed FeaturePython)
  n = 1
  ref = Cr_element
FEATURE [App::DocumentObjectGroupPython] G4_Cr  # scripted group (container) (typed FeaturePython)
  Dunit = g/cm3
  Dvalue = 7.18
  Group = -> [Cr_element001]
  conduct = 2
  density = 1
  expand = 3
  formula = Cr
  name = G4_Cr
  specific = 4
FEATURE [App::DocumentObjectGroupPython] Mn_element001  label="Mn_element : 1"  # scripted group (container) (typed FeaturePython)
  n = 1
  ref = Mn_element
FEATURE [App::DocumentObjectGroupPython] G4_Mn  # scripted group (container) (typed FeaturePython)
  Dunit = g/cm3
  Dvalue = 7.44
  Group = -> [Mn_element001]
  conduct = 2
  density = 1
  expand = 3
  formula = Mn
  name = G4_Mn
  specific = 4
FEATURE [App::DocumentObjectGroupPython] Fe_element007  label="Fe_element : 004"  # scripted group (container) (typed FeaturePython)
  n = 1
  ref = Fe_element
FEATURE [App::DocumentObjectGroupPython] G4_Fe  # scripted group (container) (typed FeaturePython)
  Dunit = g/cm3
  Dvalue = 7.874
  Group = -> [Fe_element007]
  conduct = 2
  density = 1
  expand = 3
  formula = Fe
  name = G4_Fe
  specific = 4
FEATURE [App::DocumentObjectGroupPython] Co_element001  label="Co_element : 1"  # scripted group (container) (typed FeaturePython)
  n = 1
  ref = Co_element
FEATURE [App::DocumentObjectGroupPython] G4_Co  # scripted group (container) (typed FeaturePython)
  Dunit = g/cm3
  Dvalue = 8.9
  Group = -> [Co_element001]
  conduct = 2
  density = 1
  expand = 3
  formula = Co
  name = G4_Co
  specific = 4
FEATURE [App::DocumentObjectGroupPython] Ni_element001  label="Ni_element : 1"  # scripted group (container) (typed FeaturePython)
  n = 1
  ref = Ni_element
FEATURE [App::DocumentObjectGroupPython] G4_Ni  # scripted group (container) (typed FeaturePython)
  Dunit = g/cm3
  Dvalue = 8.902
  Group = -> [Ni_element001]
  conduct = 2
  density = 1
  expand = 3
  formula = Ni
  name = G4_Ni
  specific = 4
FEATURE [App::DocumentObjectGroupPython] Cu_element001  label="Cu_element : 1"  # scripted group (container) (typed FeaturePython)
  n = 1
  ref = Cu_element
FEATURE [App::DocumentObjectGroupPython] G4_Cu  # scripted group (container) (typed FeaturePython)
  Dunit = g/cm3
  Dvalue = 8.96
  Group = -> [Cu_element001]
  conduct = 2
  density = 1
  expand = 3
  formula = Cu
  name = G4_Cu
  specific = 4
FEATURE [App::DocumentObjectGroupPython] Zn_element001  label="Zn_element : 1"  # scripted group (container) (typed FeaturePython)
  n = 1
  ref = Zn_element
FEATURE [App::DocumentObjectGroupPython] G4_Zn  # scripted group (container) (typed FeaturePython)
  Dunit = g/cm3
  Dvalue = 7.133
  Group = -> [Zn_element001]
  conduct = 2
  density = 1
  expand = 3
  formula = Zn
  name = G4_Zn
  specific = 4
FEATURE [App::DocumentObjectGroupPython] Ga_element002  label="Ga_element : 002"  # scripted group (container) (typed FeaturePython)
  n = 1
  ref = Ga_element
FEATURE [App::DocumentObjectGroupPython] G4_Ga  # scripted group (container) (typed FeaturePython)
  Dunit = g/cm3
  Dvalue = 5.904
  Group = -> [Ga_element002]
  conduct = 2
  density = 1
  expand = 3
  formula = Ga
  name = G4_Ga
  specific = 4
FEATURE [App::DocumentObjectGroupPython] Ge_element002  label="Ge_element : 1"  # scripted group (container) (typed FeaturePython)
  n = 1
  ref = Ge_element
FEATURE [App::DocumentObjectGroupPython] G4_Ge  # scripted group (container) (typed FeaturePython)
  Dunit = g/cm3
  Dvalue = 5.323
  Group = -> [Ge_element002]
  conduct = 2
  density = 1
  expand = 3
  formula = Ge
  name = G4_Ge
  specific = 4
FEATURE [App::DocumentObjectGroupPython] As_element003  label="As_element : 002"  # scripted group (container) (typed FeaturePython)
  n = 1
  ref = As_element
FEATURE [App::DocumentObjectGroupPython] G4_As  # scripted group (container) (typed FeaturePython)
  Dunit = g/cm3
  Dvalue = 5.73
  Group = -> [As_element003]
  conduct = 2
  density = 1
  expand = 3
  formula = As
  name = G4_As
  specific = 4
FEATURE [App::DocumentObjectGroupPython] Se_element001  label="Se_element : 1"  # scripted group (container) (typed FeaturePython)
  n = 1
  ref = Se_element
FEATURE [App::DocumentObjectGroupPython] G4_Se  # scripted group (container) (typed FeaturePython)
  Dunit = g/cm3
  Dvalue = 4.5
  Group = -> [Se_element001]
  conduct = 2
  density = 1
  expand = 3
  formula = Se
  name = G4_Se
  specific = 4
FEATURE [App::DocumentObjectGroupPython] Br_element007  label="Br_element : 004"  # scripted group (container) (typed FeaturePython)
  n = 1
  ref = Br_element
FEATURE [App::DocumentObjectGroupPython] G4_Br  # scripted group (container) (typed FeaturePython)
  Dunit = g/cm3
  Dvalue = 0.0070721
  Group = -> [Br_element007]
  conduct = 2
  density = 1
  expand = 3
  formula = Br
  name = G4_Br
  specific = 4
FEATURE [App::DocumentObjectGroupPython] Kr_element001  label="Kr_element : 1"  # scripted group (container) (typed FeaturePython)
  n = 1
  ref = Kr_element
FEATURE [App::DocumentObjectGroupPython] G4_Kr  # scripted group (container) (typed FeaturePython)
  Dunit = g/cm3
  Dvalue = 0.00347832
  Group = -> [Kr_element001]
  conduct = 2
  density = 1
  expand = 3
  formula = Kr
  name = G4_Kr
  specific = 4
FEATURE [App::DocumentObjectGroupPython] Rb_element001  label="Rb_element : 1"  # scripted group (container) (typed FeaturePython)
  n = 1
  ref = Rb_element
FEATURE [App::DocumentObjectGroupPython] G4_Rb  # scripted group (container) (typed FeaturePython)
  Dunit = g/cm3
  Dvalue = 1.532
  Group = -> [Rb_element001]
  conduct = 2
  density = 1
  expand = 3
  formula = Rb
  name = G4_Rb
  specific = 4
FEATURE [App::DocumentObjectGroupPython] Sr_element001  label="Sr_element : 1"  # scripted group (container) (typed FeaturePython)
  n = 1
  ref = Sr_element
FEATURE [App::DocumentObjectGroupPython] G4_Sr  # scripted group (container) (typed FeaturePython)
  Dunit = g/cm3
  Dvalue = 2.54
  Group = -> [Sr_element001]
  conduct = 2
  density = 1
  expand = 3
  formula = Sr
  name = G4_Sr
  specific = 4
FEATURE [App::DocumentObjectGroupPython] Y_element001  label="Y_element : 1"  # scripted group (container) (typed FeaturePython)
  n = 1
  ref = Y_element
FEATURE [App::DocumentObjectGroupPython] G4_Y  # scripted group (container) (typed FeaturePython)
  Dunit = g/cm3
  Dvalue = 4.469
  Group = -> [Y_element001]
  conduct = 2
  density = 1
  expand = 3
  formula = Y
  name = G4_Y
  specific = 4
FEATURE [App::DocumentObjectGroupPython] Zr_element001  label="Zr_element : 1"  # scripted group (container) (typed FeaturePython)
  n = 1
  ref = Zr_element
FEATURE [App::DocumentObjectGroupPython] G4_Zr  # scripted group (container) (typed FeaturePython)
  Dunit = g/cm3
  Dvalue = 6.506
  Group = -> [Zr_element001]
  conduct = 2
  density = 1
  expand = 3
  formula = Zr
  name = G4_Zr
  specific = 4
FEATURE [App::DocumentObjectGroupPython] Nb_element001  label="Nb_element : 1"  # scripted group (container) (typed FeaturePython)
  n = 1
  ref = Nb_element
FEATURE [App::DocumentObjectGroupPython] G4_Nb  # scripted group (container) (typed FeaturePython)
  Dunit = g/cm3
  Dvalue = 8.57
  Group = -> [Nb_element001]
  conduct = 2
  density = 1
  expand = 3
  formula = Nb
  name = G4_Nb
  specific = 4
FEATURE [App::DocumentObjectGroupPython] Mo_element001  label="Mo_element : 1"  # scripted group (container) (typed FeaturePython)
  n = 1
  ref = Mo_element
FEATURE [App::DocumentObjectGroupPython] G4_Mo  # scripted group (container) (typed FeaturePython)
  Dunit = g/cm3
  Dvalue = 10.22
  Group = -> [Mo_element001]
  conduct = 2
  density = 1
  expand = 3
  formula = Mo
  name = G4_Mo
  specific = 4
FEATURE [App::DocumentObjectGroupPython] Tc_element001  label="Tc_element : 1"  # scripted group (container) (typed FeaturePython)
  n = 1
  ref = Tc_element
FEATURE [App::DocumentObjectGroupPython] G4_Tc  # scripted group (container) (typed FeaturePython)
  Dunit = g/cm3
  Dvalue = 11.5
  Group = -> [Tc_element001]
  conduct = 2
  density = 1
  expand = 3
  formula = Tc
  name = G4_Tc
  specific = 4
FEATURE [App::DocumentObjectGroupPython] Ru_element001  label="Ru_element : 1"  # scripted group (container) (typed FeaturePython)
  n = 1
  ref = Ru_element
FEATURE [App::DocumentObjectGroupPython] G4_Ru  # scripted group (container) (typed FeaturePython)
  Dunit = g/cm3
  Dvalue = 12.41
  Group = -> [Ru_element001]
  conduct = 2
  density = 1
  expand = 3
  formula = Ru
  name = G4_Ru
  specific = 4
FEATURE [App::DocumentObjectGroupPython] Rh_element001  label="Rh_element : 1"  # scripted group (container) (typed FeaturePython)
  n = 1
  ref = Rh_element
FEATURE [App::DocumentObjectGroupPython] G4_Rh  # scripted group (container) (typed FeaturePython)
  Dunit = g/cm3
  Dvalue = 12.41
  Group = -> [Rh_element001]
  conduct = 2
  density = 1
  expand = 3
  formula = Rh
  name = G4_Rh
  specific = 4
FEATURE [App::DocumentObjectGroupPython] Pd_element001  label="Pd_element : 1"  # scripted group (container) (typed FeaturePython)
  n = 1
  ref = Pd_element
FEATURE [App::DocumentObjectGroupPython] G4_Pd  # scripted group (container) (typed FeaturePython)
  Dunit = g/cm3
  Dvalue = 12.02
  Group = -> [Pd_element001]
  conduct = 2
  density = 1
  expand = 3
  formula = Pd
  name = G4_Pd
  specific = 4
FEATURE [App::DocumentObjectGroupPython] Ag_element006  label="Ag_element : 004"  # scripted group (container) (typed FeaturePython)
  n = 1
  ref = Ag_element
FEATURE [App::DocumentObjectGroupPython] G4_Ag  # scripted group (container) (typed FeaturePython)
  Dunit = g/cm3
  Dvalue = 10.5
  Group = -> [Ag_element006]
  conduct = 2
  density = 1
  expand = 3
  formula = Ag
  name = G4_Ag
  specific = 4
FEATURE [App::DocumentObjectGroupPython] Cd_element003  label="Cd_element : 003"  # scripted group (container) (typed FeaturePython)
  n = 1
  ref = Cd_element
FEATURE [App::DocumentObjectGroupPython] G4_Cd  # scripted group (container) (typed FeaturePython)
  Dunit = g/cm3
  Dvalue = 8.65
  Group = -> [Cd_element003]
  conduct = 2
  density = 1
  expand = 3
  formula = Cd
  name = G4_Cd
  specific = 4
FEATURE [App::DocumentObjectGroupPython] In_element001  label="In_element : 1"  # scripted group (container) (typed FeaturePython)
  n = 1
  ref = In_element
FEATURE [App::DocumentObjectGroupPython] G4_In  # scripted group (container) (typed FeaturePython)
  Dunit = g/cm3
  Dvalue = 7.31
  Group = -> [In_element001]
  conduct = 2
  density = 1
  expand = 3
  formula = In
  name = G4_In
  specific = 4
FEATURE [App::DocumentObjectGroupPython] Sn_element001  label="Sn_element : 1"  # scripted group (container) (typed FeaturePython)
  n = 1
  ref = Sn_element
FEATURE [App::DocumentObjectGroupPython] G4_Sn  # scripted group (container) (typed FeaturePython)
  Dunit = g/cm3
  Dvalue = 7.31
  Group = -> [Sn_element001]
  conduct = 2
  density = 1
  expand = 3
  formula = Sn
  name = G4_Sn
  specific = 4
FEATURE [App::DocumentObjectGroupPython] Sb_element001  label="Sb_element : 1"  # scripted group (container) (typed FeaturePython)
  n = 1
  ref = Sb_element
FEATURE [App::DocumentObjectGroupPython] G4_Sb  # scripted group (container) (typed FeaturePython)
  Dunit = g/cm3
  Dvalue = 6.691
  Group = -> [Sb_element001]
  conduct = 2
  density = 1
  expand = 3
  formula = Sb
  name = G4_Sb
  specific = 4
FEATURE [App::DocumentObjectGroupPython] Te_element002  label="Te_element : 002"  # scripted group (container) (typed FeaturePython)
  n = 1
  ref = Te_element
FEATURE [App::DocumentObjectGroupPython] G4_Te  # scripted group (container) (typed FeaturePython)
  Dunit = g/cm3
  Dvalue = 6.24
  Group = -> [Te_element002]
  conduct = 2
  density = 1
  expand = 3
  formula = Te
  name = G4_Te
  specific = 4
FEATURE [App::DocumentObjectGroupPython] I_element010  label="I_element : 006"  # scripted group (container) (typed FeaturePython)
  n = 1
  ref = I_element
FEATURE [App::DocumentObjectGroupPython] G4_I  # scripted group (container) (typed FeaturePython)
  Dunit = g/cm3
  Dvalue = 4.93
  Group = -> [I_element010]
  conduct = 2
  density = 1
  expand = 3
  formula = I
  name = G4_I
  specific = 4
FEATURE [App::DocumentObjectGroupPython] Xe_element001  label="Xe_element : 1"  # scripted group (container) (typed FeaturePython)
  n = 1
  ref = Xe_element
FEATURE [App::DocumentObjectGroupPython] G4_Xe  # scripted group (container) (typed FeaturePython)
  Dunit = g/cm3
  Dvalue = 0.00548536
  Group = -> [Xe_element001]
  conduct = 2
  density = 1
  expand = 3
  formula = Xe
  name = G4_Xe
  specific = 4
FEATURE [App::DocumentObjectGroupPython] Cs_element003  label="Cs_element : 003"  # scripted group (container) (typed FeaturePython)
  n = 1
  ref = Cs_element
FEATURE [App::DocumentObjectGroupPython] G4_Cs  # scripted group (container) (typed FeaturePython)
  Dunit = g/cm3
  Dvalue = 1.873
  Group = -> [Cs_element003]
  conduct = 2
  density = 1
  expand = 3
  formula = Cs
  name = G4_Cs
  specific = 4
FEATURE [App::DocumentObjectGroupPython] Ba_element003  label="Ba_element : 003"  # scripted group (container) (typed FeaturePython)
  n = 1
  ref = Ba_element
FEATURE [App::DocumentObjectGroupPython] G4_Ba  # scripted group (container) (typed FeaturePython)
  Dunit = g/cm3
  Dvalue = 3.5
  Group = -> [Ba_element003]
  conduct = 2
  density = 1
  expand = 3
  formula = Ba
  name = G4_Ba
  specific = 4
FEATURE [App::DocumentObjectGroupPython] La_element003  label="La_element : 003"  # scripted group (container) (typed FeaturePython)
  n = 1
  ref = La_element
FEATURE [App::DocumentObjectGroupPython] G4_La  # scripted group (container) (typed FeaturePython)
  Dunit = g/cm3
  Dvalue = 6.154
  Group = -> [La_element003]
  conduct = 2
  density = 1
  expand = 3
  formula = La
  name = G4_La
  specific = 4
FEATURE [App::DocumentObjectGroupPython] Ce_element002  label="Ce_element : 1"  # scripted group (container) (typed FeaturePython)
  n = 1
  ref = Ce_element
FEATURE [App::DocumentObjectGroupPython] G4_Ce  # scripted group (container) (typed FeaturePython)
  Dunit = g/cm3
  Dvalue = 6.657
  Group = -> [Ce_element002]
  conduct = 2
  density = 1
  expand = 3
  formula = Ce
  name = G4_Ce
  specific = 4
FEATURE [App::DocumentObjectGroupPython] Pr_element001  label="Pr_element : 1"  # scripted group (container) (typed FeaturePython)
  n = 1
  ref = Pr_element
FEATURE [App::DocumentObjectGroupPython] G4_Pr  # scripted group (container) (typed FeaturePython)
  Dunit = g/cm3
  Dvalue = 6.71
  Group = -> [Pr_element001]
  conduct = 2
  density = 1
  expand = 3
  formula = Pr
  name = G4_Pr
  specific = 4
FEATURE [App::DocumentObjectGroupPython] Nd_element001  label="Nd_element : 1"  # scripted group (container) (typed FeaturePython)
  n = 1
  ref = Nd_element
FEATURE [App::DocumentObjectGroupPython] G4_Nd  # scripted group (container) (typed FeaturePython)
  Dunit = g/cm3
  Dvalue = 6.9
  Group = -> [Nd_element001]
  conduct = 2
  density = 1
  expand = 3
  formula = Nd
  name = G4_Nd
  specific = 4
FEATURE [App::DocumentObjectGroupPython] Pm_element001  label="Pm_element : 1"  # scripted group (container) (typed FeaturePython)
  n = 1
  ref = Pm_element
FEATURE [App::DocumentObjectGroupPython] G4_Pm  # scripted group (container) (typed FeaturePython)
  Dunit = g/cm3
  Dvalue = 7.22
  Group = -> [Pm_element001]
  conduct = 2
  density = 1
  expand = 3
  formula = Pm
  name = G4_Pm
  specific = 4
FEATURE [App::DocumentObjectGroupPython] Sm_element001  label="Sm_element : 1"  # scripted group (container) (typed FeaturePython)
  n = 1
  ref = Sm_element
FEATURE [App::DocumentObjectGroupPython] G4_Sm  # scripted group (container) (typed FeaturePython)
  Dunit = g/cm3
  Dvalue = 7.46
  Group = -> [Sm_element001]
  conduct = 2
  density = 1
  expand = 3
  formula = Sm
  name = G4_Sm
  specific = 4
FEATURE [App::DocumentObjectGroupPython] Eu_element001  label="Eu_element : 1"  # scripted group (container) (typed FeaturePython)
  n = 1
  ref = Eu_element
FEATURE [App::DocumentObjectGroupPython] G4_Eu  # scripted group (container) (typed FeaturePython)
  Dunit = g/cm3
  Dvalue = 5.243
  Group = -> [Eu_element001]
  conduct = 2
  density = 1
  expand = 3
  formula = Eu
  name = G4_Eu
  specific = 4
FEATURE [App::DocumentObjectGroupPython] Gd_element002  label="Gd_element : 1"  # scripted group (container) (typed FeaturePython)
  n = 1
  ref = Gd_element
FEATURE [App::DocumentObjectGroupPython] G4_Gd  # scripted group (container) (typed FeaturePython)
  Dunit = g/cm3
  Dvalue = 7.9004
  Group = -> [Gd_element002]
  conduct = 2
  density = 1
  expand = 3
  formula = Gd
  name = G4_Gd
  specific = 4
FEATURE [App::DocumentObjectGroupPython] Tb_element001  label="Tb_element : 1"  # scripted group (container) (typed FeaturePython)
  n = 1
  ref = Tb_element
FEATURE [App::DocumentObjectGroupPython] G4_Tb  # scripted group (container) (typed FeaturePython)
  Dunit = g/cm3
  Dvalue = 8.229
  Group = -> [Tb_element001]
  conduct = 2
  density = 1
  expand = 3
  formula = Tb
  name = G4_Tb
  specific = 4
FEATURE [App::DocumentObjectGroupPython] Dy_element001  label="Dy_element : 1"  # scripted group (container) (typed FeaturePython)
  n = 1
  ref = Dy_element
FEATURE [App::DocumentObjectGroupPython] G4_Dy  # scripted group (container) (typed FeaturePython)
  Dunit = g/cm3
  Dvalue = 8.55
  Group = -> [Dy_element001]
  conduct = 2
  density = 1
  expand = 3
  formula = Dy
  name = G4_Dy
  specific = 4
FEATURE [App::DocumentObjectGroupPython] Ho_element001  label="Ho_element : 1"  # scripted group (container) (typed FeaturePython)
  n = 1
  ref = Ho_element
FEATURE [App::DocumentObjectGroupPython] G4_Ho  # scripted group (container) (typed FeaturePython)
  Dunit = g/cm3
  Dvalue = 8.795
  Group = -> [Ho_element001]
  conduct = 2
  density = 1
  expand = 3
  formula = Ho
  name = G4_Ho
  specific = 4
FEATURE [App::DocumentObjectGroupPython] Er_element001  label="Er_element : 1"  # scripted group (container) (typed FeaturePython)
  n = 1
  ref = Er_element
FEATURE [App::DocumentObjectGroupPython] G4_Er  # scripted group (container) (typed FeaturePython)
  Dunit = g/cm3
  Dvalue = 9.066
  Group = -> [Er_element001]
  conduct = 2
  density = 1
  expand = 3
  formula = Er
  name = G4_Er
  specific = 4
FEATURE [App::DocumentObjectGroupPython] Tm_element001  label="Tm_element : 1"  # scripted group (container) (typed FeaturePython)
  n = 1
  ref = Tm_element
FEATURE [App::DocumentObjectGroupPython] G4_Tm  # scripted group (container) (typed FeaturePython)
  Dunit = g/cm3
  Dvalue = 9.321
  Group = -> [Tm_element001]
  conduct = 2
  density = 1
  expand = 3
  formula = Tm
  name = G4_Tm
  specific = 4
FEATURE [App::DocumentObjectGroupPython] Yb_element001  label="Yb_element : 1"  # scripted group (container) (typed FeaturePython)
  n = 1
  ref = Yb_element
FEATURE [App::DocumentObjectGroupPython] G4_Yb  # scripted group (container) (typed FeaturePython)
  Dunit = g/cm3
  Dvalue = 6.73
  Group = -> [Yb_element001]
  conduct = 2
  density = 1
  expand = 3
  formula = Yb
  name = G4_Yb
  specific = 4
FEATURE [App::DocumentObjectGroupPython] Lu_element001  label="Lu_element : 1"  # scripted group (container) (typed FeaturePython)
  n = 1
  ref = Lu_element
FEATURE [App::DocumentObjectGroupPython] G4_Lu  # scripted group (container) (typed FeaturePython)
  Dunit = g/cm3
  Dvalue = 9.84
  Group = -> [Lu_element001]
  conduct = 2
  density = 1
  expand = 3
  formula = Lu
  name = G4_Lu
  specific = 4
FEATURE [App::DocumentObjectGroupPython] Hf_element001  label="Hf_element : 1"  # scripted group (container) (typed FeaturePython)
  n = 1
  ref = Hf_element
FEATURE [App::DocumentObjectGroupPython] G4_Hf  # scripted group (container) (typed FeaturePython)
  Dunit = g/cm3
  Dvalue = 13.31
  Group = -> [Hf_element001]
  conduct = 2
  density = 1
  expand = 3
  formula = Hf
  name = G4_Hf
  specific = 4
FEATURE [App::DocumentObjectGroupPython] Ta_element001  label="Ta_element : 1"  # scripted group (container) (typed FeaturePython)
  n = 1
  ref = Ta_element
FEATURE [App::DocumentObjectGroupPython] G4_Ta  # scripted group (container) (typed FeaturePython)
  Dunit = g/cm3
  Dvalue = 16.654
  Group = -> [Ta_element001]
  conduct = 2
  density = 1
  expand = 3
  formula = Ta
  name = G4_Ta
  specific = 4
FEATURE [App::DocumentObjectGroupPython] W_element004  label="W_element : 004"  # scripted group (container) (typed FeaturePython)
  n = 1
  ref = W_element
FEATURE [App::DocumentObjectGroupPython] G4_W  # scripted group (container) (typed FeaturePython)
  Dunit = g/cm3
  Dvalue = 19.3
  Group = -> [W_element004]
  conduct = 2
  density = 1
  expand = 3
  formula = W
  name = G4_W
  specific = 4
FEATURE [App::DocumentObjectGroupPython] Re_element001  label="Re_element : 1"  # scripted group (container) (typed FeaturePython)
  n = 1
  ref = Re_element
FEATURE [App::DocumentObjectGroupPython] G4_Re  # scripted group (container) (typed FeaturePython)
  Dunit = g/cm3
  Dvalue = 21.02
  Group = -> [Re_element001]
  conduct = 2
  density = 1
  expand = 3
  formula = Re
  name = G4_Re
  specific = 4
FEATURE [App::DocumentObjectGroupPython] Os_element001  label="Os_element : 1"  # scripted group (container) (typed FeaturePython)
  n = 1
  ref = Os_element
FEATURE [App::DocumentObjectGroupPython] G4_Os  # scripted group (container) (typed FeaturePython)
  Dunit = g/cm3
  Dvalue = 22.57
  Group = -> [Os_element001]
  conduct = 2
  density = 1
  expand = 3
  formula = Os
  name = G4_Os
  specific = 4
FEATURE [App::DocumentObjectGroupPython] Ir_element001  label="Ir_element : 1"  # scripted group (container) (typed FeaturePython)
  n = 1
  ref = Ir_element
FEATURE [App::DocumentObjectGroupPython] G4_Ir  # scripted group (container) (typed FeaturePython)
  Dunit = g/cm3
  Dvalue = 22.42
  Group = -> [Ir_element001]
  conduct = 2
  density = 1
  expand = 3
  formula = Ir
  name = G4_Ir
  specific = 4
FEATURE [App::DocumentObjectGroupPython] Pt_element001  label="Pt_element : 1"  # scripted group (container) (typed FeaturePython)
  n = 1
  ref = Pt_element
FEATURE [App::DocumentObjectGroupPython] G4_Pt  # scripted group (container) (typed FeaturePython)
  Dunit = g/cm3
  Dvalue = 21.45
  Group = -> [Pt_element001]
  conduct = 2
  density = 1
  expand = 3
  formula = Pt
  name = G4_Pt
  specific = 4
FEATURE [App::DocumentObjectGroupPython] Au_element001  label="Au_element : 1"  # scripted group (container) (typed FeaturePython)
  n = 1
  ref = Au_element
FEATURE [App::DocumentObjectGroupPython] G4_Au  # scripted group (container) (typed FeaturePython)
  Dunit = g/cm3
  Dvalue = 19.32
  Group = -> [Au_element001]
  conduct = 2
  density = 1
  expand = 3
  formula = Au
  name = G4_Au
  specific = 4
FEATURE [App::DocumentObjectGroupPython] Hg_element002  label="Hg_element : 002"  # scripted group (container) (typed FeaturePython)
  n = 1
  ref = Hg_element
FEATURE [App::DocumentObjectGroupPython] G4_Hg  # scripted group (container) (typed FeaturePython)
  Dunit = g/cm3
  Dvalue = 13.546
  Group = -> [Hg_element002]
  conduct = 2
  density = 1
  expand = 3
  formula = Hg
  name = G4_Hg
  specific = 4
FEATURE [App::DocumentObjectGroupPython] Tl_element002  label="Tl_element : 002"  # scripted group (container) (typed FeaturePython)
  n = 1
  ref = Tl_element
FEATURE [App::DocumentObjectGroupPython] G4_Tl  # scripted group (container) (typed FeaturePython)
  Dunit = g/cm3
  Dvalue = 11.72
  Group = -> [Tl_element002]
  conduct = 2
  density = 1
  expand = 3
  formula = Tl
  name = G4_Tl
  specific = 4
FEATURE [App::DocumentObjectGroupPython] Pb_element003  label="Pb_element : 1"  # scripted group (container) (typed FeaturePython)
  n = 1
  ref = Pb_element
FEATURE [App::DocumentObjectGroupPython] G4_Pb  # scripted group (container) (typed FeaturePython)
  Dunit = g/cm3
  Dvalue = 11.35
  Group = -> [Pb_element003]
  conduct = 2
  density = 1
  expand = 3
  formula = Pb
  name = G4_Pb
  specific = 4
FEATURE [App::DocumentObjectGroupPython] Bi_element002  label="Bi_element : 1"  # scripted group (container) (typed FeaturePython)
  n = 1
  ref = Bi_element
FEATURE [App::DocumentObjectGroupPython] G4_Bi  # scripted group (container) (typed FeaturePython)
  Dunit = g/cm3
  Dvalue = 9.747
  Group = -> [Bi_element002]
  conduct = 2
  density = 1
  expand = 3
  formula = Bi
  name = G4_Bi
  specific = 4
FEATURE [App::DocumentObjectGroupPython] Po_element001  label="Po_element : 1"  # scripted group (container) (typed FeaturePython)
  n = 1
  ref = Po_element
FEATURE [App::DocumentObjectGroupPython] G4_Po  # scripted group (container) (typed FeaturePython)
  Dunit = g/cm3
  Dvalue = 9.32
  Group = -> [Po_element001]
  conduct = 2
  density = 1
  expand = 3
  formula = Po
  name = G4_Po
  specific = 4
FEATURE [App::DocumentObjectGroupPython] At_element001  label="At_element : 1"  # scripted group (container) (typed FeaturePython)
  n = 1
  ref = At_element
FEATURE [App::DocumentObjectGroupPython] G4_At  # scripted group (container) (typed FeaturePython)
  Dunit = g/cm3
  Dvalue = 9.32
  Group = -> [At_element001]
  conduct = 2
  density = 1
  expand = 3
  formula = At
  name = G4_At
  specific = 4
FEATURE [App::DocumentObjectGroupPython] Rn_element001  label="Rn_element : 1"  # scripted group (container) (typed FeaturePython)
  n = 1
  ref = Rn_element
FEATURE [App::DocumentObjectGroupPython] G4_Rn  # scripted group (container) (typed FeaturePython)
  Dunit = g/cm3
  Dvalue = 0.00900662
  Group = -> [Rn_element001]
  conduct = 2
  density = 1
  expand = 3
  formula = Rn
  name = G4_Rn
  specific = 4
FEATURE [App::DocumentObjectGroupPython] Fr_element001  label="Fr_element : 1"  # scripted group (container) (typed FeaturePython)
  n = 1
  ref = Fr_element
FEATURE [App::DocumentObjectGroupPython] G4_Fr  # scripted group (container) (typed FeaturePython)
  Dunit = g/cm3
  Dvalue = 1
  Group = -> [Fr_element001]
  conduct = 2
  density = 1
  expand = 3
  formula = Fr
  name = G4_Fr
  specific = 4
FEATURE [App::DocumentObjectGroupPython] Ra_element001  label="Ra_element : 1"  # scripted group (container) (typed FeaturePython)
  n = 1
  ref = Ra_element
FEATURE [App::DocumentObjectGroupPython] G4_Ra  # scripted group (container) (typed FeaturePython)
  Dunit = g/cm3
  Dvalue = 5
  Group = -> [Ra_element001]
  conduct = 2
  density = 1
  expand = 3
  formula = Ra
  name = G4_Ra
  specific = 4
FEATURE [App::DocumentObjectGroupPython] Ac_element001  label="Ac_element : 1"  # scripted group (container) (typed FeaturePython)
  n = 1
  ref = Ac_element
FEATURE [App::DocumentObjectGroupPython] G4_Ac  # scripted group (container) (typed FeaturePython)
  Dunit = g/cm3
  Dvalue = 10.07
  Group = -> [Ac_element001]
  conduct = 2
  density = 1
  expand = 3
  formula = Ac
  name = G4_Ac
  specific = 4
FEATURE [App::DocumentObjectGroupPython] Th_element001  label="Th_element : 1"  # scripted group (container) (typed FeaturePython)
  n = 1
  ref = Th_element
FEATURE [App::DocumentObjectGroupPython] G4_Th  # scripted group (container) (typed FeaturePython)
  Dunit = g/cm3
  Dvalue = 11.72
  Group = -> [Th_element001]
  conduct = 2
  density = 1
  expand = 3
  formula = Th
  name = G4_Th
  specific = 4
FEATURE [App::DocumentObjectGroupPython] Pa_element001  label="Pa_element : 1"  # scripted group (container) (typed FeaturePython)
  n = 1
  ref = Pa_element
FEATURE [App::DocumentObjectGroupPython] G4_Pa  # scripted group (container) (typed FeaturePython)
  Dunit = g/cm3
  Dvalue = 15.37
  Group = -> [Pa_element001]
  conduct = 2
  density = 1
  expand = 3
  formula = Pa
  name = G4_Pa
  specific = 4
FEATURE [App::DocumentObjectGroupPython] U_element004  label="U_element : 004"  # scripted group (container) (typed FeaturePython)
  n = 1
  ref = U_element
FEATURE [App::DocumentObjectGroupPython] G4_U  # scripted group (container) (typed FeaturePython)
  Dunit = g/cm3
  Dvalue = 18.95
  Group = -> [U_element004]
  conduct = 2
  density = 1
  expand = 3
  formula = U
  name = G4_U
  specific = 4
FEATURE [App::DocumentObjectGroupPython] Np_element001  label="Np_element : 1"  # scripted group (container) (typed FeaturePython)
  n = 1
  ref = Np_element
FEATURE [App::DocumentObjectGroupPython] G4_Np  # scripted group (container) (typed FeaturePython)
  Dunit = g/cm3
  Dvalue = 20.25
  Group = -> [Np_element001]
  conduct = 2
  density = 1
  expand = 3
  formula = Np
  name = G4_Np
  specific = 4
FEATURE [App::DocumentObjectGroupPython] Pu_element002  label="Pu_element : 002"  # scripted group (container) (typed FeaturePython)
  n = 1
  ref = Pu_element
FEATURE [App::DocumentObjectGroupPython] G4_Pu  # scripted group (container) (typed FeaturePython)
  Dunit = g/cm3
  Dvalue = 19.84
  Group = -> [Pu_element002]
  conduct = 2
  density = 1
  expand = 3
  formula = Pu
  name = G4_Pu
  specific = 4
FEATURE [App::DocumentObjectGroupPython] Am_element001  label="Am_element : 1"  # scripted group (container) (typed FeaturePython)
  n = 1
  ref = Am_element
FEATURE [App::DocumentObjectGroupPython] G4_Am  # scripted group (container) (typed FeaturePython)
  Dunit = g/cm3
  Dvalue = 13.67
  Group = -> [Am_element001]
  conduct = 2
  density = 1
  expand = 3
  formula = Am
  name = G4_Am
  specific = 4
FEATURE [App::DocumentObjectGroupPython] Cm_element001  label="Cm_element : 1"  # scripted group (container) (typed FeaturePython)
  n = 1
  ref = Cm_element
FEATURE [App::DocumentObjectGroupPython] G4_Cm  # scripted group (container) (typed FeaturePython)
  Dunit = g/cm3
  Dvalue = 13.51
  Group = -> [Cm_element001]
  conduct = 2
  density = 1
  expand = 3
  formula = Cm
  name = G4_Cm
  specific = 4
FEATURE [App::DocumentObjectGroupPython] Bk_element001  label="Bk_element : 1"  # scripted group (container) (typed FeaturePython)
  n = 1
  ref = Bk_element
FEATURE [App::DocumentObjectGroupPython] G4_Bk  # scripted group (container) (typed FeaturePython)
  Dunit = g/cm3
  Dvalue = 14
  Group = -> [Bk_element001]
  conduct = 2
  density = 1
  expand = 3
  formula = Bk
  name = G4_Bk
  specific = 4
FEATURE [App::DocumentObjectGroupPython] Cf_element001  label="Cf_element : 1"  # scripted group (container) (typed FeaturePython)
  n = 1
  ref = Cf_element
FEATURE [App::DocumentObjectGroupPython] G4_Cf  # scripted group (container) (typed FeaturePython)
  Dunit = g/cm3
  Dvalue = 10
  Group = -> [Cf_element001]
  conduct = 2
  density = 1
  expand = 3
  formula = Cf
  name = G4_Cf
  specific = 4
FEATURE [App::DocumentObjectGroupPython] Element  # scripted group (container) (typed FeaturePython)
  Group = -> [G4_H,G4_He,G4_Li,G4_Be,G4_B,G4_C,G4_N,G4_O,G4_F,G4_Ne,G4_Na,G4_Mg,G4_Al,G4_Si,G4_P,G4_S,G4_Cl,G4_Ar,G4_K,G4_Ca,G4_Sc,G4_Ti,G4_V,G4_Cr,G4_Mn,G4_Fe,G4_Co,G4_Ni,G4_Cu,G4_Zn,G4_Ga,G4_Ge,G4_As,G4_Se,G4_Br,G4_Kr,G4_Rb,G4_Sr,G4_Y,G4_Zr,G4_Nb,G4_Mo,G4_Tc,G4_Ru,G4_Rh,G4_Pd,G4_Ag,G4_Cd,G4_In,G4_Sn,G4_Sb,G4_Te,G4_I,G4_Xe,G4_Cs,G4_Ba,G4_La,G4_Ce,G4_Pr,G4_Nd,G4_Pm,G4_Sm,G4_Eu,G4_Gd,G4_Tb,G4_Dy,G4_Ho,G4_Er,+30 more]
FEATURE [App::DocumentObjectGroupPython] H_element114  label="H_element : 063"  # scripted group (container) (typed FeaturePython)
  n = 2
  ref = H_element
FEATURE [App::DocumentObjectGroupPython] G4_lH2  # scripted group (container) (typed FeaturePython)
  Dunit = g/cm3
  Dvalue = 0.0708
  Group = -> [H_element114]
  conduct = 2
  density = 1
  expand = 3
  formula = G4_lH2
  name = G4_lH2
  specific = 4
FEATURE [App::DocumentObjectGroupPython] N_element049  label="N_element : 022"  # scripted group (container) (typed FeaturePython)
  n = 2
  ref = N_element
FEATURE [App::DocumentObjectGroupPython] G4_lN2  # scripted group (container) (typed FeaturePython)
  Dunit = g/cm3
  Dvalue = 0.807
  Group = -> [N_element049]
  conduct = 2
  density = 1
  expand = 3
  formula = G4_lN2
  name = G4_lN2
  specific = 4
FEATURE [App::DocumentObjectGroupPython] O_element106  label="O_element : 060"  # scripted group (container) (typed FeaturePython)
  n = 2
  ref = O_element
FEATURE [App::DocumentObjectGroupPython] G4_lO2  # scripted group (container) (typed FeaturePython)
  Dunit = g/cm3
  Dvalue = 1.141
  Group = -> [O_element106]
  conduct = 2
  density = 1
  expand = 3
  formula = G4_lO2
  name = G4_lO2
  specific = 4
FEATURE [App::DocumentObjectGroupPython] Ar  label="Ar : 1"  # scripted group (container) (typed FeaturePython)
  n = 1
  ref = Ar
FEATURE [App::DocumentObjectGroupPython] G4_lAr  # scripted group (container) (typed FeaturePython)
  Dunit = g/cm3
  Dvalue = 1.396
  Group = -> [Ar]
  conduct = 2
  density = 1
  expand = 3
  formula = G4_lAr
  name = G4_lAr
  specific = 4
FEATURE [App::DocumentObjectGroupPython] Br  label="Br : 1"  # scripted group (container) (typed FeaturePython)
  n = 1
  ref = Br
FEATURE [App::DocumentObjectGroupPython] G4_lBr  # scripted group (container) (typed FeaturePython)
  Dunit = g/cm3
  Dvalue = 3.1028
  Group = -> [Br]
  conduct = 2
  density = 1
  expand = 3
  formula = G4_lBr
  name = G4_lBr
  specific = 4
FEATURE [App::DocumentObjectGroupPython] Kr  label="Kr : 1"  # scripted group (container) (typed FeaturePython)
  n = 1
  ref = Kr
FEATURE [App::DocumentObjectGroupPython] G4_lKr  # scripted group (container) (typed FeaturePython)
  Dunit = g/cm3
  Dvalue = 2.418
  Group = -> [Kr]
  conduct = 2
  density = 1
  expand = 3
  formula = G4_lKr
  name = G4_lKr
  specific = 4
FEATURE [App::DocumentObjectGroupPython] Xe  label="Xe : 1"  # scripted group (container) (typed FeaturePython)
  n = 1
  ref = Xe
FEATURE [App::DocumentObjectGroupPython] G4_lXe  # scripted group (container) (typed FeaturePython)
  Dunit = g/cm3
  Dvalue = 2.953
  Group = -> [Xe]
  conduct = 2
  density = 1
  expand = 3
  formula = G4_lXe
  name = G4_lXe
  specific = 4
FEATURE [App::DocumentObjectGroupPython] O_element107  label="O_element : 061"  # scripted group (container) (typed FeaturePython)
  n = 4
  ref = O_element
FEATURE [App::DocumentObjectGroupPython] Pb_element004  label="Pb_element : 002"  # scripted group (container) (typed FeaturePython)
  n = 1
  ref = Pb_element
FEATURE [App::DocumentObjectGroupPython] W_element005  label="W_element : 005"  # scripted group (container) (typed FeaturePython)
  n = 1
  ref = W_element
FEATURE [App::DocumentObjectGroupPython] G4_PbWO4  # scripted group (container) (typed FeaturePython)
  Dunit = g/cm3
  Dvalue = 8.28
  Group = -> [O_element107,Pb_element004,W_element005]
  conduct = 2
  density = 1
  expand = 3
  formula = G4_PbWO4
  name = G4_PbWO4
  specific = 4
FEATURE [App::DocumentObjectGroupPython] alactic  label="alactic : 1"  # scripted group (container) (typed FeaturePython)
  n = 1
  ref = alactic
FEATURE [App::DocumentObjectGroupPython] G4_Galactic  # scripted group (container) (typed FeaturePython)
  Dunit = g/cm3
  Dvalue = 0
  Group = -> [alactic]
  conduct = 2
  density = 1
  expand = 3
  formula = G4_Galactic
  name = G4_Galactic
  specific = 4
FEATURE [App::DocumentObjectGroupPython] RAPHITE_POROUS  label="RAPHITE_POROUS : 1"  # scripted group (container) (typed FeaturePython)
  n = 1
  ref = RAPHITE_POROUS
FEATURE [App::DocumentObjectGroupPython] G4_GRAPHITE_POROUS  # scripted group (container) (typed FeaturePython)
  Dunit = g/cm3
  Dvalue = 1.7
  Group = -> [RAPHITE_POROUS]
  conduct = 2
  density = 1
  expand = 3
  formula = G4_GRAPHITE_POROUS
  name = G4_GRAPHITE_POROUS
  specific = 4
FEATURE [App::DocumentObjectGroupPython] H_element115  label="H_element : 0.150"  # scripted group (container) (typed FeaturePython)
  n = 0.080538
FEATURE [App::DocumentObjectGroupPython] C_element125  label="C_element : 0.600"  # scripted group (container) (typed FeaturePython)
  n = 0.599848
FEATURE [App::DocumentObjectGroupPython] O_element108  label="O_element : 0.320"  # scripted group (container) (typed FeaturePython)
  n = 0.319614
FEATURE [App::DocumentObjectGroupPython] G4_LUCITE  # scripted group (container) (typed FeaturePython)
  Dunit = g/cm3
  Dvalue = 1.19
  Group = -> [H_element115,C_element125,O_element108]
  conduct = 2
  density = 1
  expand = 3
  formula = G4_LUCITE
  name = G4_LUCITE
  specific = 4
FEATURE [App::DocumentObjectGroupPython] Cu_element002  label="Cu_element : 62"  # scripted group (container) (typed FeaturePython)
  n = 62
  ref = Cu_element
FEATURE [App::DocumentObjectGroupPython] Zn_element002  label="Zn_element : 35"  # scripted group (container) (typed FeaturePython)
  n = 35
  ref = Zn_element
FEATURE [App::DocumentObjectGroupPython] Pb_element005  label="Pb_element : 3"  # scripted group (container) (typed FeaturePython)
  n = 3
  ref = Pb_element
FEATURE [App::DocumentObjectGroupPython] G4_BRASS  # scripted group (container) (typed FeaturePython)
  Dunit = g/cm3
  Dvalue = 8.52
  Group = -> [Cu_element002,Zn_element002,Pb_element005]
  conduct = 2
  density = 1
  expand = 3
  formula = G4_BRASS
  name = G4_BRASS
  specific = 4
FEATURE [App::DocumentObjectGroupPython] Cu_element003  label="Cu_element : 89"  # scripted group (container) (typed FeaturePython)
  n = 89
  ref = Cu_element
FEATURE [App::DocumentObjectGroupPython] Zn_element003  label="Zn_element : 9"  # scripted group (container) (typed FeaturePython)
  n = 9
  ref = Zn_element
FEATURE [App::DocumentObjectGroupPython] Pb_element006  label="Pb_element : 2"  # scripted group (container) (typed FeaturePython)
  n = 2
  ref = Pb_element
FEATURE [App::DocumentObjectGroupPython] G4_BRONZE  # scripted group (container) (typed FeaturePython)
  Dunit = g/cm3
  Dvalue = 8.82
  Group = -> [Cu_element003,Zn_element003,Pb_element006]
  conduct = 2
  density = 1
  expand = 3
  formula = G4_BRONZE
  name = G4_BRONZE
  specific = 4
FEATURE [App::DocumentObjectGroupPython] Fe_element008  label="Fe_element : 74"  # scripted group (container) (typed FeaturePython)
  n = 74
  ref = Fe_element
FEATURE [App::DocumentObjectGroupPython] Cr_element002  label="Cr_element : 18"  # scripted group (container) (typed FeaturePython)
  n = 18
  ref = Cr_element
FEATURE [App::DocumentObjectGroupPython] Ni_element002  label="Ni_element : 8"  # scripted group (container) (typed FeaturePython)
  n = 8
  ref = Ni_element
FEATURE [App::DocumentObjectGroupPython] G4_STAINLESS_STEEL  label="G4_STAINLESS-STEEL"  # scripted group (container) (typed FeaturePython)
  Dunit = g/cm3
  Dvalue = 8
  Group = -> [Fe_element008,Cr_element002,Ni_element002]
  conduct = 2
  density = 1
  expand = 3
  formula = G4_STAINLESS-STEEL
  name = G4_STAINLESS-STEEL
  specific = 4
FEATURE [App::DocumentObjectGroupPython] H_element116  label="H_element : 064"  # scripted group (container) (typed FeaturePython)
  n = 18
  ref = H_element
FEATURE [App::DocumentObjectGroupPython] C_element126  label="C_element : 071"  # scripted group (container) (typed FeaturePython)
  n = 12
  ref = C_element
FEATURE [App::DocumentObjectGroupPython] O_element109  label="O_element : 062"  # scripted group (container) (typed FeaturePython)
  n = 7
  ref = O_element
FEATURE [App::DocumentObjectGroupPython] G4_CR39  # scripted group (container) (typed FeaturePython)
  Dunit = g/cm3
  Dvalue = 1.32
  Group = -> [H_element116,C_element126,O_element109]
  conduct = 2
  density = 1
  expand = 3
  formula = G4_CR39
  name = G4_CR39
  specific = 4
FEATURE [App::DocumentObjectGroupPython] H_element117  label="H_element : 38"  # scripted group (container) (typed FeaturePython)
  n = 38
  ref = H_element
FEATURE [App::DocumentObjectGroupPython] C_element127  label="C_element : 072"  # scripted group (container) (typed FeaturePython)
  n = 18
  ref = C_element
FEATURE [App::DocumentObjectGroupPython] O_element110  label="O_element : 063"  # scripted group (container) (typed FeaturePython)
  n = 1
  ref = O_element
FEATURE [App::DocumentObjectGroupPython] G4_OCTADECANOL  # scripted group (container) (typed FeaturePython)
  Dunit = g/cm3
  Dvalue = 0.812
  Group = -> [H_element117,C_element127,O_element110]
  conduct = 2
  density = 1
  expand = 3
  formula = G4_OCTADECANOL
  name = G4_OCTADECANOL
  specific = 4
FEATURE [App::DocumentObjectGroupPython] HEP  # scripted group (container) (typed FeaturePython)
  Group = -> [G4_lH2,G4_lN2,G4_lO2,G4_lAr,G4_lBr,G4_lKr,G4_lXe,G4_PbWO4,G4_Galactic,G4_GRAPHITE_POROUS,G4_LUCITE,G4_BRASS,G4_BRONZE,G4_STAINLESS_STEEL,G4_CR39,G4_OCTADECANOL]
FEATURE [App::DocumentObjectGroupPython] C_element128  label="C_element : 073"  # scripted group (container) (typed FeaturePython)
  n = 14
  ref = C_element
FEATURE [App::DocumentObjectGroupPython] H_element118  label="H_element : 065"  # scripted group (container) (typed FeaturePython)
  n = 10
  ref = H_element
FEATURE [App::DocumentObjectGroupPython] O_element111  label="O_element : 064"  # scripted group (container) (typed FeaturePython)
  n = 2
  ref = O_element
FEATURE [App::DocumentObjectGroupPython] N_element050  label="N_element : 023"  # scripted group (container) (typed FeaturePython)
  n = 2
  ref = N_element
FEATURE [App::DocumentObjectGroupPython] G4_KEVLAR  # scripted group (container) (typed FeaturePython)
  Dunit = g/cm3
  Dvalue = 1.44
  Group = -> [C_element128,H_element118,O_element111,N_element050]
  conduct = 2
  density = 1
  expand = 3
  formula = G4_KEVLAR
  name = G4_KEVLAR
  specific = 4
FEATURE [App::DocumentObjectGroupPython] C_element129  label="C_element : 074"  # scripted group (container) (typed FeaturePython)
  n = 10
  ref = C_element
FEATURE [App::DocumentObjectGroupPython] H_element119  label="H_element : 066"  # scripted group (container) (typed FeaturePython)
  n = 8
  ref = H_element
FEATURE [App::DocumentObjectGroupPython] O_element112  label="O_element : 065"  # scripted group (container) (typed FeaturePython)
  n = 4
  ref = O_element
FEATURE [App::DocumentObjectGroupPython] G4_DACRON  # scripted group (container) (typed FeaturePython)
  Dunit = g/cm3
  Dvalue = 1.4
  Group = -> [C_element129,H_element119,O_element112]
  conduct = 2
  density = 1
  expand = 3
  formula = G4_DACRON
  name = G4_DACRON
  specific = 4
FEATURE [App::DocumentObjectGroupPython] C_element130  label="C_element : 075"  # scripted group (container) (typed FeaturePython)
  n = 4
  ref = C_element
FEATURE [App::DocumentObjectGroupPython] H_element120  label="H_element : 067"  # scripted group (container) (typed FeaturePython)
  n = 5
  ref = H_element
FEATURE [App::DocumentObjectGroupPython] Cl_element030  label="Cl_element : 016"  # scripted group (container) (typed FeaturePython)
  n = 1
  ref = Cl_element
FEATURE [App::DocumentObjectGroupPython] G4_NEOPRENE  # scripted group (container) (typed FeaturePython)
  Dunit = g/cm3
  Dvalue = 1.23
  Group = -> [C_element130,H_element120,Cl_element030]
  conduct = 2
  density = 1
  expand = 3
  formula = G4_NEOPRENE
  name = G4_NEOPRENE
  specific = 4
FEATURE [App::DocumentObjectGroupPython] Space  # scripted group (container) (typed FeaturePython)
  Group = -> [G4_KEVLAR,G4_DACRON,G4_NEOPRENE]
FEATURE [App::DocumentObjectGroupPython] H_element121  label="H_element : 068"  # scripted group (container) (typed FeaturePython)
  n = 5
  ref = H_element
FEATURE [App::DocumentObjectGroupPython] C_element131  label="C_element : 076"  # scripted group (container) (typed FeaturePython)
  n = 4
  ref = C_element
FEATURE [App::DocumentObjectGroupPython] N_element051  label="N_element : 3"  # scripted group (container) (typed FeaturePython)
  n = 3
  ref = N_element
FEATURE [App::DocumentObjectGroupPython] O_element113  label="O_element : 066"  # scripted group (container) (typed FeaturePython)
  n = 1
  ref = O_element
FEATURE [App::DocumentObjectGroupPython] G4_CYTOSINE  # scripted group (container) (typed FeaturePython)
  Dunit = g/cm3
  Dvalue = 1.55
  Group = -> [H_element121,C_element131,N_element051,O_element113]
  conduct = 2
  density = 1
  expand = 3
  formula = G4_CYTOSINE
  name = G4_CYTOSINE
  specific = 4
FEATURE [App::DocumentObjectGroupPython] H_element122  label="H_element : 069"  # scripted group (container) (typed FeaturePython)
  n = 6
  ref = H_element
FEATURE [App::DocumentObjectGroupPython] C_element132  label="C_element : 077"  # scripted group (container) (typed FeaturePython)
  n = 5
  ref = C_element
FEATURE [App::DocumentObjectGroupPython] N_element052  label="N_element : 024"  # scripted group (container) (typed FeaturePython)
  n = 2
  ref = N_element
FEATURE [App::DocumentObjectGroupPython] O_element114  label="O_element : 067"  # scripted group (container) (typed FeaturePython)
  n = 2
  ref = O_element
FEATURE [App::DocumentObjectGroupPython] G4_THYMINE  # scripted group (container) (typed FeaturePython)
  Dunit = g/cm3
  Dvalue = 1.23
  Group = -> [H_element122,C_element132,N_element052,O_element114]
  conduct = 2
  density = 1
  expand = 3
  formula = G4_THYMINE
  name = G4_THYMINE
  specific = 4
FEATURE [App::DocumentObjectGroupPython] H_element123  label="H_element : 070"  # scripted group (container) (typed FeaturePython)
  n = 4
  ref = H_element
FEATURE [App::DocumentObjectGroupPython] C_element133  label="C_element : 078"  # scripted group (container) (typed FeaturePython)
  n = 4
  ref = C_element
FEATURE [App::DocumentObjectGroupPython] N_element053  label="N_element : 025"  # scripted group (container) (typed FeaturePython)
  n = 2
  ref = N_element
FEATURE [App::DocumentObjectGroupPython] O_element115  label="O_element : 068"  # scripted group (container) (typed FeaturePython)
  n = 2
  ref = O_element
FEATURE [App::DocumentObjectGroupPython] G4_URACIL  # scripted group (container) (typed FeaturePython)
  Dunit = g/cm3
  Dvalue = 1.32
  Group = -> [H_element123,C_element133,N_element053,O_element115]
  conduct = 2
  density = 1
  expand = 3
  formula = G4_URACIL
  name = G4_URACIL
  specific = 4
FEATURE [App::DocumentObjectGroupPython] H_element124  label="H_element : 071"  # scripted group (container) (typed FeaturePython)
  n = 4
  ref = H_element
FEATURE [App::DocumentObjectGroupPython] C_element134  label="C_element : 079"  # scripted group (container) (typed FeaturePython)
  n = 5
  ref = C_element
FEATURE [App::DocumentObjectGroupPython] N_element054  label="N_element : 026"  # scripted group (container) (typed FeaturePython)
  n = 5
  ref = N_element
FEATURE [App::DocumentObjectGroupPython] G4_DNA_ADENINE  # scripted group (container) (typed FeaturePython)
  Dunit = g/cm3
  Dvalue = 1
  Group = -> [H_element124,C_element134,N_element054]
  conduct = 2
  density = 1
  expand = 3
  formula = G4_DNA_ADENINE
  name = G4_DNA_ADENINE
  specific = 4
FEATURE [App::DocumentObjectGroupPython] H_element125  label="H_element : 072"  # scripted group (container) (typed FeaturePython)
  n = 4
  ref = H_element
FEATURE [App::DocumentObjectGroupPython] C_element135  label="C_element : 080"  # scripted group (container) (typed FeaturePython)
  n = 5
  ref = C_element
FEATURE [App::DocumentObjectGroupPython] N_element055  label="N_element : 027"  # scripted group (container) (typed FeaturePython)
  n = 5
  ref = N_element
FEATURE [App::DocumentObjectGroupPython] O_element116  label="O_element : 069"  # scripted group (container) (typed FeaturePython)
  n = 1
  ref = O_element
FEATURE [App::DocumentObjectGroupPython] G4_DNA_GUANINE  # scripted group (container) (typed FeaturePython)
  Dunit = g/cm3
  Dvalue = 1
  Group = -> [H_element125,C_element135,N_element055,O_element116]
  conduct = 2
  density = 1
  expand = 3
  formula = G4_DNA_GUANINE
  name = G4_DNA_GUANINE
  specific = 4
FEATURE [App::DocumentObjectGroupPython] H_element126  label="H_element : 073"  # scripted group (container) (typed FeaturePython)
  n = 4
  ref = H_element
FEATURE [App::DocumentObjectGroupPython] C_element136  label="C_element : 081"  # scripted group (container) (typed FeaturePython)
  n = 4
  ref = C_element
FEATURE [App::DocumentObjectGroupPython] N_element056  label="N_element : 028"  # scripted group (container) (typed FeaturePython)
  n = 3
  ref = N_element
FEATURE [App::DocumentObjectGroupPython] O_element117  label="O_element : 070"  # scripted group (container) (typed FeaturePython)
  n = 1
  ref = O_element
FEATURE [App::DocumentObjectGroupPython] G4_DNA_CYTOSINE  # scripted group (container) (typed FeaturePython)
  Dunit = g/cm3
  Dvalue = 1
  Group = -> [H_element126,C_element136,N_element056,O_element117]
  conduct = 2
  density = 1
  expand = 3
  formula = G4_DNA_CYTOSINE
  name = G4_DNA_CYTOSINE
  specific = 4
FEATURE [App::DocumentObjectGroupPython] H_element127  label="H_element : 074"  # scripted group (container) (typed FeaturePython)
  n = 5
  ref = H_element
FEATURE [App::DocumentObjectGroupPython] C_element137  label="C_element : 082"  # scripted group (container) (typed FeaturePython)
  n = 5
  ref = C_element
FEATURE [App::DocumentObjectGroupPython] N_element057  label="N_element : 029"  # scripted group (container) (typed FeaturePython)
  n = 2
  ref = N_element
FEATURE [App::DocumentObjectGroupPython] O_element118  label="O_element : 071"  # scripted group (container) (typed FeaturePython)
  n = 2
  ref = O_element
FEATURE [App::DocumentObjectGroupPython] G4_DNA_THYMINE  # scripted group (container) (typed FeaturePython)
  Dunit = g/cm3
  Dvalue = 1
  Group = -> [H_element127,C_element137,N_element057,O_element118]
  conduct = 2
  density = 1
  expand = 3
  formula = G4_DNA_THYMINE
  name = G4_DNA_THYMINE
  specific = 4
FEATURE [App::DocumentObjectGroupPython] H_element128  label="H_element : 075"  # scripted group (container) (typed FeaturePython)
  n = 3
  ref = H_element
FEATURE [App::DocumentObjectGroupPython] C_element138  label="C_element : 083"  # scripted group (container) (typed FeaturePython)
  n = 4
  ref = C_element
FEATURE [App::DocumentObjectGroupPython] N_element058  label="N_element : 030"  # scripted group (container) (typed FeaturePython)
  n = 2
  ref = N_element
FEATURE [App::DocumentObjectGroupPython] O_element119  label="O_element : 072"  # scripted group (container) (typed FeaturePython)
  n = 2
  ref = O_element
FEATURE [App::DocumentObjectGroupPython] G4_DNA_URACIL  # scripted group (container) (typed FeaturePython)
  Dunit = g/cm3
  Dvalue = 1
  Group = -> [H_element128,C_element138,N_element058,O_element119]
  conduct = 2
  density = 1
  expand = 3
  formula = G4_DNA_URACIL
  name = G4_DNA_URACIL
  specific = 4
FEATURE [App::DocumentObjectGroupPython] H_element129  label="H_element : 076"  # scripted group (container) (typed FeaturePython)
  n = 10
  ref = H_element
FEATURE [App::DocumentObjectGroupPython] C_element139  label="C_element : 084"  # scripted group (container) (typed FeaturePython)
  n = 10
  ref = C_element
FEATURE [App::DocumentObjectGroupPython] N_element059  label="N_element : 031"  # scripted group (container) (typed FeaturePython)
  n = 5
  ref = N_element
FEATURE [App::DocumentObjectGroupPython] O_element120  label="O_element : 073"  # scripted group (container) (typed FeaturePython)
  n = 4
  ref = O_element
FEATURE [App::DocumentObjectGroupPython] G4_DNA_ADENOSINE  # scripted group (container) (typed FeaturePython)
  Dunit = g/cm3
  Dvalue = 1
  Group = -> [H_element129,C_element139,N_element059,O_element120]
  conduct = 2
  density = 1
  expand = 3
  formula = G4_DNA_ADENOSINE
  name = G4_DNA_ADENOSINE
  specific = 4
FEATURE [App::DocumentObjectGroupPython] H_element130  label="H_element : 077"  # scripted group (container) (typed FeaturePython)
  n = 10
  ref = H_element
FEATURE [App::DocumentObjectGroupPython] C_element140  label="C_element : 085"  # scripted group (container) (typed FeaturePython)
  n = 10
  ref = C_element
FEATURE [App::DocumentObjectGroupPython] N_element060  label="N_element : 032"  # scripted group (container) (typed FeaturePython)
  n = 5
  ref = N_element
FEATURE [App::DocumentObjectGroupPython] O_element121  label="O_element : 074"  # scripted group (container) (typed FeaturePython)
  n = 5
  ref = O_element
FEATURE [App::DocumentObjectGroupPython] G4_DNA_GUANOSINE  # scripted group (container) (typed FeaturePython)
  Dunit = g/cm3
  Dvalue = 1
  Group = -> [H_element130,C_element140,N_element060,O_element121]
  conduct = 2
  density = 1
  expand = 3
  formula = G4_DNA_GUANOSINE
  name = G4_DNA_GUANOSINE
  specific = 4
FEATURE [App::DocumentObjectGroupPython] H_element131  label="H_element : 078"  # scripted group (container) (typed FeaturePython)
  n = 10
  ref = H_element
FEATURE [App::DocumentObjectGroupPython] C_element141  label="C_element : 086"  # scripted group (container) (typed FeaturePython)
  n = 9
  ref = C_element
FEATURE [App::DocumentObjectGroupPython] N_element061  label="N_element : 033"  # scripted group (container) (typed FeaturePython)
  n = 3
  ref = N_element
FEATURE [App::DocumentObjectGroupPython] O_element122  label="O_element : 075"  # scripted group (container) (typed FeaturePython)
  n = 5
  ref = O_element
FEATURE [App::DocumentObjectGroupPython] G4_DNA_CYTIDINE  # scripted group (container) (typed FeaturePython)
  Dunit = g/cm3
  Dvalue = 1
  Group = -> [H_element131,C_element141,N_element061,O_element122]
  conduct = 2
  density = 1
  expand = 3
  formula = G4_DNA_CYTIDINE
  name = G4_DNA_CYTIDINE
  specific = 4
FEATURE [App::DocumentObjectGroupPython] H_element132  label="H_element : 079"  # scripted group (container) (typed FeaturePython)
  n = 9
  ref = H_element
FEATURE [App::DocumentObjectGroupPython] C_element142  label="C_element : 087"  # scripted group (container) (typed FeaturePython)
  n = 9
  ref = C_element
FEATURE [App::DocumentObjectGroupPython] N_element062  label="N_element : 034"  # scripted group (container) (typed FeaturePython)
  n = 2
  ref = N_element
FEATURE [App::DocumentObjectGroupPython] O_element123  label="O_element : 076"  # scripted group (container) (typed FeaturePython)
  n = 6
  ref = O_element
FEATURE [App::DocumentObjectGroupPython] G4_DNA_URIDINE  # scripted group (container) (typed FeaturePython)
  Dunit = g/cm3
  Dvalue = 1
  Group = -> [H_element132,C_element142,N_element062,O_element123]
  conduct = 2
  density = 1
  expand = 3
  formula = G4_DNA_URIDINE
  name = G4_DNA_URIDINE
  specific = 4
FEATURE [App::DocumentObjectGroupPython] H_element133  label="H_element : 080"  # scripted group (container) (typed FeaturePython)
  n = 11
  ref = H_element
FEATURE [App::DocumentObjectGroupPython] C_element143  label="C_element : 088"  # scripted group (container) (typed FeaturePython)
  n = 10
  ref = C_element
FEATURE [App::DocumentObjectGroupPython] N_element063  label="N_element : 035"  # scripted group (container) (typed FeaturePython)
  n = 2
  ref = N_element
FEATURE [App::DocumentObjectGroupPython] O_element124  label="O_element : 077"  # scripted group (container) (typed FeaturePython)
  n = 6
  ref = O_element
FEATURE [App::DocumentObjectGroupPython] G4_DNA_METHYLURIDINE  # scripted group (container) (typed FeaturePython)
  Dunit = g/cm3
  Dvalue = 1
  Group = -> [H_element133,C_element143,N_element063,O_element124]
  conduct = 2
  density = 1
  expand = 3
  formula = G4_DNA_METHYLURIDINE
  name = G4_DNA_METHYLURIDINE
  specific = 4
FEATURE [App::DocumentObjectGroupPython] P_element014  label="P_element : 003"  # scripted group (container) (typed FeaturePython)
  n = 1
  ref = P_element
FEATURE [App::DocumentObjectGroupPython] O_element125  label="O_element : 078"  # scripted group (container) (typed FeaturePython)
  n = 3
  ref = O_element
FEATURE [App::DocumentObjectGroupPython] G4_DNA_MONOPHOSPHATE  # scripted group (container) (typed FeaturePython)
  Dunit = g/cm3
  Dvalue = 1
  Group = -> [P_element014,O_element125]
  conduct = 2
  density = 1
  expand = 3
  formula = G4_DNA_MONOPHOSPHATE
  name = G4_DNA_MONOPHOSPHATE
  specific = 4
FEATURE [App::DocumentObjectGroupPython] H_element134  label="H_element : 081"  # scripted group (container) (typed FeaturePython)
  n = 10
  ref = H_element
FEATURE [App::DocumentObjectGroupPython] C_element144  label="C_element : 089"  # scripted group (container) (typed FeaturePython)
  n = 10
  ref = C_element
FEATURE [App::DocumentObjectGroupPython] N_element064  label="N_element : 036"  # scripted group (container) (typed FeaturePython)
  n = 5
  ref = N_element
FEATURE [App::DocumentObjectGroupPython] O_element126  label="O_element : 079"  # scripted group (container) (typed FeaturePython)
  n = 7
  ref = O_element
FEATURE [App::DocumentObjectGroupPython] P_element015  label="P_element : 004"  # scripted group (container) (typed FeaturePython)
  n = 1
  ref = P_element
FEATURE [App::DocumentObjectGroupPython] G4_DNA_A  # scripted group (container) (typed FeaturePython)
  Dunit = g/cm3
  Dvalue = 1
  Group = -> [H_element134,C_element144,N_element064,O_element126,P_element015]
  conduct = 2
  density = 1
  expand = 3
  formula = G4_DNA_A
  name = G4_DNA_A
  specific = 4
FEATURE [App::DocumentObjectGroupPython] H_element135  label="H_element : 082"  # scripted group (container) (typed FeaturePython)
  n = 10
  ref = H_element
FEATURE [App::DocumentObjectGroupPython] C_element145  label="C_element : 090"  # scripted group (container) (typed FeaturePython)
  n = 10
  ref = C_element
FEATURE [App::DocumentObjectGroupPython] N_element065  label="N_element : 037"  # scripted group (container) (typed FeaturePython)
  n = 5
  ref = N_element
FEATURE [App::DocumentObjectGroupPython] O_element127  label="O_element : 8"  # scripted group (container) (typed FeaturePython)
  n = 8
  ref = O_element
FEATURE [App::DocumentObjectGroupPython] P_element016  label="P_element : 005"  # scripted group (container) (typed FeaturePython)
  n = 1
  ref = P_element
FEATURE [App::DocumentObjectGroupPython] G4_DNA_G  # scripted group (container) (typed FeaturePython)
  Dunit = g/cm3
  Dvalue = 1
  Group = -> [H_element135,C_element145,N_element065,O_element127,P_element016]
  conduct = 2
  density = 1
  expand = 3
  formula = G4_DNA_G
  name = G4_DNA_G
  specific = 4
FEATURE [App::DocumentObjectGroupPython] H_element136  label="H_element : 083"  # scripted group (container) (typed FeaturePython)
  n = 10
  ref = H_element
FEATURE [App::DocumentObjectGroupPython] C_element146  label="C_element : 091"  # scripted group (container) (typed FeaturePython)
  n = 9
  ref = C_element
FEATURE [App::DocumentObjectGroupPython] N_element066  label="N_element : 038"  # scripted group (container) (typed FeaturePython)
  n = 3
  ref = N_element
FEATURE [App::DocumentObjectGroupPython] O_element128  label="O_element : 080"  # scripted group (container) (typed FeaturePython)
  n = 8
  ref = O_element
FEATURE [App::DocumentObjectGroupPython] P_element017  label="P_element : 006"  # scripted group (container) (typed FeaturePython)
  n = 1
  ref = P_element
FEATURE [App::DocumentObjectGroupPython] G4_DNA_C  # scripted group (container) (typed FeaturePython)
  Dunit = g/cm3
  Dvalue = 1
  Group = -> [H_element136,C_element146,N_element066,O_element128,P_element017]
  conduct = 2
  density = 1
  expand = 3
  formula = G4_DNA_C
  name = G4_DNA_C
  specific = 4
FEATURE [App::DocumentObjectGroupPython] H_element137  label="H_element : 084"  # scripted group (container) (typed FeaturePython)
  n = 9
  ref = H_element
FEATURE [App::DocumentObjectGroupPython] C_element147  label="C_element : 092"  # scripted group (container) (typed FeaturePython)
  n = 9
  ref = C_element
FEATURE [App::DocumentObjectGroupPython] N_element067  label="N_element : 039"  # scripted group (container) (typed FeaturePython)
  n = 2
  ref = N_element
FEATURE [App::DocumentObjectGroupPython] O_element129  label="O_element : 9"  # scripted group (container) (typed FeaturePython)
  n = 9
  ref = O_element
FEATURE [App::DocumentObjectGroupPython] P_element018  label="P_element : 007"  # scripted group (container) (typed FeaturePython)
  n = 1
  ref = P_element
FEATURE [App::DocumentObjectGroupPython] G4_DNA_U  # scripted group (container) (typed FeaturePython)
  Dunit = g/cm3
  Dvalue = 1
  Group = -> [H_element137,C_element147,N_element067,O_element129,P_element018]
  conduct = 2
  density = 1
  expand = 3
  formula = G4_DNA_U
  name = G4_DNA_U
  specific = 4
FEATURE [App::DocumentObjectGroupPython] H_element138  label="H_element : 085"  # scripted group (container) (typed FeaturePython)
  n = 11
  ref = H_element
FEATURE [App::DocumentObjectGroupPython] C_element148  label="C_element : 093"  # scripted group (container) (typed FeaturePython)
  n = 10
  ref = C_element
FEATURE [App::DocumentObjectGroupPython] N_element068  label="N_element : 040"  # scripted group (container) (typed FeaturePython)
  n = 2
  ref = N_element
FEATURE [App::DocumentObjectGroupPython] O_element130  label="O_element : 081"  # scripted group (container) (typed FeaturePython)
  n = 9
  ref = O_element
FEATURE [App::DocumentObjectGroupPython] P_element019  label="P_element : 008"  # scripted group (container) (typed FeaturePython)
  n = 1
  ref = P_element
FEATURE [App::DocumentObjectGroupPython] G4_DNA_MU  # scripted group (container) (typed FeaturePython)
  Dunit = g/cm3
  Dvalue = 1
  Group = -> [H_element138,C_element148,N_element068,O_element130,P_element019]
  conduct = 2
  density = 1
  expand = 3
  formula = G4_DNA_MU
  name = G4_DNA_MU
  specific = 4
FEATURE [App::DocumentObjectGroupPython] BioChemical  # scripted group (container) (typed FeaturePython)
  Group = -> [G4_CYTOSINE,G4_THYMINE,G4_URACIL,G4_DNA_ADENINE,G4_DNA_GUANINE,G4_DNA_CYTOSINE,G4_DNA_THYMINE,G4_DNA_URACIL,G4_DNA_ADENOSINE,G4_DNA_GUANOSINE,G4_DNA_CYTIDINE,G4_DNA_URIDINE,G4_DNA_METHYLURIDINE,G4_DNA_MONOPHOSPHATE,G4_DNA_A,G4_DNA_G,G4_DNA_C,G4_DNA_U,G4_DNA_MU]
FEATURE [App::DocumentObjectGroupPython] G4Materials  # scripted group (container) (typed FeaturePython)
  Group = -> [NIST,Element,HEP,Space,BioChemical]
  version = 1
FEATURE [App::DocumentObjectGroupPython] Geant4  # scripted group (container) (typed FeaturePython)
  Group = -> [G4Isotopes,G4Elements,G4Materials]
FEATURE [App::DocumentObjectGroupPython] Materials  # scripted group (container) (typed FeaturePython)
  Group = -> [Geant4]
FEATURE [Part::FeaturePython] GDMLBox_WorldBox  # WARN: FeaturePython — macro-defined, semantics opaque (R4)
  lunit = 2
  material = 5
  x = 273
  y = 273
  z = 130
FEATURE [Part::FeaturePython] GDMLBox_Box  # WARN: FeaturePython — macro-defined, semantics opaque (R4)
  Placement = pos=(20,0,0) rot=(0,0,1;0rad)
  lunit = 2
  material = 0
  x = 10
  y = 10
  z = 10
FEATURE [Part::FeaturePython] GDMLTube  # WARN: FeaturePython — macro-defined, semantics opaque (R4)
  Placement = pos=(17,-4,0) rot=(0,0,1;0rad)
  aunit = 1
  deltaphi = 90
  lunit = 2
  material = 0
  rmax = 7
  rmin = 5
  startphi = 0
  z = 7
FEATURE [App::Part] LV_Tube
  Group = -> [GDMLTube]
  Origin = -> Origin003
  SkinSurface = 0
FEATURE [App::Part] LV_Box
  Group = -> [GDMLBox_Box,LV_Tube]
  Origin = -> Origin002
  Placement = pos=(0,0,0) rot=(0,0,1;-0.523599rad)
FEATURE [Part::FeaturePython] Array  # Draft array (typed FeaturePython)
  AlwaysSyncPlacement = false
  Angle = 180
  ArrayType = 1
  Axis = (0,0,1)
  Base = -> LV_Box
  Center = (-20,-20,0)
  Count = 5
  ExpandArray = false
  Fuse = false
  IntervalAxis = (0,0,0)
  IntervalX = (100,0,0)
  IntervalY = (0,100,0)
  IntervalZ = (0,0,100)
  NumberCircles = 3
  NumberPolar = 5
  NumberX = 2
  NumberY = 2
  NumberZ = 1
  PlacementList = 5 placements: [(0,0,0),(-20,8.28427,0),(-40,3.55271e-15,0),(-48.2843,-20,0),(-40,-40,0)]
  RadialDistance = 50
  ScaleList = (5) [(1,1,1),(1,1,1),(1,1,1),(1,1,1),(1,1,1)]
  Symmetry = 1
  TangentialDistance = 25
FEATURE [App::Part] Part  label="experiment"
  Group = -> [LV_Box,Array]
  Origin = -> Origin001
FEATURE [Part::Sphere] Sphere
  Angle1 = -90
  Angle2 = 90
  Angle3 = 360
  AttacherType = Attacher::AttachEngine3D
  Placement = pos=(-20,-20,0) rot=(0,0,1;0rad)
  Radius = 1
FEATURE [App::Part] Part001
  Group = -> [Sphere]
  Origin = -> Origin004
FEATURE [App::Part] worldVOL
  Group = -> [GDMLBox_WorldBox,Part,Part001]
  Origin = -> Origin
